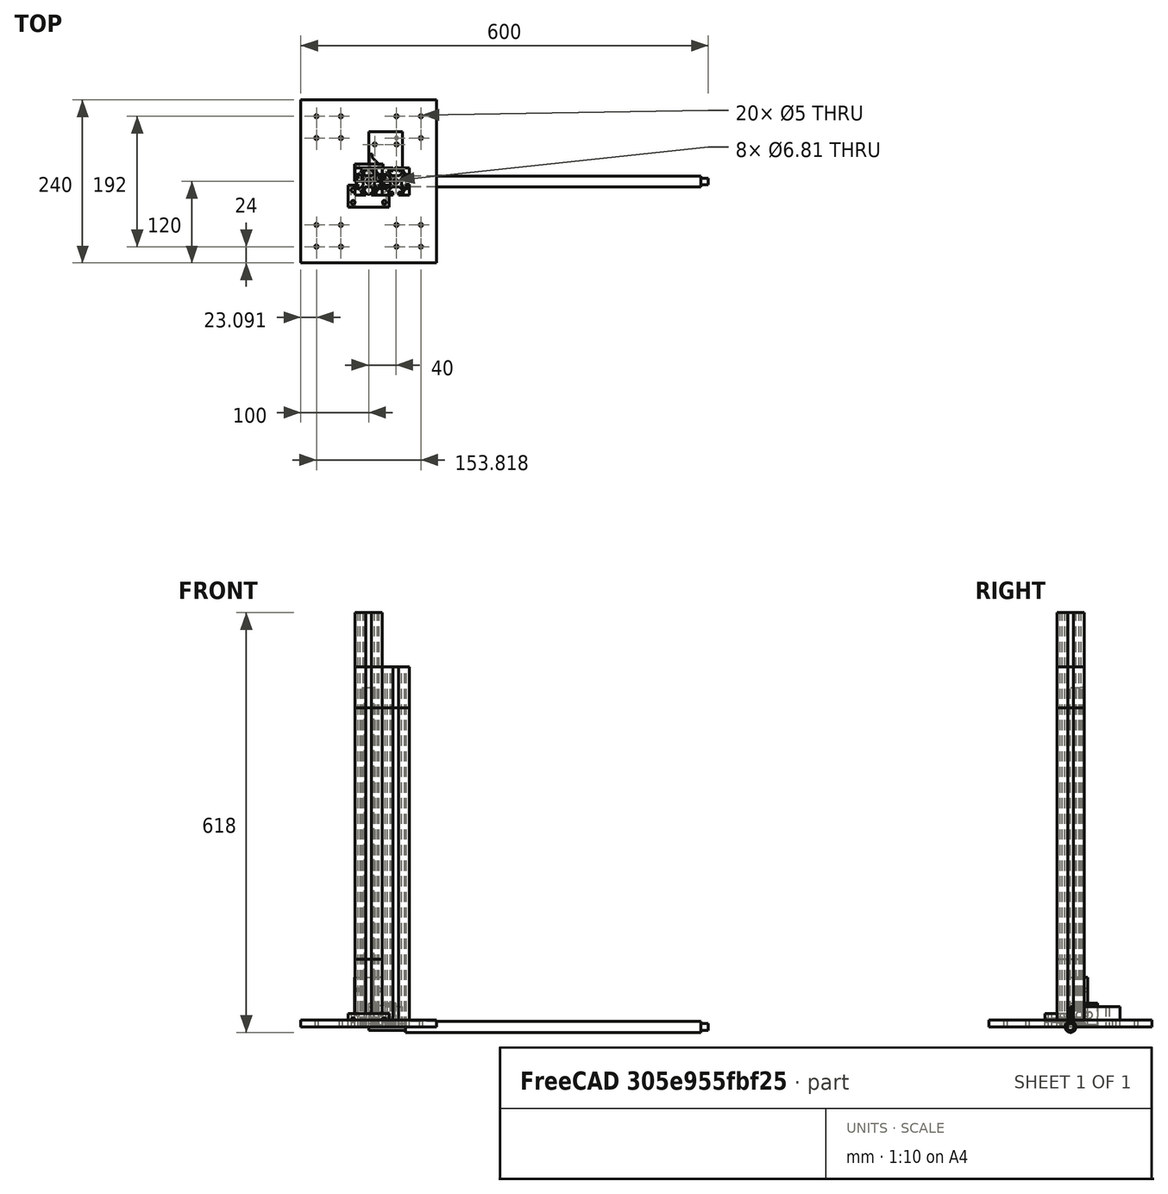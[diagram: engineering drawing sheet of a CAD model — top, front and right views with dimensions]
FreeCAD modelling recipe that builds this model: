
FCSTD DOCUMENT  (FreeCAD 1.1R39140 (Git))
Label: cnc
License: All rights reserved
LicenseURL: http://en.wikipedia.org/wiki/All_rights_reserved
objects: App::FeaturePython×78, App::Link×70, Sketcher::SketchObject×22, PartDesign::Body×12, PartDesign::Pad×11, Part::Extrusion×8, Part::Cut×8, Part::Box×2, PartDesign::Pocket×2, Spreadsheet::Sheet×1, PartDesign::Revolution×1, App::DocumentObjectGroup×1, Assembly::JointGroup×1, Assembly::AssemblyObject×1
note: 116 computed .brp shape members not serialized (recipe doc carries the construction recipe); baked Part::Feature solids carry a one-line shape summary decoded from their .brp
EXTERNAL_REF file=../xcadlib/nema23.FCStd obj=Body

FEATURE [Spreadsheet::Sheet] Spreadsheet
  cells = A1='length (x); B1(length)==24 in; A2='width (y); B2(width)==24 in; A3='height (z); B3(height)==20 in
FEATURE [Sketcher::SketchObject] Sketch001
  ArcFitTolerance = 1e-06
  AttachmentSupport = -> [XY_Plane001]
  FullyConstrained = true
  MakeInternals = false
  MapMode = 5
  sketch-geometry (37):
    g0: LineSegment StartX=-20 StartY=4.065 StartZ=0 EndX=-20 EndY=20 EndZ=0
    g1: LineSegment StartX=-20 StartY=20 StartZ=0 EndX=-4.065 EndY=20 EndZ=0
    g2: LineSegment StartX=-4.065 StartY=20 StartZ=0 EndX=-4.065 EndY=15.68 EndZ=0
    g3: LineSegment StartX=-4.065 StartY=15.68 StartZ=0 EndX=-12.6253 EndY=15.68 EndZ=0
    g4: LineSegment StartX=-12.6253 StartY=15.68 StartZ=0 EndX=-5.22957 EndY=8.28427 EndZ=0
    g5: LineSegment StartX=-5.22957 StartY=8.28427 StartZ=0 EndX=5.22957 EndY=8.28427 EndZ=0
    g6: LineSegment StartX=5.22957 StartY=8.28427 StartZ=0 EndX=12.6253 EndY=15.68 EndZ=0
    g7: LineSegment StartX=12.6253 StartY=15.68 StartZ=0 EndX=4.065 EndY=15.68 EndZ=0
    g8: LineSegment StartX=4.065 StartY=15.68 StartZ=0 EndX=4.065 EndY=20 EndZ=0
    g9: LineSegment StartX=4.065 StartY=20 StartZ=0 EndX=20 EndY=20 EndZ=0
    g10: LineSegment StartX=20 StartY=20 StartZ=0 EndX=20 EndY=4.065 EndZ=0
    g11: LineSegment StartX=20 StartY=4.065 StartZ=0 EndX=15.68 EndY=4.065 EndZ=0
    g12: LineSegment StartX=15.68 StartY=4.065 StartZ=0 EndX=15.68 EndY=12.6253 EndZ=0
    g13: LineSegment StartX=15.68 StartY=12.6253 StartZ=0 EndX=8.28427 EndY=5.22957 EndZ=0
    g14: LineSegment StartX=8.28427 StartY=5.22957 StartZ=0 EndX=8.28427 EndY=-5.22957 EndZ=0
    g15: LineSegment StartX=8.28427 StartY=-5.22957 StartZ=0 EndX=15.68 EndY=-12.6253 EndZ=0
    g16: LineSegment StartX=15.68 StartY=-12.6253 StartZ=0 EndX=15.68 EndY=-4.065 EndZ=0
    g17: LineSegment StartX=15.68 StartY=-4.065 StartZ=0 EndX=20 EndY=-4.065 EndZ=0
    g18: LineSegment StartX=20 StartY=-4.065 StartZ=0 EndX=20 EndY=-20 EndZ=0
    g19: LineSegment StartX=20 StartY=-20 StartZ=0 EndX=4.065 EndY=-20 EndZ=0
    g20: LineSegment StartX=4.065 StartY=-20 StartZ=0 EndX=4.065 EndY=-15.68 EndZ=0
    g21: LineSegment StartX=4.065 StartY=-15.68 StartZ=0 EndX=12.6253 EndY=-15.68 EndZ=0
    g22: LineSegment StartX=12.6253 StartY=-15.68 StartZ=0 EndX=5.22957 EndY=-8.28427 EndZ=0
    g23: LineSegment StartX=5.22957 StartY=-8.28427 StartZ=0 EndX=-5.22957 EndY=-8.28427 EndZ=0
    g24: LineSegment StartX=-5.22957 StartY=-8.28427 StartZ=0 EndX=-12.6253 EndY=-15.68 EndZ=0
    g25: LineSegment StartX=-12.6253 StartY=-15.68 StartZ=0 EndX=-4.065 EndY=-15.68 EndZ=0
    g26: LineSegment StartX=-4.065 StartY=-15.68 StartZ=0 EndX=-4.065 EndY=-20 EndZ=0
    g27: LineSegment StartX=-4.065 StartY=-20 StartZ=0 EndX=-20 EndY=-20 EndZ=0
    g28: LineSegment StartX=-20 StartY=-20 StartZ=0 EndX=-20 EndY=-4.065 EndZ=0
    g29: LineSegment StartX=-20 StartY=-4.065 StartZ=0 EndX=-15.68 EndY=-4.065 EndZ=0
    g30: LineSegment StartX=-15.68 StartY=-4.065 StartZ=0 EndX=-15.68 EndY=-12.6253 EndZ=0
    g31: LineSegment StartX=-15.68 StartY=-12.6253 StartZ=0 EndX=-8.28427 EndY=-5.22957 EndZ=0
    g32: LineSegment StartX=-8.28427 StartY=-5.22957 StartZ=0 EndX=-8.28427 EndY=5.22957 EndZ=0
    g33: LineSegment StartX=-8.28427 StartY=5.22957 StartZ=0 EndX=-15.68 EndY=12.6253 EndZ=0
    g34: LineSegment StartX=-15.68 StartY=12.6253 StartZ=0 EndX=-15.68 EndY=4.065 EndZ=0
    g35: LineSegment StartX=-15.68 StartY=4.065 StartZ=0 EndX=-20 EndY=4.065 EndZ=0
    g36: Circle CenterX=0 CenterY=0 CenterZ=0 NormalX=0 NormalY=0 NormalZ=1 AngleXU=0 Radius=3.405
  constraints (100):
    c: Coincident(g24,g23)
    c: Coincident(g32,g31)
    c: Coincident(g30,g31)
    c: Coincident(g25,g24)
    c: Coincident(g25,g26)
    c: Coincident(g20,g21)
    c: Coincident(g19,g20)
    c: Coincident(g26,g27)
    c: Coincident(g28,g27)
    c: Coincident(g21,g22)
    c: Coincident(g19,g18)
    c: Coincident(g16,g15)
    c: Coincident(g14,g15)
    c: Coincident(g23,g22)
    c: Coincident(g16,g17)
    c: Coincident(g18,g17)
    c: Coincident(g12,g11)
    c: Coincident(g11,g10)
    c: Coincident(g10,g9)
    c: Coincident(g13,g12)
    c: Coincident(g13,g14)
    c: Coincident(g6,g5)
    c: Coincident(g7,g6)
    c: Coincident(g8,g7)
    c: Coincident(g9,g8)
    c: Coincident(g2,g1)
    c: Coincident(g2,g3)
    c: Coincident(g4,g3)
    c: Coincident(g34,g33)
    c: Coincident(g5,g4)
    c: Coincident(g33,g32)
    c: Coincident(g35,g34)
    c: Coincident(g35,g0)
    c: Coincident(g1,g0)
    c: Coincident(g30,g29)
    c: Coincident(g29,g28)
    c: Distance(g10,g0) = 40
    c: Distance(g27,g1) = 40
    c: Tangent(g1,g9)
    c: Tangent(g27,g19)
    c: Tangent(g0,g28)
    c: Tangent(g10,g18)
    c: Horizontal(g1)
    c: Vertical(g0)
    c: Equal(g2,g8)
    c: Equal(g8,g35)
    c: Equal(g35,g29)
    c: Equal(g29,g26)
    c: Equal(g26,g20)
    c: Equal(g20,g17)
    c: Equal(g17,g11)
    c: Vertical(g34)
    c: Vertical(g30)
    c: Vertical(g16)
    c: Vertical(g18)
    c: Vertical(g12)
    c: Vertical(g8)
    c: Vertical(g2)
    c: Vertical(g14)
    c: Vertical(g32)
    c: Horizontal(g35)
    c: Horizontal(g29)
    c: Horizontal(g23)
    c: Horizontal(g19)
    c: Horizontal(g25)
    c: Horizontal(g21)
    c: Horizontal(g7)
    c: Horizontal(g3)
    c: Parallel(g4,g33)
    c: Parallel(g33,g15)
    c: Parallel(g15,g22)
    c: Parallel(g6,g13)
    c: Parallel(g13,g24)
    c: Parallel(g24,g31)
    c: Equal(g23,g24)
    c: Equal(g24,g31)
    c: Equal(g4,g33)
    c: Equal(g6,g13)
    c: Equal(g15,g22)
    c: Angle(g25,g24) = 0.785398
    c: Distance(g8,g2) = 8.13
    c: Distance(g29,g35) = 8.13
    c: Tangent(g35,g11)
    c: Tangent(g17,g29)
    c: Tangent(g2,g26)
    c: Tangent(g8,g20)
    c: Distance(g22,g15) = 4.32
    c: Distance(g13,g6) = 4.32
    c: Distance(g33,g4) = 4.32
    c: Distance(g24,g31) = 4.32
    c: Equal(g32,g14)
    c: Equal(g5,g23)
    c: Equal(g25,g21)
    c: Equal(g34,g30)
    c: Distance(g35,g35) = 4.32
    c: Symmetric(g5,g22,g-1)
    c: Symmetric(g4,g5,g-2)
    c: Equal(g5,g32)
    c: Coincident(g36,g-1)
    c: Diameter(g36) = 6.81
FEATURE [Sketcher::SketchObject] Sketch002
  ArcFitTolerance = 1e-06
  AttachmentSupport = -> [XY_Plane003]
  FullyConstrained = true
  MakeInternals = false
  MapMode = 5
  sketch-geometry (37):
    g0: LineSegment StartX=-20 StartY=4.065 StartZ=0 EndX=-20 EndY=20 EndZ=0
    g1: LineSegment StartX=-20 StartY=20 StartZ=0 EndX=-4.065 EndY=20 EndZ=0
    g2: LineSegment StartX=-4.065 StartY=20 StartZ=0 EndX=-4.065 EndY=15.68 EndZ=0
    g3: LineSegment StartX=-4.065 StartY=15.68 StartZ=0 EndX=-12.6253 EndY=15.68 EndZ=0
    g4: LineSegment StartX=-12.6253 StartY=15.68 StartZ=0 EndX=-5.22957 EndY=8.28427 EndZ=0
    g5: LineSegment StartX=-5.22957 StartY=8.28427 StartZ=0 EndX=5.22957 EndY=8.28427 EndZ=0
    g6: LineSegment StartX=5.22957 StartY=8.28427 StartZ=0 EndX=12.6253 EndY=15.68 EndZ=0
    g7: LineSegment StartX=12.6253 StartY=15.68 StartZ=0 EndX=4.065 EndY=15.68 EndZ=0
    g8: LineSegment StartX=4.065 StartY=15.68 StartZ=0 EndX=4.065 EndY=20 EndZ=0
    g9: LineSegment StartX=4.065 StartY=20 StartZ=0 EndX=20 EndY=20 EndZ=0
    g10: LineSegment StartX=20 StartY=20 StartZ=0 EndX=20 EndY=4.065 EndZ=0
    g11: LineSegment StartX=20 StartY=4.065 StartZ=0 EndX=15.68 EndY=4.065 EndZ=0
    g12: LineSegment StartX=15.68 StartY=4.065 StartZ=0 EndX=15.68 EndY=12.6253 EndZ=0
    g13: LineSegment StartX=15.68 StartY=12.6253 StartZ=0 EndX=8.28427 EndY=5.22957 EndZ=0
    g14: LineSegment StartX=8.28427 StartY=5.22957 StartZ=0 EndX=8.28427 EndY=-5.22957 EndZ=0
    g15: LineSegment StartX=8.28427 StartY=-5.22957 StartZ=0 EndX=15.68 EndY=-12.6253 EndZ=0
    g16: LineSegment StartX=15.68 StartY=-12.6253 StartZ=0 EndX=15.68 EndY=-4.065 EndZ=0
    g17: LineSegment StartX=15.68 StartY=-4.065 StartZ=0 EndX=20 EndY=-4.065 EndZ=0
    g18: LineSegment StartX=20 StartY=-4.065 StartZ=0 EndX=20 EndY=-20 EndZ=0
    g19: LineSegment StartX=20 StartY=-20 StartZ=0 EndX=4.065 EndY=-20 EndZ=0
    g20: LineSegment StartX=4.065 StartY=-20 StartZ=0 EndX=4.065 EndY=-15.68 EndZ=0
    g21: LineSegment StartX=4.065 StartY=-15.68 StartZ=0 EndX=12.6253 EndY=-15.68 EndZ=0
    g22: LineSegment StartX=12.6253 StartY=-15.68 StartZ=0 EndX=5.22957 EndY=-8.28427 EndZ=0
    g23: LineSegment StartX=5.22957 StartY=-8.28427 StartZ=0 EndX=-5.22957 EndY=-8.28427 EndZ=0
    g24: LineSegment StartX=-5.22957 StartY=-8.28427 StartZ=0 EndX=-12.6253 EndY=-15.68 EndZ=0
    g25: LineSegment StartX=-12.6253 StartY=-15.68 StartZ=0 EndX=-4.065 EndY=-15.68 EndZ=0
    g26: LineSegment StartX=-4.065 StartY=-15.68 StartZ=0 EndX=-4.065 EndY=-20 EndZ=0
    g27: LineSegment StartX=-4.065 StartY=-20 StartZ=0 EndX=-20 EndY=-20 EndZ=0
    g28: LineSegment StartX=-20 StartY=-20 StartZ=0 EndX=-20 EndY=-4.065 EndZ=0
    g29: LineSegment StartX=-20 StartY=-4.065 StartZ=0 EndX=-15.68 EndY=-4.065 EndZ=0
    g30: LineSegment StartX=-15.68 StartY=-4.065 StartZ=0 EndX=-15.68 EndY=-12.6253 EndZ=0
    g31: LineSegment StartX=-15.68 StartY=-12.6253 StartZ=0 EndX=-8.28427 EndY=-5.22957 EndZ=0
    g32: LineSegment StartX=-8.28427 StartY=-5.22957 StartZ=0 EndX=-8.28427 EndY=5.22957 EndZ=0
    g33: LineSegment StartX=-8.28427 StartY=5.22957 StartZ=0 EndX=-15.68 EndY=12.6253 EndZ=0
    g34: LineSegment StartX=-15.68 StartY=12.6253 StartZ=0 EndX=-15.68 EndY=4.065 EndZ=0
    g35: LineSegment StartX=-15.68 StartY=4.065 StartZ=0 EndX=-20 EndY=4.065 EndZ=0
    g36: Circle CenterX=0 CenterY=0 CenterZ=0 NormalX=0 NormalY=0 NormalZ=1 AngleXU=0 Radius=3.405
  constraints (100):
    c: Coincident(g24,g23)
    c: Coincident(g32,g31)
    c: Coincident(g30,g31)
    c: Coincident(g25,g24)
    c: Coincident(g25,g26)
    c: Coincident(g20,g21)
    c: Coincident(g19,g20)
    c: Coincident(g26,g27)
    c: Coincident(g28,g27)
    c: Coincident(g21,g22)
    c: Coincident(g19,g18)
    c: Coincident(g16,g15)
    c: Coincident(g14,g15)
    c: Coincident(g23,g22)
    c: Coincident(g16,g17)
    c: Coincident(g18,g17)
    c: Coincident(g12,g11)
    c: Coincident(g11,g10)
    c: Coincident(g10,g9)
    c: Coincident(g13,g12)
    c: Coincident(g13,g14)
    c: Coincident(g6,g5)
    c: Coincident(g7,g6)
    c: Coincident(g8,g7)
    c: Coincident(g9,g8)
    c: Coincident(g2,g1)
    c: Coincident(g2,g3)
    c: Coincident(g4,g3)
    c: Coincident(g34,g33)
    c: Coincident(g5,g4)
    c: Coincident(g33,g32)
    c: Coincident(g35,g34)
    c: Coincident(g35,g0)
    c: Coincident(g1,g0)
    c: Coincident(g30,g29)
    c: Coincident(g29,g28)
    c: Distance(g10,g0) = 40
    c: Distance(g27,g1) = 40
    c: Tangent(g1,g9)
    c: Tangent(g27,g19)
    c: Tangent(g0,g28)
    c: Tangent(g10,g18)
    c: Horizontal(g1)
    c: Vertical(g0)
    c: Equal(g2,g8)
    c: Equal(g8,g35)
    c: Equal(g35,g29)
    c: Equal(g29,g26)
    c: Equal(g26,g20)
    c: Equal(g20,g17)
    c: Equal(g17,g11)
    c: Vertical(g34)
    c: Vertical(g30)
    c: Vertical(g16)
    c: Vertical(g18)
    c: Vertical(g12)
    c: Vertical(g8)
    c: Vertical(g2)
    c: Vertical(g14)
    c: Vertical(g32)
    c: Horizontal(g35)
    c: Horizontal(g29)
    c: Horizontal(g23)
    c: Horizontal(g19)
    c: Horizontal(g25)
    c: Horizontal(g21)
    c: Horizontal(g7)
    c: Horizontal(g3)
    c: Parallel(g4,g33)
    c: Parallel(g33,g15)
    c: Parallel(g15,g22)
    c: Parallel(g6,g13)
    c: Parallel(g13,g24)
    c: Parallel(g24,g31)
    c: Equal(g23,g24)
    c: Equal(g24,g31)
    c: Equal(g4,g33)
    c: Equal(g6,g13)
    c: Equal(g15,g22)
    c: Angle(g25,g24) = 0.785398
    c: Distance(g8,g2) = 8.13
    c: Distance(g29,g35) = 8.13
    c: Tangent(g35,g11)
    c: Tangent(g17,g29)
    c: Tangent(g2,g26)
    c: Tangent(g8,g20)
    c: Distance(g22,g15) = 4.32
    c: Distance(g13,g6) = 4.32
    c: Distance(g33,g4) = 4.32
    c: Distance(g24,g31) = 4.32
    c: Equal(g32,g14)
    c: Equal(g5,g23)
    c: Equal(g25,g21)
    c: Equal(g34,g30)
    c: Distance(g35,g35) = 4.32
    c: Symmetric(g5,g22,g-1)
    c: Symmetric(g4,g5,g-2)
    c: Equal(g5,g32)
    c: Coincident(g36,g-1)
    c: Diameter(g36) = 6.81
FEATURE [PartDesign::Pad] Pad
  Direction = (0,0,1)
  Length = 610
  Length2 = 10
  Profile = -> Sketch001
  ReferenceAxis = -> Sketch001 [N_Axis]
  Refine = true
  Suppressed = false
  Type = 0
FEATURE [PartDesign::Body] Body001  label="4040 extrusion @ 610"
  AllowCompound = false
  Group = -> [Sketch001,Pad]
  Origin = -> Origin001
  Tip = -> Pad
FEATURE [PartDesign::Pad] Pad001
  Direction = (0,0,1)
  Length = 530
  Length2 = 10
  Profile = -> Sketch002
  ReferenceAxis = -> Sketch002 [N_Axis]
  Refine = true
  Suppressed = false
  Type = 0
FEATURE [PartDesign::Body] Body002  label="4040 extrusion @ 530"
  AllowCompound = false
  Group = -> [Sketch002,Pad001]
  Origin = -> Origin003
  Tip = -> Pad001
FEATURE [Sketcher::SketchObject] Sketch003
  ArcFitTolerance = 1e-06
  AttachmentSupport = -> [XY_Plane005]
  FullyConstrained = true
  MakeInternals = false
  MapMode = 5
  sketch-geometry (37):
    g0: LineSegment StartX=-20 StartY=4.065 StartZ=0 EndX=-20 EndY=20 EndZ=0
    g1: LineSegment StartX=-20 StartY=20 StartZ=0 EndX=-4.065 EndY=20 EndZ=0
    g2: LineSegment StartX=-4.065 StartY=20 StartZ=0 EndX=-4.065 EndY=15.68 EndZ=0
    g3: LineSegment StartX=-4.065 StartY=15.68 StartZ=0 EndX=-12.6253 EndY=15.68 EndZ=0
    g4: LineSegment StartX=-12.6253 StartY=15.68 StartZ=0 EndX=-5.22957 EndY=8.28427 EndZ=0
    g5: LineSegment StartX=-5.22957 StartY=8.28427 StartZ=0 EndX=5.22957 EndY=8.28427 EndZ=0
    g6: LineSegment StartX=5.22957 StartY=8.28427 StartZ=0 EndX=12.6253 EndY=15.68 EndZ=0
    g7: LineSegment StartX=12.6253 StartY=15.68 StartZ=0 EndX=4.065 EndY=15.68 EndZ=0
    g8: LineSegment StartX=4.065 StartY=15.68 StartZ=0 EndX=4.065 EndY=20 EndZ=0
    g9: LineSegment StartX=4.065 StartY=20 StartZ=0 EndX=20 EndY=20 EndZ=0
    g10: LineSegment StartX=20 StartY=20 StartZ=0 EndX=20 EndY=4.065 EndZ=0
    g11: LineSegment StartX=20 StartY=4.065 StartZ=0 EndX=15.68 EndY=4.065 EndZ=0
    g12: LineSegment StartX=15.68 StartY=4.065 StartZ=0 EndX=15.68 EndY=12.6253 EndZ=0
    g13: LineSegment StartX=15.68 StartY=12.6253 StartZ=0 EndX=8.28427 EndY=5.22957 EndZ=0
    g14: LineSegment StartX=8.28427 StartY=5.22957 StartZ=0 EndX=8.28427 EndY=-5.22957 EndZ=0
    g15: LineSegment StartX=8.28427 StartY=-5.22957 StartZ=0 EndX=15.68 EndY=-12.6253 EndZ=0
    g16: LineSegment StartX=15.68 StartY=-12.6253 StartZ=0 EndX=15.68 EndY=-4.065 EndZ=0
    g17: LineSegment StartX=15.68 StartY=-4.065 StartZ=0 EndX=20 EndY=-4.065 EndZ=0
    g18: LineSegment StartX=20 StartY=-4.065 StartZ=0 EndX=20 EndY=-20 EndZ=0
    g19: LineSegment StartX=20 StartY=-20 StartZ=0 EndX=4.065 EndY=-20 EndZ=0
    g20: LineSegment StartX=4.065 StartY=-20 StartZ=0 EndX=4.065 EndY=-15.68 EndZ=0
    g21: LineSegment StartX=4.065 StartY=-15.68 StartZ=0 EndX=12.6253 EndY=-15.68 EndZ=0
    g22: LineSegment StartX=12.6253 StartY=-15.68 StartZ=0 EndX=5.22957 EndY=-8.28427 EndZ=0
    g23: LineSegment StartX=5.22957 StartY=-8.28427 StartZ=0 EndX=-5.22957 EndY=-8.28427 EndZ=0
    g24: LineSegment StartX=-5.22957 StartY=-8.28427 StartZ=0 EndX=-12.6253 EndY=-15.68 EndZ=0
    g25: LineSegment StartX=-12.6253 StartY=-15.68 StartZ=0 EndX=-4.065 EndY=-15.68 EndZ=0
    g26: LineSegment StartX=-4.065 StartY=-15.68 StartZ=0 EndX=-4.065 EndY=-20 EndZ=0
    g27: LineSegment StartX=-4.065 StartY=-20 StartZ=0 EndX=-20 EndY=-20 EndZ=0
    g28: LineSegment StartX=-20 StartY=-20 StartZ=0 EndX=-20 EndY=-4.065 EndZ=0
    g29: LineSegment StartX=-20 StartY=-4.065 StartZ=0 EndX=-15.68 EndY=-4.065 EndZ=0
    g30: LineSegment StartX=-15.68 StartY=-4.065 StartZ=0 EndX=-15.68 EndY=-12.6253 EndZ=0
    g31: LineSegment StartX=-15.68 StartY=-12.6253 StartZ=0 EndX=-8.28427 EndY=-5.22957 EndZ=0
    g32: LineSegment StartX=-8.28427 StartY=-5.22957 StartZ=0 EndX=-8.28427 EndY=5.22957 EndZ=0
    g33: LineSegment StartX=-8.28427 StartY=5.22957 StartZ=0 EndX=-15.68 EndY=12.6253 EndZ=0
    g34: LineSegment StartX=-15.68 StartY=12.6253 StartZ=0 EndX=-15.68 EndY=4.065 EndZ=0
    g35: LineSegment StartX=-15.68 StartY=4.065 StartZ=0 EndX=-20 EndY=4.065 EndZ=0
    g36: Circle CenterX=0 CenterY=0 CenterZ=0 NormalX=0 NormalY=0 NormalZ=1 AngleXU=0 Radius=3.405
  constraints (100):
    c: Coincident(g24,g23)
    c: Coincident(g32,g31)
    c: Coincident(g30,g31)
    c: Coincident(g25,g24)
    c: Coincident(g25,g26)
    c: Coincident(g20,g21)
    c: Coincident(g19,g20)
    c: Coincident(g26,g27)
    c: Coincident(g28,g27)
    c: Coincident(g21,g22)
    c: Coincident(g19,g18)
    c: Coincident(g16,g15)
    c: Coincident(g14,g15)
    c: Coincident(g23,g22)
    c: Coincident(g16,g17)
    c: Coincident(g18,g17)
    c: Coincident(g12,g11)
    c: Coincident(g11,g10)
    c: Coincident(g10,g9)
    c: Coincident(g13,g12)
    c: Coincident(g13,g14)
    c: Coincident(g6,g5)
    c: Coincident(g7,g6)
    c: Coincident(g8,g7)
    c: Coincident(g9,g8)
    c: Coincident(g2,g1)
    c: Coincident(g2,g3)
    c: Coincident(g4,g3)
    c: Coincident(g34,g33)
    c: Coincident(g5,g4)
    c: Coincident(g33,g32)
    c: Coincident(g35,g34)
    c: Coincident(g35,g0)
    c: Coincident(g1,g0)
    c: Coincident(g30,g29)
    c: Coincident(g29,g28)
    c: Distance(g10,g0) = 40
    c: Distance(g27,g1) = 40
    c: Tangent(g1,g9)
    c: Tangent(g27,g19)
    c: Tangent(g0,g28)
    c: Tangent(g10,g18)
    c: Horizontal(g1)
    c: Vertical(g0)
    c: Equal(g2,g8)
    c: Equal(g8,g35)
    c: Equal(g35,g29)
    c: Equal(g29,g26)
    c: Equal(g26,g20)
    c: Equal(g20,g17)
    c: Equal(g17,g11)
    c: Vertical(g34)
    c: Vertical(g30)
    c: Vertical(g16)
    c: Vertical(g18)
    c: Vertical(g12)
    c: Vertical(g8)
    c: Vertical(g2)
    c: Vertical(g14)
    c: Vertical(g32)
    c: Horizontal(g35)
    c: Horizontal(g29)
    c: Horizontal(g23)
    c: Horizontal(g19)
    c: Horizontal(g25)
    c: Horizontal(g21)
    c: Horizontal(g7)
    c: Horizontal(g3)
    c: Parallel(g4,g33)
    c: Parallel(g33,g15)
    c: Parallel(g15,g22)
    c: Parallel(g6,g13)
    c: Parallel(g13,g24)
    c: Parallel(g24,g31)
    c: Equal(g23,g24)
    c: Equal(g24,g31)
    c: Equal(g4,g33)
    c: Equal(g6,g13)
    c: Equal(g15,g22)
    c: Angle(g25,g24) = 0.785398
    c: Distance(g8,g2) = 8.13
    c: Distance(g29,g35) = 8.13
    c: Tangent(g35,g11)
    c: Tangent(g17,g29)
    c: Tangent(g2,g26)
    c: Tangent(g8,g20)
    c: Distance(g22,g15) = 4.32
    c: Distance(g13,g6) = 4.32
    c: Distance(g33,g4) = 4.32
    c: Distance(g24,g31) = 4.32
    c: Equal(g32,g14)
    c: Equal(g5,g23)
    c: Equal(g25,g21)
    c: Equal(g34,g30)
    c: Distance(g35,g35) = 4.32
    c: Symmetric(g5,g22,g-1)
    c: Symmetric(g4,g5,g-2)
    c: Equal(g5,g32)
    c: Coincident(g36,g-1)
    c: Diameter(g36) = 6.81
FEATURE [PartDesign::Pad] Pad002
  Direction = (0,0,1)
  Length = 470
  Length2 = 10
  Profile = -> Sketch003
  ReferenceAxis = -> Sketch003 [N_Axis]
  Refine = true
  Suppressed = false
  Type = 0
FEATURE [PartDesign::Body] Body003  label="4040 extrusion @ 470"
  AllowCompound = false
  Group = -> [Sketch003,Pad002]
  Origin = -> Origin005
  Tip = -> Pad002
FEATURE [Sketcher::SketchObject] Sketch004
  ArcFitTolerance = 1e-06
  AttachmentSupport = -> [XY_Plane006]
  FullyConstrained = true
  MakeInternals = false
  MapMode = 5
  sketch-geometry (70):
    g0: LineSegment StartX=-20 StartY=4.065 StartZ=0 EndX=-20 EndY=20 EndZ=0
    g1: LineSegment StartX=-20 StartY=20 StartZ=0 EndX=-4.065 EndY=20 EndZ=0
    g2: LineSegment StartX=-4.065 StartY=20 StartZ=0 EndX=-4.065 EndY=15.68 EndZ=0
    g3: LineSegment StartX=-4.065 StartY=15.68 StartZ=0 EndX=-12.6253 EndY=15.68 EndZ=0
    g4: LineSegment StartX=-12.6253 StartY=15.68 StartZ=0 EndX=-5.22957 EndY=8.28427 EndZ=0
    g5: LineSegment StartX=-5.22957 StartY=8.28427 StartZ=0 EndX=5.22957 EndY=8.28427 EndZ=0
    g6: LineSegment StartX=5.22957 StartY=8.28427 StartZ=0 EndX=12.6253 EndY=15.68 EndZ=0
    g7: LineSegment StartX=12.6253 StartY=15.68 StartZ=0 EndX=4.065 EndY=15.68 EndZ=0
    g8: LineSegment StartX=4.065 StartY=15.68 StartZ=0 EndX=4.065 EndY=20 EndZ=0
    g9: LineSegment StartX=4.065 StartY=20 StartZ=0 EndX=20 EndY=20 EndZ=0
    g10: LineSegment StartX=20 StartY=4.065 StartZ=0 EndX=15.68 EndY=4.065 EndZ=0
    g11: LineSegment StartX=15.68 StartY=4.065 StartZ=0 EndX=15.68 EndY=12.6253 EndZ=0
    g12: LineSegment StartX=15.68 StartY=12.6253 StartZ=0 EndX=8.28427 EndY=5.22957 EndZ=0
    g13: LineSegment StartX=8.28427 StartY=5.22957 StartZ=0 EndX=8.28427 EndY=-5.22957 EndZ=0
    g14: LineSegment StartX=8.28427 StartY=-5.22957 StartZ=0 EndX=15.68 EndY=-12.6253 EndZ=0
    g15: LineSegment StartX=15.68 StartY=-12.6253 StartZ=0 EndX=15.68 EndY=-4.065 EndZ=0
    g16: LineSegment StartX=15.68 StartY=-4.065 StartZ=0 EndX=20 EndY=-4.065 EndZ=0
    g17: LineSegment StartX=20 StartY=-20 StartZ=0 EndX=4.065 EndY=-20 EndZ=0
    g18: LineSegment StartX=4.065 StartY=-20 StartZ=0 EndX=4.065 EndY=-15.68 EndZ=0
    g19: LineSegment StartX=4.065 StartY=-15.68 StartZ=0 EndX=12.6253 EndY=-15.68 EndZ=0
    g20: LineSegment StartX=12.6253 StartY=-15.68 StartZ=0 EndX=5.22957 EndY=-8.28427 EndZ=0
    g21: LineSegment StartX=5.22957 StartY=-8.28427 StartZ=0 EndX=-5.22957 EndY=-8.28427 EndZ=0
    g22: LineSegment StartX=-5.22957 StartY=-8.28427 StartZ=0 EndX=-12.6253 EndY=-15.68 EndZ=0
    g23: LineSegment StartX=-12.6253 StartY=-15.68 StartZ=0 EndX=-4.065 EndY=-15.68 EndZ=0
    g24: LineSegment StartX=-4.065 StartY=-15.68 StartZ=0 EndX=-4.065 EndY=-20 EndZ=0
    g25: LineSegment StartX=-4.065 StartY=-20 StartZ=0 EndX=-20 EndY=-20 EndZ=0
    g26: LineSegment StartX=-20 StartY=-20 StartZ=0 EndX=-20 EndY=-4.065 EndZ=0
    g27: LineSegment StartX=-20 StartY=-4.065 StartZ=0 EndX=-15.68 EndY=-4.065 EndZ=0
    g28: LineSegment StartX=-15.68 StartY=-4.065 StartZ=0 EndX=-15.68 EndY=-12.6253 EndZ=0
    g29: LineSegment StartX=-15.68 StartY=-12.6253 StartZ=0 EndX=-8.28427 EndY=-5.22957 EndZ=0
    g30: LineSegment StartX=-8.28427 StartY=-5.22957 StartZ=0 EndX=-8.28427 EndY=5.22957 EndZ=0
    g31: LineSegment StartX=-8.28427 StartY=5.22957 StartZ=0 EndX=-15.68 EndY=12.6253 EndZ=0
    g32: LineSegment StartX=-15.68 StartY=12.6253 StartZ=0 EndX=-15.68 EndY=4.065 EndZ=0
    g33: LineSegment StartX=-15.68 StartY=4.065 StartZ=0 EndX=-20 EndY=4.065 EndZ=0
    g34: Circle CenterX=0 CenterY=0 CenterZ=0 NormalX=0 NormalY=0 NormalZ=1 AngleXU=0 Radius=3.405
    g35: LineSegment StartX=20 StartY=20 StartZ=0 EndX=35.935 EndY=20 EndZ=0
    g36: LineSegment StartX=35.935 StartY=20 StartZ=0 EndX=35.935 EndY=15.68 EndZ=0
    g37: LineSegment StartX=35.935 StartY=15.68 StartZ=0 EndX=27.3747 EndY=15.68 EndZ=0
    g38: LineSegment StartX=27.3747 StartY=15.68 StartZ=0 EndX=34.7704 EndY=8.28427 EndZ=0
    g39: LineSegment StartX=34.7704 StartY=8.28427 StartZ=0 EndX=45.2296 EndY=8.28427 EndZ=0
    g40: LineSegment StartX=45.2296 StartY=8.28427 StartZ=0 EndX=52.6253 EndY=15.68 EndZ=0
    g41: LineSegment StartX=52.6253 StartY=15.68 StartZ=0 EndX=44.065 EndY=15.68 EndZ=0
    g42: LineSegment StartX=44.065 StartY=15.68 StartZ=0 EndX=44.065 EndY=20 EndZ=0
    g43: LineSegment StartX=44.065 StartY=20 StartZ=0 EndX=60 EndY=20 EndZ=0
    g44: LineSegment StartX=60 StartY=20 StartZ=0 EndX=60 EndY=4.065 EndZ=0
    g45: LineSegment StartX=60 StartY=4.065 StartZ=0 EndX=55.68 EndY=4.065 EndZ=0
    g46: LineSegment StartX=55.68 StartY=4.065 StartZ=0 EndX=55.68 EndY=12.6253 EndZ=0
    g47: LineSegment StartX=55.68 StartY=12.6253 StartZ=0 EndX=48.2843 EndY=5.22957 EndZ=0
    g48: LineSegment StartX=48.2843 StartY=5.22957 StartZ=0 EndX=48.2843 EndY=-5.22957 EndZ=0
    g49: LineSegment StartX=48.2843 StartY=-5.22957 StartZ=0 EndX=55.68 EndY=-12.6253 EndZ=0
    g50: LineSegment StartX=55.68 StartY=-12.6253 StartZ=0 EndX=55.68 EndY=-4.065 EndZ=0
    g51: LineSegment StartX=55.68 StartY=-4.065 StartZ=0 EndX=60 EndY=-4.065 EndZ=0
    g52: LineSegment StartX=60 StartY=-4.065 StartZ=0 EndX=60 EndY=-20 EndZ=0
    g53: LineSegment StartX=60 StartY=-20 StartZ=0 EndX=44.065 EndY=-20 EndZ=0
    g54: LineSegment StartX=44.065 StartY=-20 StartZ=0 EndX=44.065 EndY=-15.68 EndZ=0
    g55: LineSegment StartX=44.065 StartY=-15.68 StartZ=0 EndX=52.6253 EndY=-15.68 EndZ=0
    g56: LineSegment StartX=52.6253 StartY=-15.68 StartZ=0 EndX=45.2296 EndY=-8.28427 EndZ=0
    g57: LineSegment StartX=45.2296 StartY=-8.28427 StartZ=0 EndX=34.7704 EndY=-8.28427 EndZ=0
    g58: LineSegment StartX=34.7704 StartY=-8.28427 StartZ=0 EndX=27.3747 EndY=-15.68 EndZ=0
    g59: LineSegment StartX=27.3747 StartY=-15.68 StartZ=0 EndX=35.935 EndY=-15.68 EndZ=0
    g60: LineSegment StartX=35.935 StartY=-15.68 StartZ=0 EndX=35.935 EndY=-20 EndZ=0
    g61: LineSegment StartX=35.935 StartY=-20 StartZ=0 EndX=20 EndY=-20 EndZ=0
    g62: LineSegment StartX=24.32 StartY=12.6253 StartZ=0 EndX=24.32 EndY=4.065 EndZ=0
    g63: LineSegment StartX=24.32 StartY=4.065 StartZ=0 EndX=20 EndY=4.065 EndZ=0
    g64: LineSegment StartX=20 StartY=-4.065 StartZ=0 EndX=24.32 EndY=-4.065 EndZ=0
    g65: LineSegment StartX=24.32 StartY=-4.065 StartZ=0 EndX=24.32 EndY=-12.6253 EndZ=0
    g66: LineSegment StartX=24.32 StartY=-12.6253 StartZ=0 EndX=31.7157 EndY=-5.22957 EndZ=0
    g67: LineSegment StartX=31.7157 StartY=-5.22957 StartZ=0 EndX=31.7157 EndY=5.22957 EndZ=0
    g68: LineSegment StartX=31.7157 StartY=5.22957 StartZ=0 EndX=24.32 EndY=12.6253 EndZ=0
    g69: Circle CenterX=40 CenterY=0 CenterZ=0 NormalX=0 NormalY=0 NormalZ=1 AngleXU=0 Radius=3.405
  constraints (200):
    c: Coincident(g22,g21)
    c: Coincident(g30,g29)
    c: Coincident(g28,g29)
    c: Coincident(g23,g22)
    c: Coincident(g23,g24)
    c: Coincident(g18,g19)
    c: Coincident(g17,g18)
    c: Coincident(g24,g25)
    c: Coincident(g26,g25)
    c: Coincident(g19,g20)
    c: Coincident(g15,g14)
    c: Coincident(g13,g14)
    c: Coincident(g21,g20)
    c: Coincident(g15,g16)
    c: Coincident(g11,g10)
    c: Coincident(g12,g11)
    c: Coincident(g12,g13)
    c: Coincident(g6,g5)
    c: Coincident(g7,g6)
    c: Coincident(g8,g7)
    c: Coincident(g9,g8)
    c: Coincident(g2,g1)
    c: Coincident(g2,g3)
    c: Coincident(g4,g3)
    c: Coincident(g32,g31)
    c: Coincident(g5,g4)
    c: Coincident(g31,g30)
    c: Coincident(g33,g32)
    c: Coincident(g33,g0)
    c: Coincident(g1,g0)
    c: Coincident(g28,g27)
    c: Coincident(g27,g26)
    c: Distance(g9,g0) = 40
    c: Distance(g25,g1) = 40
    c: Tangent(g1,g9)
    c: Tangent(g25,g17)
    c: Tangent(g0,g26)
    c: Horizontal(g1)
    c: Vertical(g0)
    c: Equal(g2,g8)
    c: Equal(g8,g33)
    c: Equal(g33,g27)
    c: Equal(g27,g24)
    c: Equal(g24,g18)
    c: Equal(g18,g16)
    c: Equal(g16,g10)
    c: Vertical(g32)
    c: Vertical(g28)
    c: Vertical(g15)
    c: Vertical(g11)
    c: Vertical(g8)
    c: Vertical(g2)
    c: Vertical(g13)
    c: Vertical(g30)
    c: Horizontal(g33)
    c: Horizontal(g27)
    c: Horizontal(g21)
    c: Horizontal(g17)
    c: Horizontal(g23)
    c: Horizontal(g19)
    c: Horizontal(g7)
    c: Horizontal(g3)
    c: Parallel(g4,g31)
    c: Parallel(g31,g14)
    c: Parallel(g14,g20)
    c: Parallel(g6,g12)
    c: Parallel(g12,g22)
    c: Parallel(g22,g29)
    c: Equal(g21,g22)
    c: Equal(g22,g29)
    c: Equal(g4,g31)
    c: Equal(g6,g12)
    c: Equal(g14,g20)
    c: Angle(g23,g22) = 0.785398
    c: Distance(g8,g2) = 8.13
    c: Distance(g27,g33) = 8.13
    c: Tangent(g33,g10)
    c: Tangent(g16,g27)
    c: Tangent(g2,g24)
    c: Tangent(g8,g18)
    c: Distance(g20,g14) = 4.32
    c: Distance(g12,g6) = 4.32
    c: Distance(g31,g4) = 4.32
    c: Distance(g22,g29) = 4.32
    c: Equal(g30,g13)
    c: Equal(g5,g21)
    c: Equal(g23,g19)
    c: Equal(g32,g28)
    c: Distance(g33,g33) = 4.32
    c: Symmetric(g5,g20,g-1)
    c: Symmetric(g4,g5,g-2)
    c: Equal(g5,g30)
    c: Coincident(g34,g-1)
    c: Diameter(g34) = 6.81
    c: Coincident(g35,g9)
    c: Coincident(g36,g35)
    c: Coincident(g37,g36)
    c: Horizontal(g37)
    c: Coincident(g38,g37)
    c: Coincident(g39,g38)
    c: Horizontal(g39)
    c: Coincident(g41,g40)
    c: Vertical(g44)
    c: Coincident(g45,g44)
    c: Coincident(g48,g47)
    c: Vertical(g48)
    c: Coincident(g49,g48)
    c: Vertical(g50)
    c: Horizontal(g51)
    c: Coincident(g52,g51)
    c: Vertical(g52)
    c: Coincident(g53,g52)
    c: Coincident(g55,g54)
    c: Coincident(g57,g56)
    c: Horizontal(g57)
    c: Coincident(g58,g57)
    c: Coincident(g59,g58)
    c: Horizontal(g59)
    c: Coincident(g61,g60)
    c: Coincident(g61,g17)
    c: Coincident(g63,g10)
    c: Coincident(g64,g16)
    c: Coincident(g65,g64)
    c: Coincident(g66,g65)
    c: Coincident(g67,g66)
    c: Coincident(g68,g67)
    c: Coincident(g68,g62)
    c: PointOnObject(g69,g-1)
    c: Coincident(g43,g42)
    c: Coincident(g43,g44)
    c: Coincident(g41,g42)
    c: Coincident(g39,g40)
    c: Coincident(g46,g47)
    c: Coincident(g46,g45)
    c: Coincident(g50,g51)
    c: Coincident(g49,g50)
    c: Coincident(g54,g53)
    c: Coincident(g56,g55)
    c: Coincident(g59,g60)
    c: Coincident(g62,g63)
    c: Equal(g34,g69)
    c: Equal(g39,g67)
    c: Equal(g67,g57)
    c: Equal(g57,g48)
    c: Equal(g48,g13)
    c: Equal(g38,g68)
    c: Equal(g68,g66)
    c: Equal(g66,g58)
    c: Equal(g58,g56)
    c: Equal(g56,g49)
    c: Equal(g49,g47)
    c: Equal(g47,g40)
    c: Equal(g40,g12)
    c: Equal(g10,g63)
    c: Equal(g16,g64)
    c: Equal(g64,g45)
    c: Equal(g45,g51)
    c: Equal(g51,g42)
    c: Equal(g42,g36)
    c: Equal(g36,g60)
    c: Equal(g60,g54)
    c: Parallel(g47,g40)
    c: Parallel(g38,g68)
    c: Parallel(g66,g58)
    c: Parallel(g49,g56)
    c: Parallel(g56,g68)
    c: Parallel(g40,g66)
    c: Horizontal(g35)
    c: Horizontal(g43)
    c: Horizontal(g45)
    c: Horizontal(g53)
    c: Horizontal(g61)
    c: Horizontal(g64)
    c: Horizontal(g63)
    c: Horizontal(g41)
    c: Vertical(g42)
    c: Vertical(g36)
    c: Vertical(g62)
    c: Vertical(g65)
    c: Vertical(g60)
    c: Vertical(g54)
    c: Vertical(g46)
    c: Horizontal(g55)
    c: Vertical(g67)
    c: Equal(g7,g37)
    c: Equal(g37,g41)
    c: Equal(g41,g46)
    c: Equal(g46,g55)
    c: Equal(g55,g59)
    c: Equal(g59,g65)
    c: Equal(g65,g62)
    c: Equal(g55,g50)
    c: Parallel(g40,g6)
    c: Distance(g9,g44) = 40
    c: DistanceX(g34,g69) = 40
    c: Equal(g35,g43)
    c: Equal(g43,g9)
    c: Equal(g44,g52)
    c: Equal(g53,g61)
    c: Equal(g61,g17)
FEATURE [PartDesign::Pad] Pad003
  Direction = (0,0,1)
  Length = 530
  Length2 = 10
  Profile = -> Sketch004
  ReferenceAxis = -> Sketch004 [N_Axis]
  Refine = true
  Suppressed = false
  Type = 0
FEATURE [PartDesign::Body] Body004  label="8040 extrusion @ 530"
  AllowCompound = false
  Group = -> [Sketch004,Pad003]
  Origin = -> Origin006
  Tip = -> Pad003
FEATURE [Sketcher::SketchObject] Sketch005
  ArcFitTolerance = 1e-06
  AttachmentSupport = -> [XY_Plane007]
  FullyConstrained = true
  MakeInternals = false
  MapMode = 5
  sketch-geometry (70):
    g0: LineSegment StartX=-20 StartY=4.065 StartZ=0 EndX=-20 EndY=20 EndZ=0
    g1: LineSegment StartX=-20 StartY=20 StartZ=0 EndX=-4.065 EndY=20 EndZ=0
    g2: LineSegment StartX=-4.065 StartY=20 StartZ=0 EndX=-4.065 EndY=15.68 EndZ=0
    g3: LineSegment StartX=-4.065 StartY=15.68 StartZ=0 EndX=-12.6253 EndY=15.68 EndZ=0
    g4: LineSegment StartX=-12.6253 StartY=15.68 StartZ=0 EndX=-5.22957 EndY=8.28427 EndZ=0
    g5: LineSegment StartX=-5.22957 StartY=8.28427 StartZ=0 EndX=5.22957 EndY=8.28427 EndZ=0
    g6: LineSegment StartX=5.22957 StartY=8.28427 StartZ=0 EndX=12.6253 EndY=15.68 EndZ=0
    g7: LineSegment StartX=12.6253 StartY=15.68 StartZ=0 EndX=4.065 EndY=15.68 EndZ=0
    g8: LineSegment StartX=4.065 StartY=15.68 StartZ=0 EndX=4.065 EndY=20 EndZ=0
    g9: LineSegment StartX=4.065 StartY=20 StartZ=0 EndX=20 EndY=20 EndZ=0
    g10: LineSegment StartX=20 StartY=4.065 StartZ=0 EndX=15.68 EndY=4.065 EndZ=0
    g11: LineSegment StartX=15.68 StartY=4.065 StartZ=0 EndX=15.68 EndY=12.6253 EndZ=0
    g12: LineSegment StartX=15.68 StartY=12.6253 StartZ=0 EndX=8.28427 EndY=5.22957 EndZ=0
    g13: LineSegment StartX=8.28427 StartY=5.22957 StartZ=0 EndX=8.28427 EndY=-5.22957 EndZ=0
    g14: LineSegment StartX=8.28427 StartY=-5.22957 StartZ=0 EndX=15.68 EndY=-12.6253 EndZ=0
    g15: LineSegment StartX=15.68 StartY=-12.6253 StartZ=0 EndX=15.68 EndY=-4.065 EndZ=0
    g16: LineSegment StartX=15.68 StartY=-4.065 StartZ=0 EndX=20 EndY=-4.065 EndZ=0
    g17: LineSegment StartX=20 StartY=-20 StartZ=0 EndX=4.065 EndY=-20 EndZ=0
    g18: LineSegment StartX=4.065 StartY=-20 StartZ=0 EndX=4.065 EndY=-15.68 EndZ=0
    g19: LineSegment StartX=4.065 StartY=-15.68 StartZ=0 EndX=12.6253 EndY=-15.68 EndZ=0
    g20: LineSegment StartX=12.6253 StartY=-15.68 StartZ=0 EndX=5.22957 EndY=-8.28427 EndZ=0
    g21: LineSegment StartX=5.22957 StartY=-8.28427 StartZ=0 EndX=-5.22957 EndY=-8.28427 EndZ=0
    g22: LineSegment StartX=-5.22957 StartY=-8.28427 StartZ=0 EndX=-12.6253 EndY=-15.68 EndZ=0
    g23: LineSegment StartX=-12.6253 StartY=-15.68 StartZ=0 EndX=-4.065 EndY=-15.68 EndZ=0
    g24: LineSegment StartX=-4.065 StartY=-15.68 StartZ=0 EndX=-4.065 EndY=-20 EndZ=0
    g25: LineSegment StartX=-4.065 StartY=-20 StartZ=0 EndX=-20 EndY=-20 EndZ=0
    g26: LineSegment StartX=-20 StartY=-20 StartZ=0 EndX=-20 EndY=-4.065 EndZ=0
    g27: LineSegment StartX=-20 StartY=-4.065 StartZ=0 EndX=-15.68 EndY=-4.065 EndZ=0
    g28: LineSegment StartX=-15.68 StartY=-4.065 StartZ=0 EndX=-15.68 EndY=-12.6253 EndZ=0
    g29: LineSegment StartX=-15.68 StartY=-12.6253 StartZ=0 EndX=-8.28427 EndY=-5.22957 EndZ=0
    g30: LineSegment StartX=-8.28427 StartY=-5.22957 StartZ=0 EndX=-8.28427 EndY=5.22957 EndZ=0
    g31: LineSegment StartX=-8.28427 StartY=5.22957 StartZ=0 EndX=-15.68 EndY=12.6253 EndZ=0
    g32: LineSegment StartX=-15.68 StartY=12.6253 StartZ=0 EndX=-15.68 EndY=4.065 EndZ=0
    g33: LineSegment StartX=-15.68 StartY=4.065 StartZ=0 EndX=-20 EndY=4.065 EndZ=0
    g34: Circle CenterX=0 CenterY=0 CenterZ=0 NormalX=0 NormalY=0 NormalZ=1 AngleXU=0 Radius=3.405
    g35: LineSegment StartX=20 StartY=20 StartZ=0 EndX=35.935 EndY=20 EndZ=0
    g36: LineSegment StartX=35.935 StartY=20 StartZ=0 EndX=35.935 EndY=15.68 EndZ=0
    g37: LineSegment StartX=35.935 StartY=15.68 StartZ=0 EndX=27.3747 EndY=15.68 EndZ=0
    g38: LineSegment StartX=27.3747 StartY=15.68 StartZ=0 EndX=34.7704 EndY=8.28427 EndZ=0
    g39: LineSegment StartX=34.7704 StartY=8.28427 StartZ=0 EndX=45.2296 EndY=8.28427 EndZ=0
    g40: LineSegment StartX=45.2296 StartY=8.28427 StartZ=0 EndX=52.6253 EndY=15.68 EndZ=0
    g41: LineSegment StartX=52.6253 StartY=15.68 StartZ=0 EndX=44.065 EndY=15.68 EndZ=0
    g42: LineSegment StartX=44.065 StartY=15.68 StartZ=0 EndX=44.065 EndY=20 EndZ=0
    g43: LineSegment StartX=44.065 StartY=20 StartZ=0 EndX=60 EndY=20 EndZ=0
    g44: LineSegment StartX=60 StartY=20 StartZ=0 EndX=60 EndY=4.065 EndZ=0
    g45: LineSegment StartX=60 StartY=4.065 StartZ=0 EndX=55.68 EndY=4.065 EndZ=0
    g46: LineSegment StartX=55.68 StartY=4.065 StartZ=0 EndX=55.68 EndY=12.6253 EndZ=0
    g47: LineSegment StartX=55.68 StartY=12.6253 StartZ=0 EndX=48.2843 EndY=5.22957 EndZ=0
    g48: LineSegment StartX=48.2843 StartY=5.22957 StartZ=0 EndX=48.2843 EndY=-5.22957 EndZ=0
    g49: LineSegment StartX=48.2843 StartY=-5.22957 StartZ=0 EndX=55.68 EndY=-12.6253 EndZ=0
    g50: LineSegment StartX=55.68 StartY=-12.6253 StartZ=0 EndX=55.68 EndY=-4.065 EndZ=0
    g51: LineSegment StartX=55.68 StartY=-4.065 StartZ=0 EndX=60 EndY=-4.065 EndZ=0
    g52: LineSegment StartX=60 StartY=-4.065 StartZ=0 EndX=60 EndY=-20 EndZ=0
    g53: LineSegment StartX=60 StartY=-20 StartZ=0 EndX=44.065 EndY=-20 EndZ=0
    g54: LineSegment StartX=44.065 StartY=-20 StartZ=0 EndX=44.065 EndY=-15.68 EndZ=0
    g55: LineSegment StartX=44.065 StartY=-15.68 StartZ=0 EndX=52.6253 EndY=-15.68 EndZ=0
    g56: LineSegment StartX=52.6253 StartY=-15.68 StartZ=0 EndX=45.2296 EndY=-8.28427 EndZ=0
    g57: LineSegment StartX=45.2296 StartY=-8.28427 StartZ=0 EndX=34.7704 EndY=-8.28427 EndZ=0
    g58: LineSegment StartX=34.7704 StartY=-8.28427 StartZ=0 EndX=27.3747 EndY=-15.68 EndZ=0
    g59: LineSegment StartX=27.3747 StartY=-15.68 StartZ=0 EndX=35.935 EndY=-15.68 EndZ=0
    g60: LineSegment StartX=35.935 StartY=-15.68 StartZ=0 EndX=35.935 EndY=-20 EndZ=0
    g61: LineSegment StartX=35.935 StartY=-20 StartZ=0 EndX=20 EndY=-20 EndZ=0
    g62: LineSegment StartX=24.32 StartY=12.6253 StartZ=0 EndX=24.32 EndY=4.065 EndZ=0
    g63: LineSegment StartX=24.32 StartY=4.065 StartZ=0 EndX=20 EndY=4.065 EndZ=0
    g64: LineSegment StartX=20 StartY=-4.065 StartZ=0 EndX=24.32 EndY=-4.065 EndZ=0
    g65: LineSegment StartX=24.32 StartY=-4.065 StartZ=0 EndX=24.32 EndY=-12.6253 EndZ=0
    g66: LineSegment StartX=24.32 StartY=-12.6253 StartZ=0 EndX=31.7157 EndY=-5.22957 EndZ=0
    g67: LineSegment StartX=31.7157 StartY=-5.22957 StartZ=0 EndX=31.7157 EndY=5.22957 EndZ=0
    g68: LineSegment StartX=31.7157 StartY=5.22957 StartZ=0 EndX=24.32 EndY=12.6253 EndZ=0
    g69: Circle CenterX=40 CenterY=0 CenterZ=0 NormalX=0 NormalY=0 NormalZ=1 AngleXU=0 Radius=3.405
  constraints (200):
    c: Coincident(g22,g21)
    c: Coincident(g30,g29)
    c: Coincident(g28,g29)
    c: Coincident(g23,g22)
    c: Coincident(g23,g24)
    c: Coincident(g18,g19)
    c: Coincident(g17,g18)
    c: Coincident(g24,g25)
    c: Coincident(g26,g25)
    c: Coincident(g19,g20)
    c: Coincident(g15,g14)
    c: Coincident(g13,g14)
    c: Coincident(g21,g20)
    c: Coincident(g15,g16)
    c: Coincident(g11,g10)
    c: Coincident(g12,g11)
    c: Coincident(g12,g13)
    c: Coincident(g6,g5)
    c: Coincident(g7,g6)
    c: Coincident(g8,g7)
    c: Coincident(g9,g8)
    c: Coincident(g2,g1)
    c: Coincident(g2,g3)
    c: Coincident(g4,g3)
    c: Coincident(g32,g31)
    c: Coincident(g5,g4)
    c: Coincident(g31,g30)
    c: Coincident(g33,g32)
    c: Coincident(g33,g0)
    c: Coincident(g1,g0)
    c: Coincident(g28,g27)
    c: Coincident(g27,g26)
    c: Distance(g9,g0) = 40
    c: Distance(g25,g1) = 40
    c: Tangent(g1,g9)
    c: Tangent(g25,g17)
    c: Tangent(g0,g26)
    c: Horizontal(g1)
    c: Vertical(g0)
    c: Equal(g2,g8)
    c: Equal(g8,g33)
    c: Equal(g33,g27)
    c: Equal(g27,g24)
    c: Equal(g24,g18)
    c: Equal(g18,g16)
    c: Equal(g16,g10)
    c: Vertical(g32)
    c: Vertical(g28)
    c: Vertical(g15)
    c: Vertical(g11)
    c: Vertical(g8)
    c: Vertical(g2)
    c: Vertical(g13)
    c: Vertical(g30)
    c: Horizontal(g33)
    c: Horizontal(g27)
    c: Horizontal(g21)
    c: Horizontal(g17)
    c: Horizontal(g23)
    c: Horizontal(g19)
    c: Horizontal(g7)
    c: Horizontal(g3)
    c: Parallel(g4,g31)
    c: Parallel(g31,g14)
    c: Parallel(g14,g20)
    c: Parallel(g6,g12)
    c: Parallel(g12,g22)
    c: Parallel(g22,g29)
    c: Equal(g21,g22)
    c: Equal(g22,g29)
    c: Equal(g4,g31)
    c: Equal(g6,g12)
    c: Equal(g14,g20)
    c: Angle(g23,g22) = 0.785398
    c: Distance(g8,g2) = 8.13
    c: Distance(g27,g33) = 8.13
    c: Tangent(g33,g10)
    c: Tangent(g16,g27)
    c: Tangent(g2,g24)
    c: Tangent(g8,g18)
    c: Distance(g20,g14) = 4.32
    c: Distance(g12,g6) = 4.32
    c: Distance(g31,g4) = 4.32
    c: Distance(g22,g29) = 4.32
    c: Equal(g30,g13)
    c: Equal(g5,g21)
    c: Equal(g23,g19)
    c: Equal(g32,g28)
    c: Distance(g33,g33) = 4.32
    c: Symmetric(g5,g20,g-1)
    c: Symmetric(g4,g5,g-2)
    c: Equal(g5,g30)
    c: Coincident(g34,g-1)
    c: Diameter(g34) = 6.81
    c: Coincident(g35,g9)
    c: Coincident(g36,g35)
    c: Coincident(g37,g36)
    c: Horizontal(g37)
    c: Coincident(g38,g37)
    c: Coincident(g39,g38)
    c: Horizontal(g39)
    c: Coincident(g41,g40)
    c: Vertical(g44)
    c: Coincident(g45,g44)
    c: Coincident(g48,g47)
    c: Vertical(g48)
    c: Coincident(g49,g48)
    c: Vertical(g50)
    c: Horizontal(g51)
    c: Coincident(g52,g51)
    c: Vertical(g52)
    c: Coincident(g53,g52)
    c: Coincident(g55,g54)
    c: Coincident(g57,g56)
    c: Horizontal(g57)
    c: Coincident(g58,g57)
    c: Coincident(g59,g58)
    c: Horizontal(g59)
    c: Coincident(g61,g60)
    c: Coincident(g61,g17)
    c: Coincident(g63,g10)
    c: Coincident(g64,g16)
    c: Coincident(g65,g64)
    c: Coincident(g66,g65)
    c: Coincident(g67,g66)
    c: Coincident(g68,g67)
    c: Coincident(g68,g62)
    c: PointOnObject(g69,g-1)
    c: Coincident(g43,g42)
    c: Coincident(g43,g44)
    c: Coincident(g41,g42)
    c: Coincident(g39,g40)
    c: Coincident(g46,g47)
    c: Coincident(g46,g45)
    c: Coincident(g50,g51)
    c: Coincident(g49,g50)
    c: Coincident(g54,g53)
    c: Coincident(g56,g55)
    c: Coincident(g59,g60)
    c: Coincident(g62,g63)
    c: Equal(g34,g69)
    c: Equal(g39,g67)
    c: Equal(g67,g57)
    c: Equal(g57,g48)
    c: Equal(g48,g13)
    c: Equal(g38,g68)
    c: Equal(g68,g66)
    c: Equal(g66,g58)
    c: Equal(g58,g56)
    c: Equal(g56,g49)
    c: Equal(g49,g47)
    c: Equal(g47,g40)
    c: Equal(g40,g12)
    c: Equal(g10,g63)
    c: Equal(g16,g64)
    c: Equal(g64,g45)
    c: Equal(g45,g51)
    c: Equal(g51,g42)
    c: Equal(g42,g36)
    c: Equal(g36,g60)
    c: Equal(g60,g54)
    c: Parallel(g47,g40)
    c: Parallel(g38,g68)
    c: Parallel(g66,g58)
    c: Parallel(g49,g56)
    c: Parallel(g56,g68)
    c: Parallel(g40,g66)
    c: Horizontal(g35)
    c: Horizontal(g43)
    c: Horizontal(g45)
    c: Horizontal(g53)
    c: Horizontal(g61)
    c: Horizontal(g64)
    c: Horizontal(g63)
    c: Horizontal(g41)
    c: Vertical(g42)
    c: Vertical(g36)
    c: Vertical(g62)
    c: Vertical(g65)
    c: Vertical(g60)
    c: Vertical(g54)
    c: Vertical(g46)
    c: Horizontal(g55)
    c: Vertical(g67)
    c: Equal(g7,g37)
    c: Equal(g37,g41)
    c: Equal(g41,g46)
    c: Equal(g46,g55)
    c: Equal(g55,g59)
    c: Equal(g59,g65)
    c: Equal(g65,g62)
    c: Equal(g55,g50)
    c: Parallel(g40,g6)
    c: Distance(g9,g44) = 40
    c: DistanceX(g34,g69) = 40
    c: Equal(g35,g43)
    c: Equal(g43,g9)
    c: Equal(g44,g52)
    c: Equal(g53,g61)
    c: Equal(g61,g17)
FEATURE [PartDesign::Pad] Pad004
  Direction = (0,0,1)
  Length = 470
  Length2 = 10
  Profile = -> Sketch005
  ReferenceAxis = -> Sketch005 [N_Axis]
  Refine = true
  Suppressed = false
  Type = 0
FEATURE [PartDesign::Body] Body005  label="8040 extrusion @ 470"
  AllowCompound = false
  Group = -> [Sketch005,Pad004]
  Origin = -> Origin007
  Tip = -> Pad004
FEATURE [Sketcher::SketchObject] Sketch006
  ArcFitTolerance = 1e-06
  AttachmentSupport = -> [XY_Plane008]
  FullyConstrained = true
  MakeInternals = false
  MapMode = 5
  sketch-geometry (37):
    g0: LineSegment StartX=-20 StartY=4.065 StartZ=0 EndX=-20 EndY=20 EndZ=0
    g1: LineSegment StartX=-20 StartY=20 StartZ=0 EndX=-4.065 EndY=20 EndZ=0
    g2: LineSegment StartX=-4.065 StartY=20 StartZ=0 EndX=-4.065 EndY=15.68 EndZ=0
    g3: LineSegment StartX=-4.065 StartY=15.68 StartZ=0 EndX=-12.6253 EndY=15.68 EndZ=0
    g4: LineSegment StartX=-12.6253 StartY=15.68 StartZ=0 EndX=-5.22957 EndY=8.28427 EndZ=0
    g5: LineSegment StartX=-5.22957 StartY=8.28427 StartZ=0 EndX=5.22957 EndY=8.28427 EndZ=0
    g6: LineSegment StartX=5.22957 StartY=8.28427 StartZ=0 EndX=12.6253 EndY=15.68 EndZ=0
    g7: LineSegment StartX=12.6253 StartY=15.68 StartZ=0 EndX=4.065 EndY=15.68 EndZ=0
    g8: LineSegment StartX=4.065 StartY=15.68 StartZ=0 EndX=4.065 EndY=20 EndZ=0
    g9: LineSegment StartX=4.065 StartY=20 StartZ=0 EndX=20 EndY=20 EndZ=0
    g10: LineSegment StartX=20 StartY=20 StartZ=0 EndX=20 EndY=4.065 EndZ=0
    g11: LineSegment StartX=20 StartY=4.065 StartZ=0 EndX=15.68 EndY=4.065 EndZ=0
    g12: LineSegment StartX=15.68 StartY=4.065 StartZ=0 EndX=15.68 EndY=12.6253 EndZ=0
    g13: LineSegment StartX=15.68 StartY=12.6253 StartZ=0 EndX=8.28427 EndY=5.22957 EndZ=0
    g14: LineSegment StartX=8.28427 StartY=5.22957 StartZ=0 EndX=8.28427 EndY=-5.22957 EndZ=0
    g15: LineSegment StartX=8.28427 StartY=-5.22957 StartZ=0 EndX=15.68 EndY=-12.6253 EndZ=0
    g16: LineSegment StartX=15.68 StartY=-12.6253 StartZ=0 EndX=15.68 EndY=-4.065 EndZ=0
    g17: LineSegment StartX=15.68 StartY=-4.065 StartZ=0 EndX=20 EndY=-4.065 EndZ=0
    g18: LineSegment StartX=20 StartY=-4.065 StartZ=0 EndX=20 EndY=-20 EndZ=0
    g19: LineSegment StartX=20 StartY=-20 StartZ=0 EndX=4.065 EndY=-20 EndZ=0
    g20: LineSegment StartX=4.065 StartY=-20 StartZ=0 EndX=4.065 EndY=-15.68 EndZ=0
    g21: LineSegment StartX=4.065 StartY=-15.68 StartZ=0 EndX=12.6253 EndY=-15.68 EndZ=0
    g22: LineSegment StartX=12.6253 StartY=-15.68 StartZ=0 EndX=5.22957 EndY=-8.28427 EndZ=0
    g23: LineSegment StartX=5.22957 StartY=-8.28427 StartZ=0 EndX=-5.22957 EndY=-8.28427 EndZ=0
    g24: LineSegment StartX=-5.22957 StartY=-8.28427 StartZ=0 EndX=-12.6253 EndY=-15.68 EndZ=0
    g25: LineSegment StartX=-12.6253 StartY=-15.68 StartZ=0 EndX=-4.065 EndY=-15.68 EndZ=0
    g26: LineSegment StartX=-4.065 StartY=-15.68 StartZ=0 EndX=-4.065 EndY=-20 EndZ=0
    g27: LineSegment StartX=-4.065 StartY=-20 StartZ=0 EndX=-20 EndY=-20 EndZ=0
    g28: LineSegment StartX=-20 StartY=-20 StartZ=0 EndX=-20 EndY=-4.065 EndZ=0
    g29: LineSegment StartX=-20 StartY=-4.065 StartZ=0 EndX=-15.68 EndY=-4.065 EndZ=0
    g30: LineSegment StartX=-15.68 StartY=-4.065 StartZ=0 EndX=-15.68 EndY=-12.6253 EndZ=0
    g31: LineSegment StartX=-15.68 StartY=-12.6253 StartZ=0 EndX=-8.28427 EndY=-5.22957 EndZ=0
    g32: LineSegment StartX=-8.28427 StartY=-5.22957 StartZ=0 EndX=-8.28427 EndY=5.22957 EndZ=0
    g33: LineSegment StartX=-8.28427 StartY=5.22957 StartZ=0 EndX=-15.68 EndY=12.6253 EndZ=0
    g34: LineSegment StartX=-15.68 StartY=12.6253 StartZ=0 EndX=-15.68 EndY=4.065 EndZ=0
    g35: LineSegment StartX=-15.68 StartY=4.065 StartZ=0 EndX=-20 EndY=4.065 EndZ=0
    g36: Circle CenterX=0 CenterY=0 CenterZ=0 NormalX=0 NormalY=0 NormalZ=1 AngleXU=0 Radius=3.405
  constraints (100):
    c: Coincident(g24,g23)
    c: Coincident(g32,g31)
    c: Coincident(g30,g31)
    c: Coincident(g25,g24)
    c: Coincident(g25,g26)
    c: Coincident(g20,g21)
    c: Coincident(g19,g20)
    c: Coincident(g26,g27)
    c: Coincident(g28,g27)
    c: Coincident(g21,g22)
    c: Coincident(g19,g18)
    c: Coincident(g16,g15)
    c: Coincident(g14,g15)
    c: Coincident(g23,g22)
    c: Coincident(g16,g17)
    c: Coincident(g18,g17)
    c: Coincident(g12,g11)
    c: Coincident(g11,g10)
    c: Coincident(g10,g9)
    c: Coincident(g13,g12)
    c: Coincident(g13,g14)
    c: Coincident(g6,g5)
    c: Coincident(g7,g6)
    c: Coincident(g8,g7)
    c: Coincident(g9,g8)
    c: Coincident(g2,g1)
    c: Coincident(g2,g3)
    c: Coincident(g4,g3)
    c: Coincident(g34,g33)
    c: Coincident(g5,g4)
    c: Coincident(g33,g32)
    c: Coincident(g35,g34)
    c: Coincident(g35,g0)
    c: Coincident(g1,g0)
    c: Coincident(g30,g29)
    c: Coincident(g29,g28)
    c: Distance(g10,g0) = 40
    c: Distance(g27,g1) = 40
    c: Tangent(g1,g9)
    c: Tangent(g27,g19)
    c: Tangent(g0,g28)
    c: Tangent(g10,g18)
    c: Horizontal(g1)
    c: Vertical(g0)
    c: Equal(g2,g8)
    c: Equal(g8,g35)
    c: Equal(g35,g29)
    c: Equal(g29,g26)
    c: Equal(g26,g20)
    c: Equal(g20,g17)
    c: Equal(g17,g11)
    c: Vertical(g34)
    c: Vertical(g30)
    c: Vertical(g16)
    c: Vertical(g18)
    c: Vertical(g12)
    c: Vertical(g8)
    c: Vertical(g2)
    c: Vertical(g14)
    c: Vertical(g32)
    c: Horizontal(g35)
    c: Horizontal(g29)
    c: Horizontal(g23)
    c: Horizontal(g19)
    c: Horizontal(g25)
    c: Horizontal(g21)
    c: Horizontal(g7)
    c: Horizontal(g3)
    c: Parallel(g4,g33)
    c: Parallel(g33,g15)
    c: Parallel(g15,g22)
    c: Parallel(g6,g13)
    c: Parallel(g13,g24)
    c: Parallel(g24,g31)
    c: Equal(g23,g24)
    c: Equal(g24,g31)
    c: Equal(g4,g33)
    c: Equal(g6,g13)
    c: Equal(g15,g22)
    c: Angle(g25,g24) = 0.785398
    c: Distance(g8,g2) = 8.13
    c: Distance(g29,g35) = 8.13
    c: Tangent(g35,g11)
    c: Tangent(g17,g29)
    c: Tangent(g2,g26)
    c: Tangent(g8,g20)
    c: Distance(g22,g15) = 4.32
    c: Distance(g13,g6) = 4.32
    c: Distance(g33,g4) = 4.32
    c: Distance(g24,g31) = 4.32
    c: Equal(g32,g14)
    c: Equal(g5,g23)
    c: Equal(g25,g21)
    c: Equal(g34,g30)
    c: Distance(g35,g35) = 4.32
    c: Symmetric(g5,g22,g-1)
    c: Symmetric(g4,g5,g-2)
    c: Equal(g5,g32)
    c: Coincident(g36,g-1)
    c: Diameter(g36) = 6.81
FEATURE [PartDesign::Pad] Pad005
  Direction = (0,0,1)
  Length = 100
  Length2 = 10
  Profile = -> Sketch006
  ReferenceAxis = -> Sketch006 [N_Axis]
  Refine = true
  Suppressed = false
  Type = 0
FEATURE [PartDesign::Body] Body006  label="4040 extrusion @ 100"
  AllowCompound = false
  Group = -> [Sketch006,Pad005]
  Origin = -> Origin008
  Tip = -> Pad005
FEATURE [Part::Box] Box  label="gusset bracket"
  AttacherType = Attacher::AttachEngine3D
  Height = 35
  Length = 40
  Width = 40
FEATURE [Sketcher::SketchObject] Sketch
  ArcFitTolerance = 1e-06
  AttachmentSupport = -> [Box]
  FullyConstrained = true
  MakeInternals = false
  MapMode = 5
  Placement = pos=(0,0,35) rot=(0,0,1;0rad)
  sketch-geometry (5):
    g0: LineSegment StartX=5 StartY=50 StartZ=0 EndX=5 EndY=35 EndZ=0
    g1: LineSegment StartX=5 StartY=35 StartZ=0 EndX=35 EndY=5 EndZ=0
    g2: LineSegment StartX=35 StartY=5 StartZ=0 EndX=50 EndY=5 EndZ=0
    g3: LineSegment StartX=50 StartY=5 StartZ=0 EndX=50 EndY=50 EndZ=0
    g4: LineSegment StartX=50 StartY=50 StartZ=0 EndX=5 EndY=50 EndZ=0
  constraints (15):
    c: Vertical(g0)
    c: Coincident(g0,g1)
    c: Coincident(g1,g2)
    c: Horizontal(g2)
    c: Coincident(g2,g3)
    c: Vertical(g3)
    c: Coincident(g3,g4)
    c: Coincident(g4,g0)
    c: Horizontal(g4)
    c: Distance(g-2,g0) = 5
    c: Distance(g-1,g2) = 5
    c: DistanceY(g-1,g0) = 35
    c: DistanceX(g-1,g1) = 35
    c: DistanceX(g1,g2) = 15
    c: Distance(g0,g4) = 15
FEATURE [Part::Extrusion] Extrude
  Base = -> Sketch
  Dir = (0,0,1)
  DirMode = 2
  FaceMakerClass = Part::FaceMakerBullseye
  FaceMakerMode = 3
  LengthFwd = 10
  LengthRev = 50
  Solid = true
  Symmetric = false
FEATURE [Part::Cut] Cut
  Base = -> Box
  Tool = -> Extrude
FEATURE [Sketcher::SketchObject] Sketch007
  ArcFitTolerance = 1e-06
  AttachmentSupport = -> [Cut]
  FullyConstrained = true
  MakeInternals = false
  MapMode = 5
  Placement = pos=(0,40,0) rot=(0,0.707107,0.707107;3.14159rad)
  sketch-geometry (4):
    g0: LineSegment StartX=-3 StartY=32 StartZ=0 EndX=-60 EndY=32 EndZ=0
    g1: LineSegment StartX=-60 StartY=32 StartZ=0 EndX=-60 EndY=3 EndZ=0
    g2: LineSegment StartX=-60 StartY=3 StartZ=0 EndX=-3 EndY=3 EndZ=0
    g3: LineSegment StartX=-3 StartY=3 StartZ=0 EndX=-3 EndY=32 EndZ=0
  constraints (12):
    c: Coincident(g0,g1)
    c: Coincident(g1,g2)
    c: Coincident(g2,g3)
    c: Coincident(g3,g0)
    c: Horizontal(g0)
    c: Horizontal(g2)
    c: Vertical(g1)
    c: Vertical(g3)
    c: Distance(g-1,g2) = 3
    c: Distance(g-1,g0) = 32
    c: Distance(g-2,g3) = 3
    c: Distance(g-2,g1) = 60
FEATURE [Part::Extrusion] Extrude001
  Base = -> Sketch007
  Dir = (0,1,-2e-16)
  DirMode = 2
  FaceMakerClass = Part::FaceMakerBullseye
  FaceMakerMode = 3
  LengthFwd = 5
  LengthRev = 37
  Solid = true
  Symmetric = false
FEATURE [Part::Cut] Cut001
  Base = -> Cut
  Tool = -> Extrude001
FEATURE [Sketcher::SketchObject] Sketch008
  ArcFitTolerance = 1e-06
  AttachmentSupport = -> [Cut001]
  FullyConstrained = true
  MakeInternals = false
  MapMode = 5
  Placement = pos=(0,0,0) rot=(0.57735,-0.57735,-0.57735;2.0944rad)
  sketch-geometry (4):
    g0: ArcOfCircle CenterX=-12.5 CenterY=17.5 CenterZ=0 NormalX=0 NormalY=0 NormalZ=1 AngleXU=0 Radius=4.5 StartAngle=4.71239 EndAngle=7.85398
    g1: ArcOfCircle CenterX=-27.5 CenterY=17.5 CenterZ=0 NormalX=0 NormalY=0 NormalZ=1 AngleXU=0 Radius=4.5 StartAngle=1.5708 EndAngle=4.71239
    g2: LineSegment StartX=-12.5 StartY=13 StartZ=0 EndX=-27.5 EndY=13 EndZ=0
    g3: LineSegment StartX=-12.5 StartY=22 StartZ=0 EndX=-27.5 EndY=22 EndZ=0
  constraints (10):
    c: Tangent(g0,g2) = 1.5708
    c: Tangent(g0,g3) = -1.5708
    c: Tangent(g1,g2) = 1.5708
    c: Tangent(g1,g3) = -1.5708
    c: Equal(g0,g1)
    c: Horizontal(g2)
    c: DistanceX(g1,g0) = 15
    c: Distance(g2,g3) = 9
    c: Distance(g0,g-1) = 13
    c: Distance(g0,g-2) = 8
FEATURE [Part::Extrusion] Extrude002
  Base = -> Sketch008
  Dir = (-1,0,0)
  DirMode = 2
  FaceMakerClass = Part::FaceMakerBullseye
  FaceMakerMode = 3
  LengthFwd = 10
  LengthRev = 10
  Solid = true
  Symmetric = false
FEATURE [Part::Cut] Cut002
  Base = -> Cut001
  Tool = -> Extrude002
FEATURE [Sketcher::SketchObject] Sketch009
  ArcFitTolerance = 1e-06
  AttachmentSupport = -> [Cut002]
  FullyConstrained = true
  MakeInternals = false
  MapMode = 5
  Placement = pos=(0,0,0) rot=(1,0,0;1.5708rad)
  sketch-geometry (4):
    g0: ArcOfCircle CenterX=12.5 CenterY=17.5 CenterZ=0 NormalX=0 NormalY=0 NormalZ=1 AngleXU=0 Radius=4.5 StartAngle=1.5708 EndAngle=4.71239
    g1: ArcOfCircle CenterX=27.5 CenterY=17.5 CenterZ=0 NormalX=0 NormalY=0 NormalZ=1 AngleXU=0 Radius=4.5 StartAngle=4.71239 EndAngle=7.85398
    g2: LineSegment StartX=12.5 StartY=22 StartZ=0 EndX=27.5 EndY=22 EndZ=0
    g3: LineSegment StartX=12.5 StartY=13 StartZ=0 EndX=27.5 EndY=13 EndZ=0
  constraints (10):
    c: Tangent(g0,g2) = 1.5708
    c: Tangent(g0,g3) = -1.5708
    c: Tangent(g1,g2) = 1.5708
    c: Tangent(g1,g3) = -1.5708
    c: Equal(g0,g1)
    c: Horizontal(g2)
    c: Distance(g3,g2) = 9
    c: DistanceX(g0,g1) = 15
    c: Distance(g0,g-2) = 8
    c: Distance(g-1,g3) = 13
FEATURE [Part::Extrusion] Extrude003
  Base = -> Sketch009
  Dir = (0,-1,2e-16)
  DirMode = 2
  FaceMakerClass = Part::FaceMakerBullseye
  FaceMakerMode = 3
  LengthFwd = 10
  LengthRev = 10
  Solid = true
  Symmetric = false
FEATURE [Part::Cut] Cut003  label="corner gusset"
  Base = -> Cut002
  Tool = -> Extrude003
FEATURE [Sketcher::SketchObject] Sketch010
  ArcFitTolerance = 1e-06
  AttachmentSupport = -> [XY_Plane]
  FullyConstrained = true
  MakeInternals = false
  MapMode = 5
  sketch-geometry (10):
    g0: LineSegment StartX=-10 StartY=0 StartZ=0 EndX=10 EndY=0 EndZ=0
    g1: LineSegment StartX=10 StartY=0 StartZ=0 EndX=10 EndY=8.5 EndZ=0
    g2: LineSegment StartX=-10 StartY=0 StartZ=0 EndX=-10 EndY=8.5 EndZ=0
    g3: LineSegment StartX=-10 StartY=14.5 StartZ=0 EndX=-10 EndY=17.7218 EndZ=0
    g4: LineSegment StartX=-10 StartY=17.7218 StartZ=0 EndX=-7.72183 EndY=20 EndZ=0
    g5: LineSegment StartX=-7.72183 StartY=20 StartZ=0 EndX=7.72183 EndY=20 EndZ=0
    g6: LineSegment StartX=7.72183 StartY=20 StartZ=0 EndX=10 EndY=17.7218 EndZ=0
    g7: LineSegment StartX=10 StartY=17.7218 StartZ=0 EndX=10 EndY=14.5 EndZ=0
    g8: ArcOfCircle CenterX=-10 CenterY=11.5 CenterZ=0 NormalX=0 NormalY=0 NormalZ=1 AngleXU=0 Radius=3 StartAngle=4.71239 EndAngle=7.85398
    g9: ArcOfCircle CenterX=9.99998 CenterY=11.5 CenterZ=0 NormalX=0 NormalY=0 NormalZ=1 AngleXU=0 Radius=3 StartAngle=1.57079 EndAngle=4.7124
  constraints (30):
    c: Coincident(g1,g0)
    c: Coincident(g2,g0)
    c: Coincident(g4,g3)
    c: Coincident(g5,g4)
    c: Horizontal(g5)
    c: Coincident(g6,g5)
    c: Coincident(g7,g6)
    c: Vertical(g7)
    c: Coincident(g8,g3)
    c: Coincident(g8,g2)
    c: Coincident(g9,g1)
    c: Coincident(g9,g7)
    c: Equal(g8,g9)
    c: Equal(g1,g2)
    c: Equal(g3,g7)
    c: Equal(g6,g4)
    c: Distance(g0,g0) = 20
    c: Symmetric(g0,g0,g-2)
    c: Vertical(g2)
    c: Vertical(g1)
    c: Tangent(g3,g2)
    c: PointOnObject(g7,g1)
    c: Radius(g8) = 3
    c: Angle(g4,g3) = 0.785398
    c: Angle(g6,g7) = 2.35619
    c: Distance(g0,g5) = 20
    c: PointOnObject(g8,g3)
    c: Distance(g8,g5) = 8.5
    c: PointOnObject(g-1,g0)
    c: Equal(g4,g3)
FEATURE [PartDesign::Pad] Pad006
  Direction = (0,0,1)
  Length = 500
  Length2 = 10
  Profile = -> Sketch010
  ReferenceAxis = -> Sketch010 [N_Axis]
  Refine = true
  Suppressed = false
  Type = 0
FEATURE [PartDesign::Body] Body  label="HGR20x500"
  AllowCompound = false
  Group = -> [Sketch010,Pad006]
  Origin = -> Origin
  Tip = -> Pad006
FEATURE [Sketcher::SketchObject] Sketch011
  ArcFitTolerance = 1e-06
  AttachmentSupport = -> [XY_Plane009]
  FullyConstrained = true
  MakeInternals = false
  MapMode = 5
  sketch-geometry (14):
    g0: LineSegment StartX=10 StartY=0 StartZ=0 EndX=10 EndY=3.9 EndZ=0
    g1: LineSegment StartX=-10 StartY=0 StartZ=0 EndX=-10 EndY=3.9 EndZ=0
    g2: LineSegment StartX=-10 StartY=9.9 StartZ=0 EndX=-10 EndY=13.1218 EndZ=0
    g3: LineSegment StartX=-10 StartY=13.1218 StartZ=0 EndX=-7.72183 EndY=15.4 EndZ=0
    g4: LineSegment StartX=-7.72183 StartY=15.4 StartZ=0 EndX=7.72183 EndY=15.4 EndZ=0
    g5: LineSegment StartX=7.72183 StartY=15.4 StartZ=0 EndX=10 EndY=13.1218 EndZ=0
    g6: LineSegment StartX=10 StartY=13.1218 StartZ=0 EndX=10 EndY=9.9 EndZ=0
    g7: ArcOfCircle CenterX=-10 CenterY=6.9 CenterZ=0 NormalX=0 NormalY=0 NormalZ=1 AngleXU=0 Radius=3 StartAngle=4.71239 EndAngle=7.85398
    g8: ArcOfCircle CenterX=10 CenterY=6.9 CenterZ=0 NormalX=0 NormalY=0 NormalZ=1 AngleXU=0 Radius=3 StartAngle=1.5708 EndAngle=4.71238
    g9: LineSegment StartX=-21 StartY=0 StartZ=0 EndX=-21 EndY=25.4 EndZ=0
    g10: LineSegment StartX=-21 StartY=25.4 StartZ=0 EndX=21 EndY=25.4 EndZ=0
    g11: LineSegment StartX=21 StartY=25.4 StartZ=0 EndX=21 EndY=0 EndZ=0
    g12: LineSegment StartX=21 StartY=0 StartZ=0 EndX=10 EndY=0 EndZ=0
    g13: LineSegment StartX=-21 StartY=0 StartZ=0 EndX=-10 EndY=0 EndZ=0
  constraints (42):
    c: Coincident(g3,g2)
    c: Coincident(g4,g3)
    c: Horizontal(g4)
    c: Coincident(g5,g4)
    c: Coincident(g6,g5)
    c: Vertical(g6)
    c: Coincident(g7,g2)
    c: Coincident(g7,g1)
    c: Coincident(g8,g0)
    c: Coincident(g8,g6)
    c: Equal(g7,g8)
    c: Equal(g0,g1)
    c: Equal(g2,g6)
    c: Equal(g5,g3)
    c: Distance(g1,g0) = 20
    c: Symmetric(g1,g0,g-2)
    c: Vertical(g1)
    c: Vertical(g0)
    c: Tangent(g2,g1)
    c: PointOnObject(g6,g0)
    c: Radius(g7) = 3
    c: Angle(g3,g2) = 0.785398
    c: Angle(g5,g6) = 2.35619
    c: PointOnObject(g7,g2)
    c: Distance(g7,g4) = 8.5
    c: Equal(g3,g2)
    c: Vertical(g9)
    c: Coincident(g10,g9)
    c: Horizontal(g10)
    c: Coincident(g11,g10)
    c: PointOnObject(g11,g-1)
    c: Vertical(g11)
    c: Coincident(g12,g11)
    c: DistanceX(g10,g10) = 42
    c: Coincident(g12,g0)
    c: DistanceY(g9,g9) = 25.4
    c: Coincident(g13,g9)
    c: Coincident(g13,g1)
    c: Horizontal(g13)
    c: Equal(g13,g12)
    c: Horizontal(g12)
    c: Distance(g10,g4) = 10
FEATURE [PartDesign::Pad] Pad007
  Direction = (0,0,1)
  Length = 73
  Length2 = 10
  Profile = -> Sketch011
  ReferenceAxis = -> Sketch011 [N_Axis]
  Refine = true
  Suppressed = false
  Type = 0
FEATURE [Sketcher::SketchObject] Sketch012
  ArcFitTolerance = 1e-06
  AttachmentSupport = -> [Pad007]
  FullyConstrained = true
  MakeInternals = false
  MapMode = 5
  Placement = pos=(0,25.4,0) rot=(0,0.707107,0.707107;3.14159rad)
  sketch-geometry (8):
    g0: Circle CenterX=-16 CenterY=54.5 CenterZ=0 NormalX=0 NormalY=0 NormalZ=1 AngleXU=0 Radius=2.5
    g1: Circle CenterX=16 CenterY=54.5 CenterZ=0 NormalX=0 NormalY=0 NormalZ=1 AngleXU=0 Radius=2.5
    g2: Circle CenterX=-16 CenterY=18.5 CenterZ=0 NormalX=0 NormalY=0 NormalZ=1 AngleXU=0 Radius=2.5
    g3: Circle CenterX=16 CenterY=18.5 CenterZ=0 NormalX=0 NormalY=0 NormalZ=1 AngleXU=0 Radius=2.5
    g4: LineSegment [constr] StartX=-16 StartY=54.5 StartZ=0 EndX=16 EndY=54.5 EndZ=0
    g5: LineSegment [constr] StartX=-16 StartY=18.5 StartZ=0 EndX=16 EndY=18.5 EndZ=0
    g6: LineSegment [constr] StartX=16 StartY=54.5 StartZ=0 EndX=16 EndY=18.5 EndZ=0
    g7: LineSegment [constr] StartX=-16 StartY=54.5 StartZ=0 EndX=-16 EndY=18.5 EndZ=0
  constraints (19):
    c: Equal(g1,g0)
    c: Equal(g0,g3)
    c: Equal(g3,g2)
    c: Diameter(g0) = 5
    c: DistanceY(g3,g1) = 36
    c: Coincident(g4,g0)
    c: Coincident(g4,g1)
    c: Coincident(g5,g2)
    c: Coincident(g5,g3)
    c: Horizontal(g5)
    c: Coincident(g6,g1)
    c: Coincident(g6,g3)
    c: Vertical(g6)
    c: Coincident(g7,g0)
    c: Coincident(g7,g2)
    c: Vertical(g7)
    c: DistanceX(g4,g4) = 32
    c: Symmetric(g0,g1,g-2)
    c: Distance(g-1,g5) = 18.5
FEATURE [Sketcher::SketchObject] Sketch013
  ArcFitTolerance = 1e-06
  AttachmentSupport = -> [XY_Plane010]
  FullyConstrained = false
  MakeInternals = false
  MapMode = 5
  sketch-geometry (28):
    g0: LineSegment StartX=-100 StartY=120 StartZ=0 EndX=-100 EndY=-120 EndZ=0
    g1: LineSegment StartX=-100 StartY=-120 StartZ=0 EndX=100 EndY=-120 EndZ=0
    g2: LineSegment StartX=100 StartY=-120 StartZ=0 EndX=100 EndY=120 EndZ=0
    g3: LineSegment StartX=100 StartY=120 StartZ=0 EndX=-100 EndY=120 EndZ=0
    g4: Circle CenterX=-76.9092 CenterY=96 CenterZ=0 NormalX=0 NormalY=0 NormalZ=1 AngleXU=0 Radius=2.5
    g5: Circle CenterX=-40.9092 CenterY=96 CenterZ=0 NormalX=0 NormalY=0 NormalZ=1 AngleXU=0 Radius=2.5
    g6: Circle CenterX=-76.9092 CenterY=64 CenterZ=0 NormalX=0 NormalY=0 NormalZ=1 AngleXU=0 Radius=2.5
    g7: Circle CenterX=-40.9092 CenterY=64 CenterZ=0 NormalX=0 NormalY=0 NormalZ=1 AngleXU=0 Radius=2.5
    g8: Circle CenterX=-76.9092 CenterY=-64 CenterZ=0 NormalX=0 NormalY=0 NormalZ=1 AngleXU=0 Radius=2.5
    g9: Circle CenterX=-40.9092 CenterY=-64 CenterZ=0 NormalX=0 NormalY=0 NormalZ=1 AngleXU=0 Radius=2.5
    g10: Circle CenterX=-76.9092 CenterY=-96 CenterZ=0 NormalX=0 NormalY=0 NormalZ=1 AngleXU=0 Radius=2.5
    g11: Circle CenterX=-40.9092 CenterY=-96 CenterZ=0 NormalX=0 NormalY=0 NormalZ=1 AngleXU=0 Radius=2.5
    g12: Circle CenterX=40.9092 CenterY=96 CenterZ=0 NormalX=0 NormalY=0 NormalZ=1 AngleXU=0 Radius=2.5
    g13: Circle CenterX=76.9092 CenterY=96 CenterZ=0 NormalX=0 NormalY=0 NormalZ=1 AngleXU=0 Radius=2.5
    g14: Circle CenterX=40.9092 CenterY=64 CenterZ=0 NormalX=0 NormalY=0 NormalZ=1 AngleXU=0 Radius=2.5
    g15: Circle CenterX=76.9092 CenterY=64 CenterZ=0 NormalX=0 NormalY=0 NormalZ=1 AngleXU=0 Radius=2.5
    g16: Circle CenterX=40.9092 CenterY=-64 CenterZ=0 NormalX=0 NormalY=0 NormalZ=1 AngleXU=0 Radius=2.5
    g17: Circle CenterX=76.9092 CenterY=-64 CenterZ=0 NormalX=0 NormalY=0 NormalZ=1 AngleXU=0 Radius=2.5
    g18: Circle CenterX=40.9092 CenterY=-96 CenterZ=0 NormalX=0 NormalY=0 NormalZ=1 AngleXU=0 Radius=2.5
    g19: Circle CenterX=76.9092 CenterY=-96 CenterZ=0 NormalX=0 NormalY=0 NormalZ=1 AngleXU=0 Radius=2.5
    g20: LineSegment [constr] StartX=-76.9092 StartY=96 StartZ=0 EndX=76.9092 EndY=96 EndZ=0
    g21: LineSegment [constr] StartX=76.9092 StartY=96 StartZ=0 EndX=76.9092 EndY=-96 EndZ=0
    g22: LineSegment [constr] StartX=76.9092 StartY=-96 StartZ=0 EndX=-76.9092 EndY=-96 EndZ=0
    g23: LineSegment [constr] StartX=-76.9092 StartY=-96 StartZ=0 EndX=-76.9092 EndY=96 EndZ=0
    g24: LineSegment [constr] StartX=-76.9092 StartY=64 StartZ=0 EndX=76.9092 EndY=64 EndZ=0
    g25: LineSegment [constr] StartX=-76.9092 StartY=-64 StartZ=0 EndX=76.9092 EndY=-64 EndZ=0
    g26: LineSegment [constr] StartX=40.9092 StartY=96 StartZ=0 EndX=40.9092 EndY=-96 EndZ=0
    g27: LineSegment [constr] StartX=-40.9092 StartY=-96 StartZ=0 EndX=-40.9092 EndY=96 EndZ=0
  constraints (71):
    c: Coincident(g0,g1)
    c: Coincident(g1,g2)
    c: Coincident(g2,g3)
    c: Coincident(g3,g0)
    c: Vertical(g2)
    c: Horizontal(g1)
    c: Equal(g17,g16)
    c: Equal(g16,g18)
    c: Equal(g18,g19)
    c: Equal(g19,g14)
    c: Equal(g14,g15)
    c: Equal(g15,g13)
    c: Equal(g13,g12)
    c: Equal(g12,g5)
    c: Equal(g5,g4)
    c: Equal(g4,g6)
    c: Equal(g6,g7)
    c: Equal(g7,g8)
    c: Equal(g8,g9)
    c: Equal(g9,g11)
    c: Equal(g11,g10)
    c: Diameter(g4) = 5
    c: Coincident(g20,g4)
    c: Coincident(g20,g13)
    c: Coincident(g21,g13)
    c: Coincident(g21,g19)
    c: Coincident(g22,g19)
    c: Coincident(g22,g10)
    c: Coincident(g23,g10)
    c: Coincident(g23,g4)
    c: PointOnObject(g6,g23)
    c: PointOnObject(g8,g23)
    c: PointOnObject(g11,g22)
    c: PointOnObject(g18,g22)
    c: PointOnObject(g17,g21)
    c: PointOnObject(g15,g21)
    c: PointOnObject(g12,g20)
    c: PointOnObject(g5,g20)
    c: Vertical(g21)
    c: Horizontal(g22)
    c: Coincident(g24,g6)
    c: Horizontal(g24)
    c: Coincident(g25,g8)
    c: Coincident(g25,g17)
    c: Coincident(g26,g12)
    c: Coincident(g26,g18)
    c: Vertical(g26)
    c: Coincident(g27,g11)
    c: Coincident(g27,g5)
    c: Vertical(g27)
    c: Horizontal(g25)
    c: PointOnObject(g9,g25)
    c: PointOnObject(g9,g27)
    c: PointOnObject(g7,g24)
    c: PointOnObject(g7,g27)
    c: PointOnObject(g14,g24)
    c: PointOnObject(g14,g26)
    c: Coincident(g15,g24)
    c: PointOnObject(g16,g26)
    c: PointOnObject(g16,g25)
    c: Distance(g24,g20) = 32
    c: Distance(g25,g22) = 32
    c: Distance(g27,g23) = 36
    c: Distance(g21,g26) = 36
    c: Distance(g1,g3) = 240
    c: Distance(g2,g0) = 200
    c: Symmetric(g5,g12,g-2)
    c: Symmetric(g10,g4,g-1)
    c: Symmetric(g0,g0,g-1)
    c: Symmetric(g0,g2,g-2)
    c: DistanceY(g9,g5) = 160
FEATURE [PartDesign::Pad] Pad008
  Direction = (0,0,1)
  Length = 10
  Length2 = 10
  Profile = -> Sketch013
  ReferenceAxis = -> Sketch013 [N_Axis]
  Refine = true
  Suppressed = false
  Type = 0
FEATURE [PartDesign::Body] Body008  label="XY gantry plate"
  AllowCompound = false
  Group = -> [Sketch013,Pad008]
  Origin = -> Origin010
  Tip = -> Pad008
FEATURE [PartDesign::Pocket] Pocket
  BaseFeature = -> Pad007
  Direction = (0,-1,2e-16)
  Length = 5
  Length2 = 5
  Profile = -> Sketch012
  ReferenceAxis = -> Sketch012 [N_Axis]
  Refine = true
  Suppressed = false
  Type = 0
FEATURE [PartDesign::Body] Body007  label="HGR20 carriage"
  AllowCompound = false
  Group = -> [Sketch011,Pad007,Sketch012,Pocket]
  Origin = -> Origin009
  Tip = -> Pocket
FEATURE [Part::Box] Box001  label="gusset bracket001"
  AttacherType = Attacher::AttachEngine3D
  Height = 35
  Length = 40
  Width = 40
FEATURE [Sketcher::SketchObject] Sketch014
  ArcFitTolerance = 1e-06
  AttachmentSupport = -> [Box001]
  FullyConstrained = true
  MakeInternals = false
  MapMode = 5
  Placement = pos=(0,0,35) rot=(0,0,1;0rad)
  sketch-geometry (5):
    g0: LineSegment StartX=5 StartY=50 StartZ=0 EndX=5 EndY=35 EndZ=0
    g1: LineSegment StartX=5 StartY=35 StartZ=0 EndX=35 EndY=5 EndZ=0
    g2: LineSegment StartX=35 StartY=5 StartZ=0 EndX=50 EndY=5 EndZ=0
    g3: LineSegment StartX=50 StartY=5 StartZ=0 EndX=50 EndY=50 EndZ=0
    g4: LineSegment StartX=50 StartY=50 StartZ=0 EndX=5 EndY=50 EndZ=0
  constraints (15):
    c: Vertical(g0)
    c: Coincident(g0,g1)
    c: Coincident(g1,g2)
    c: Horizontal(g2)
    c: Coincident(g2,g3)
    c: Vertical(g3)
    c: Coincident(g3,g4)
    c: Coincident(g4,g0)
    c: Horizontal(g4)
    c: Distance(g-2,g0) = 5
    c: Distance(g-1,g2) = 5
    c: DistanceY(g-1,g0) = 35
    c: DistanceX(g-1,g1) = 35
    c: DistanceX(g1,g2) = 15
    c: Distance(g0,g4) = 15
FEATURE [Part::Extrusion] Extrude004
  Base = -> Sketch014
  Dir = (0,0,1)
  DirMode = 2
  FaceMakerClass = Part::FaceMakerBullseye
  FaceMakerMode = 3
  LengthFwd = 10
  LengthRev = 50
  Solid = true
  Symmetric = false
FEATURE [Part::Cut] Cut004
  Base = -> Box001
  Tool = -> Extrude004
FEATURE [Sketcher::SketchObject] Sketch021
  ArcFitTolerance = 1e-06
  AttachmentSupport = -> [Cut004]
  FullyConstrained = true
  MakeInternals = false
  MapMode = 5
  Placement = pos=(0,40,0) rot=(0,0.707107,0.707107;3.14159rad)
  sketch-geometry (4):
    g0: LineSegment StartX=-3 StartY=32 StartZ=0 EndX=-60 EndY=32 EndZ=0
    g1: LineSegment StartX=-60 StartY=32 StartZ=0 EndX=-60 EndY=3 EndZ=0
    g2: LineSegment StartX=-60 StartY=3 StartZ=0 EndX=-3 EndY=3 EndZ=0
    g3: LineSegment StartX=-3 StartY=3 StartZ=0 EndX=-3 EndY=32 EndZ=0
  constraints (12):
    c: Coincident(g0,g1)
    c: Coincident(g1,g2)
    c: Coincident(g2,g3)
    c: Coincident(g3,g0)
    c: Horizontal(g0)
    c: Horizontal(g2)
    c: Vertical(g1)
    c: Vertical(g3)
    c: Distance(g-1,g2) = 3
    c: Distance(g-1,g0) = 32
    c: Distance(g-2,g3) = 3
    c: Distance(g-2,g1) = 60
FEATURE [Part::Extrusion] Extrude005
  Base = -> Sketch021
  Dir = (0,1,-2e-16)
  DirMode = 2
  FaceMakerClass = Part::FaceMakerBullseye
  FaceMakerMode = 3
  LengthFwd = 5
  LengthRev = 37
  Solid = true
  Symmetric = false
FEATURE [Part::Cut] Cut005
  Base = -> Cut004
  Tool = -> Extrude005
FEATURE [Sketcher::SketchObject] Sketch022
  ArcFitTolerance = 1e-06
  AttachmentSupport = -> [Cut005]
  FullyConstrained = true
  MakeInternals = false
  MapMode = 5
  Placement = pos=(0,0,0) rot=(0.57735,-0.57735,-0.57735;2.0944rad)
  sketch-geometry (4):
    g0: ArcOfCircle CenterX=-12.5 CenterY=17.5 CenterZ=0 NormalX=0 NormalY=0 NormalZ=1 AngleXU=0 Radius=4.5 StartAngle=4.71239 EndAngle=7.85398
    g1: ArcOfCircle CenterX=-27.5 CenterY=17.5 CenterZ=0 NormalX=0 NormalY=0 NormalZ=1 AngleXU=0 Radius=4.5 StartAngle=1.5708 EndAngle=4.71239
    g2: LineSegment StartX=-12.5 StartY=13 StartZ=0 EndX=-27.5 EndY=13 EndZ=0
    g3: LineSegment StartX=-12.5 StartY=22 StartZ=0 EndX=-27.5 EndY=22 EndZ=0
  constraints (10):
    c: Tangent(g0,g2) = 1.5708
    c: Tangent(g0,g3) = -1.5708
    c: Tangent(g1,g2) = 1.5708
    c: Tangent(g1,g3) = -1.5708
    c: Equal(g0,g1)
    c: Horizontal(g2)
    c: DistanceX(g1,g0) = 15
    c: Distance(g2,g3) = 9
    c: Distance(g0,g-1) = 13
    c: Distance(g0,g-2) = 8
FEATURE [Part::Extrusion] Extrude006
  Base = -> Sketch022
  Dir = (-1,0,0)
  DirMode = 2
  FaceMakerClass = Part::FaceMakerBullseye
  FaceMakerMode = 3
  LengthFwd = 10
  LengthRev = 10
  Solid = true
  Symmetric = false
FEATURE [Part::Cut] Cut006
  Base = -> Cut005
  Tool = -> Extrude006
FEATURE [Sketcher::SketchObject] Sketch023
  ArcFitTolerance = 1e-06
  AttachmentSupport = -> [Cut006]
  FullyConstrained = true
  MakeInternals = false
  MapMode = 5
  Placement = pos=(0,0,0) rot=(1,0,0;1.5708rad)
  sketch-geometry (4):
    g0: ArcOfCircle CenterX=12.5 CenterY=17.5 CenterZ=0 NormalX=0 NormalY=0 NormalZ=1 AngleXU=0 Radius=4.5 StartAngle=1.5708 EndAngle=4.71239
    g1: ArcOfCircle CenterX=27.5 CenterY=17.5 CenterZ=0 NormalX=0 NormalY=0 NormalZ=1 AngleXU=0 Radius=4.5 StartAngle=4.71239 EndAngle=7.85398
    g2: LineSegment StartX=12.5 StartY=22 StartZ=0 EndX=27.5 EndY=22 EndZ=0
    g3: LineSegment StartX=12.5 StartY=13 StartZ=0 EndX=27.5 EndY=13 EndZ=0
  constraints (10):
    c: Tangent(g0,g2) = 1.5708
    c: Tangent(g0,g3) = -1.5708
    c: Tangent(g1,g2) = 1.5708
    c: Tangent(g1,g3) = -1.5708
    c: Equal(g0,g1)
    c: Horizontal(g2)
    c: Distance(g3,g2) = 9
    c: DistanceX(g0,g1) = 15
    c: Distance(g0,g-2) = 8
    c: Distance(g-1,g3) = 13
FEATURE [Part::Extrusion] Extrude007
  Base = -> Sketch023
  Dir = (0,-1,2e-16)
  DirMode = 2
  FaceMakerClass = Part::FaceMakerBullseye
  FaceMakerMode = 3
  LengthFwd = 10
  LengthRev = 10
  Solid = true
  Symmetric = false
FEATURE [Part::Cut] Cut007  label="corner gusset037"
  Base = -> Cut006
  Tool = -> Extrude007
FEATURE [App::Link] _040_extrusion___610  label="4040 extrusion @ 615"
  LinkPlacement = pos=(243.598,420.363,448.333) rot=(0,-1,0;1.5708rad)
  LinkedObject = -> Body001
  Placement = pos=(243.598,420.363,448.333) rot=(0,-1,0;1.5708rad)
FEATURE [App::FeaturePython] GroundedJoint  # Assembly grounded joint (typed FeaturePython)
  ObjectToGround = -> _040_extrusion___610
  Placement = pos=(243.598,420.363,448.333) rot=(0,-1,0;1.5708rad)
FEATURE [App::Link] _040_extrusion___530  label="4040 extrusion @ 616"
  LinkPlacement = pos=(223.598,970.363,448.333) rot=(1,0,0;1.5708rad)
  LinkedObject = -> Body002
  Placement = pos=(223.598,970.363,448.333) rot=(1,0,0;1.5708rad)
FEATURE [App::FeaturePython] Joint  label="Fixed"  # Assembly joint (typed FeaturePython)
  Activated = true
  AngleMax = 0
  AngleMin = 0
  Detach1 = false
  Detach2 = false
  Distance = 0
  Distance2 = 0
  EnableAngleMax = false
  EnableAngleMin = false
  EnableLengthMax = false
  EnableLengthMin = false
  JointType = 0 (Fixed)
  LengthMax = 0
  LengthMin = 0
  Offset2 = pos=(0,0,0) rot=(0,0,-1;1.5708rad)
  Placement1 = pos=(20,12.0325,530) rot=(-0.57735,-0.57735,0.57735;4.18879rad)
  Placement2 = pos=(12.0325,20,0) rot=(0.57735,0.57735,0.57735;2.0944rad)
  Reference1 = -> Assembly [_040_extrusion___530.Edge34,_040_extrusion___530.Edge34]
  Reference2 = -> Assembly [_040_extrusion___610.Edge30,_040_extrusion___610.Edge30]
FEATURE [App::Link] _040_extrusion___611  label="4040 extrusion @ 617"
  LinkPlacement = pos=(-346.402,970.363,448.333) rot=(1,0,0;1.5708rad)
  LinkedObject = -> Body002
  Placement = pos=(-346.402,970.363,448.333) rot=(1,0,0;1.5708rad)
FEATURE [App::FeaturePython] Joint001  label="Fixed001"  # Assembly joint (typed FeaturePython)
  Activated = true
  AngleMax = 0
  AngleMin = 0
  Detach1 = false
  Detach2 = false
  Distance = 0
  Distance2 = 0
  EnableAngleMax = false
  EnableAngleMin = false
  EnableLengthMax = false
  EnableLengthMin = false
  JointType = 0 (Fixed)
  LengthMax = 0
  LengthMin = 0
  Offset2 = pos=(0,0,0) rot=(0,0,-1;1.5708rad)
  Placement1 = pos=(12.0325,20,610) rot=(0.707107,0,0.707107;3.14159rad)
  Placement2 = pos=(-20,12.0325,530) rot=(0,0.707107,0.707107;3.14159rad)
  Reference1 = -> Assembly [_040_extrusion___610.Edge31,_040_extrusion___610.Edge31]
  Reference2 = -> Assembly [_040_extrusion___611.Edge4,_040_extrusion___611.Edge4]
FEATURE [App::Link] _040_extrusion___612  label="4040 extrusion @ 618"
  LinkPlacement = pos=(243.598,990.363,448.333) rot=(0,1,0;4.71239rad)
  LinkedObject = -> Body001
  Placement = pos=(243.598,990.363,448.333) rot=(0,1,0;4.71239rad)
FEATURE [App::FeaturePython] Joint002  label="Fixed002"  # Assembly joint (typed FeaturePython)
  Activated = true
  AngleMax = 0
  AngleMin = 0
  Detach1 = false
  Detach2 = false
  Distance = 0
  Distance2 = 0
  EnableAngleMax = false
  EnableAngleMin = false
  EnableLengthMax = false
  EnableLengthMin = false
  JointType = 0 (Fixed)
  LengthMax = 0
  LengthMin = 0
  Offset2 = pos=(0,0,0) rot=(0,0,-1;1.5708rad)
  Placement1 = pos=(20,12.0325,0) rot=(-0.57735,-0.57735,0.57735;4.18879rad)
  Placement2 = pos=(12.0325,-20,0) rot=(-0.57735,-0.57735,0.57735;2.0944rad)
  Reference1 = -> Assembly [_040_extrusion___530.Edge33,_040_extrusion___530.Edge33]
  Reference2 = -> Assembly [_040_extrusion___612.Edge60,_040_extrusion___612.Edge60]
FEATURE [App::Link] _040_extrusion___470  label="4040 extrusion @ 619"
  LinkPlacement = pos=(223.598,420.363,468.333) rot=(0,-0.99808,0;0rad)
  LinkedObject = -> Body003
  Placement = pos=(223.598,420.363,468.333) rot=(0,-0.99808,0;0rad)
FEATURE [App::FeaturePython] Joint003  label="Fixed003"  # Assembly joint (typed FeaturePython)
  Activated = true
  AngleMax = 0
  AngleMin = 0
  Detach1 = false
  Detach2 = false
  Distance = 0
  Distance2 = 0
  EnableAngleMax = false
  EnableAngleMin = false
  EnableLengthMax = false
  EnableLengthMin = false
  JointType = 0 (Fixed)
  LengthMax = 0
  LengthMin = 0
  Offset2 = pos=(0,0,0) rot=(0,0,1;1.5708rad)
  Placement1 = pos=(20,-12.0325,0) rot=(-0.57735,-0.57735,0.57735;4.18879rad)
  Placement2 = pos=(20,-12.0325,0) rot=(-1,0,0;4.71239rad)
  Reference1 = -> Assembly [_040_extrusion___610.Edge57,_040_extrusion___610.Edge57]
  Reference2 = -> Assembly [_040_extrusion___470.Edge57,_040_extrusion___470.Edge57]
FEATURE [App::Link] _040_extrusion___613  label="4040 extrusion @ 620"
  LinkPlacement = pos=(-346.402,420.363,468.333) rot=(0,-0.99808,0;0rad)
  LinkedObject = -> Body003
  Placement = pos=(-346.402,420.363,468.333) rot=(0,-0.99808,0;0rad)
FEATURE [App::FeaturePython] Joint004  label="Fixed004"  # Assembly joint (typed FeaturePython)
  Activated = true
  AngleMax = 0
  AngleMin = 0
  Detach1 = false
  Detach2 = false
  Distance = 0
  Distance2 = 0
  EnableAngleMax = false
  EnableAngleMin = false
  EnableLengthMax = false
  EnableLengthMin = false
  JointType = 0 (Fixed)
  LengthMax = 0
  LengthMin = 0
  Offset2 = pos=(0,0,0) rot=(0,0,1;1.5708rad)
  Placement1 = pos=(20,-12.0325,610) rot=(-0.57735,-0.57735,0.57735;4.18879rad)
  Placement2 = pos=(-20,-12.0325,0) rot=(1,0,0;4.71239rad)
  Reference1 = -> Assembly [_040_extrusion___610.Edge58,_040_extrusion___610.Edge58]
  Reference2 = -> Assembly [_040_extrusion___613.Edge87,_040_extrusion___613.Edge87]
FEATURE [App::Link] _040_extrusion___614  label="4040 extrusion @ 621"
  LinkPlacement = pos=(223.598,990.363,468.333) rot=(0,-0.99808,0;0rad)
  LinkedObject = -> Body003
  Placement = pos=(223.598,990.363,468.333) rot=(0,-0.99808,0;0rad)
FEATURE [App::FeaturePython] Joint005  label="Fixed005"  # Assembly joint (typed FeaturePython)
  Activated = true
  AngleMax = 0
  AngleMin = 0
  Detach1 = false
  Detach2 = false
  Distance = 0
  Distance2 = 0
  EnableAngleMax = false
  EnableAngleMin = false
  EnableLengthMax = false
  EnableLengthMin = false
  JointType = 0 (Fixed)
  LengthMax = 0
  LengthMin = 0
  Offset2 = pos=(0,0,0) rot=(0,0,1;1.5708rad)
  Placement1 = pos=(20,12.0325,0) rot=(-0.57735,-0.57735,0.57735;4.18879rad)
  Placement2 = pos=(20,12.0325,0) rot=(-1,0,0;4.71239rad)
  Reference1 = -> Assembly [_040_extrusion___612.Edge33,_040_extrusion___612.Edge33]
  Reference2 = -> Assembly [_040_extrusion___614.Edge33,_040_extrusion___614.Edge33]
FEATURE [App::Link] _040_extrusion___615  label="4040 extrusion @ 622"
  LinkPlacement = pos=(-346.402,990.363,468.333) rot=(0,-0.99808,0;0rad)
  LinkedObject = -> Body003
  Placement = pos=(-346.402,990.363,468.333) rot=(0,-0.99808,0;0rad)
FEATURE [App::FeaturePython] Joint006  label="Fixed006"  # Assembly joint (typed FeaturePython)
  Activated = true
  AngleMax = 0
  AngleMin = 0
  Detach1 = false
  Detach2 = false
  Distance = 0
  Distance2 = 0
  EnableAngleMax = false
  EnableAngleMin = false
  EnableLengthMax = false
  EnableLengthMin = false
  JointType = 0 (Fixed)
  LengthMax = 0
  LengthMin = 0
  Offset2 = pos=(0,0,0) rot=(0,0,1;1.5708rad)
  Placement1 = pos=(20,12.0325,610) rot=(-0.57735,-0.57735,0.57735;4.18879rad)
  Placement2 = pos=(-20,12.0325,0) rot=(1,0,0;4.71239rad)
  Reference1 = -> Assembly [_040_extrusion___612.Edge34,_040_extrusion___612.Edge34]
  Reference2 = -> Assembly [_040_extrusion___615.Edge3,_040_extrusion___615.Edge3]
FEATURE [App::Link] _040_extrusion___616  label="4040 extrusion @ 623"
  LinkPlacement = pos=(243.598,420.363,958.333) rot=(0,1,0;4.71239rad)
  LinkedObject = -> Body001
  Placement = pos=(243.598,420.363,958.333) rot=(0,1,0;4.71239rad)
FEATURE [App::FeaturePython] Joint007  label="Fixed007"  # Assembly joint (typed FeaturePython)
  Activated = true
  AngleMax = 0
  AngleMin = 0
  Detach1 = false
  Detach2 = false
  Distance = 0
  Distance2 = 0
  EnableAngleMax = false
  EnableAngleMin = false
  EnableLengthMax = false
  EnableLengthMin = false
  JointType = 0 (Fixed)
  LengthMax = 0
  LengthMin = 0
  Offset2 = pos=(0,0,0) rot=(0,0,-1;1.5708rad)
  Placement1 = pos=(20,-12.0325,470) rot=(-0.57735,-0.57735,0.57735;4.18879rad)
  Placement2 = pos=(-20,-12.0325,-2.84e-14) rot=(0,0.707107,0.707107;3.14159rad)
  Reference1 = -> Assembly [_040_extrusion___470.Edge58,_040_extrusion___470.Edge58]
  Reference2 = -> Assembly [_040_extrusion___616.Edge87,_040_extrusion___616.Edge87]
FEATURE [App::Link] _040_extrusion___617  label="4040 extrusion @ 624"
  LinkPlacement = pos=(243.598,990.363,958.333) rot=(0,1,0;4.71239rad)
  LinkedObject = -> Body001
  Placement = pos=(243.598,990.363,958.333) rot=(0,1,0;4.71239rad)
FEATURE [App::FeaturePython] Joint008  label="Fixed008"  # Assembly joint (typed FeaturePython)
  Activated = true
  AngleMax = 0
  AngleMin = 0
  Detach1 = false
  Detach2 = false
  Distance = 0
  Distance2 = 0
  EnableAngleMax = false
  EnableAngleMin = false
  EnableLengthMax = false
  EnableLengthMin = false
  JointType = 0 (Fixed)
  LengthMax = 0
  LengthMin = 0
  Offset2 = pos=(0,0,0) rot=(0,0,-1;1.5708rad)
  Placement1 = pos=(20,12.0325,470) rot=(-0.57735,-0.57735,0.57735;4.18879rad)
  Placement2 = pos=(-20,12.0325,-2.84e-14) rot=(0,0.707107,0.707107;3.14159rad)
  Reference1 = -> Assembly [_040_extrusion___614.Edge34,_040_extrusion___614.Edge34]
  Reference2 = -> Assembly [_040_extrusion___617.Edge3,_040_extrusion___617.Edge3]
FEATURE [App::Link] _040_extrusion___618  label="4040 extrusion @ 625"
  LinkPlacement = pos=(223.598,970.363,958.333) rot=(1,0,0;1.5708rad)
  LinkedObject = -> Body002
  Placement = pos=(223.598,970.363,958.333) rot=(1,0,0;1.5708rad)
FEATURE [App::FeaturePython] Joint009  label="Fixed009"  # Assembly joint (typed FeaturePython)
  Activated = true
  AngleMax = 0
  AngleMin = 0
  Detach1 = false
  Detach2 = false
  Distance = 0
  Distance2 = 0
  EnableAngleMax = false
  EnableAngleMin = false
  EnableLengthMax = false
  EnableLengthMin = false
  JointType = 0 (Fixed)
  LengthMax = 0
  LengthMin = 0
  Offset2 = pos=(0,0,0) rot=(0,0,1;1.5708rad)
  Placement1 = pos=(12.0325,-20,-2.84e-14) rot=(-0.707107,0,0.707107;3.14159rad)
  Placement2 = pos=(20,12.0325,0) rot=(-1,0,0;4.71239rad)
  Reference1 = -> Assembly [_040_extrusion___617.Edge60,_040_extrusion___617.Edge60]
  Reference2 = -> Assembly [_040_extrusion___618.Edge33,_040_extrusion___618.Edge33]
FEATURE [App::Link] _040_extrusion___619  label="4040 extrusion @ 626"
  LinkPlacement = pos=(-346.402,970.363,958.333) rot=(1,0,0;1.5708rad)
  LinkedObject = -> Body002
  Placement = pos=(-346.402,970.363,958.333) rot=(1,0,0;1.5708rad)
FEATURE [App::FeaturePython] Joint010  label="Fixed010"  # Assembly joint (typed FeaturePython)
  Activated = true
  AngleMax = 0
  AngleMin = 0
  Detach1 = false
  Detach2 = false
  Distance = 0
  Distance2 = 0
  EnableAngleMax = false
  EnableAngleMin = false
  EnableLengthMax = false
  EnableLengthMin = false
  JointType = 0 (Fixed)
  LengthMax = 0
  LengthMin = 0
  Offset2 = pos=(0,0,0) rot=(0,0,-1;1.5708rad)
  Placement1 = pos=(12.0325,20,610) rot=(0.707107,0,0.707107;3.14159rad)
  Placement2 = pos=(-20,12.0325,530) rot=(0,0.707107,0.707107;3.14159rad)
  Reference1 = -> Assembly [_040_extrusion___616.Edge31,_040_extrusion___616.Edge31]
  Reference2 = -> Assembly [_040_extrusion___619.Edge4,_040_extrusion___619.Edge4]
FEATURE [App::Link] corner_gusset  label="corner gusset038"
  LinkPlacement = pos=(-326.402,970.363,430.365) rot=(0,0,1;4.71239rad)
  LinkedObject = -> Cut003
  Placement = pos=(-326.402,970.363,430.365) rot=(0,0,1;4.71239rad)
FEATURE [App::FeaturePython] Joint011  label="Fixed011"  # Assembly joint (typed FeaturePython)
  Activated = true
  AngleMax = 0
  AngleMin = 0
  Detach1 = false
  Detach2 = false
  Distance = 0
  Distance2 = 0
  EnableAngleMax = false
  EnableAngleMin = false
  EnableLengthMax = false
  EnableLengthMin = false
  JointType = 0 (Fixed)
  LengthMax = 0
  LengthMin = 0
  Offset2 = pos=(0,0,-5) rot=(0,0,1;3.14159rad)
  Placement1 = pos=(20,12.0325,0) rot=(-0.57735,-0.57735,0.57735;4.18879rad)
  Placement2 = pos=(0,-5.68e-14,30) rot=(0,0,1;3.14159rad)
  Reference1 = -> Assembly [_040_extrusion___611.Edge33,_040_extrusion___611.Edge33]
  Reference2 = -> Assembly [corner_gusset.Edge1,corner_gusset.Vertex1]
FEATURE [App::Link] corner_gusset001  label="corner gusset039"
  LinkPlacement = pos=(-326.402,440.363,430.865) rot=(0,-0.99808,0;0rad)
  LinkedObject = -> Cut003
  Placement = pos=(-326.402,440.363,430.865) rot=(0,-0.99808,0;0rad)
FEATURE [App::FeaturePython] Joint012  label="Fixed012"  # Assembly joint (typed FeaturePython)
  Activated = true
  AngleMax = 0
  AngleMin = 0
  Detach1 = false
  Detach2 = false
  Distance = 0
  Distance2 = 0
  EnableAngleMax = false
  EnableAngleMin = false
  EnableLengthMax = false
  EnableLengthMin = false
  JointType = 0 (Fixed)
  LengthMax = 0
  LengthMin = 0
  Offset2 = pos=(0,0,12) rot=(0,0,1;1.5708rad)
  Placement1 = pos=(20,12.0325,530) rot=(-0.57735,-0.57735,0.57735;4.18879rad)
  Placement2 = pos=(0,0,29.5) rot=(0,0,1;1.5708rad)
  Reference1 = -> Assembly [_040_extrusion___611.Edge34,_040_extrusion___611.Edge34]
  Reference2 = -> Assembly [corner_gusset001.Edge1,corner_gusset001.Edge1]
FEATURE [App::Link] corner_gusset002  label="corner gusset040"
  LinkPlacement = pos=(203.598,440.363,430.866) rot=(0,0,1;1.5708rad)
  LinkedObject = -> Cut003
  Placement = pos=(203.598,440.363,430.866) rot=(0,0,1;1.5708rad)
FEATURE [App::FeaturePython] Joint013  label="Fixed013"  # Assembly joint (typed FeaturePython)
  Activated = true
  AngleMax = 0
  AngleMin = 0
  Detach1 = false
  Detach2 = false
  Distance = 0
  Distance2 = 0
  EnableAngleMax = false
  EnableAngleMin = false
  EnableLengthMax = false
  EnableLengthMin = false
  JointType = 0 (Fixed)
  LengthMax = 0
  LengthMin = 0
  Offset2 = pos=(0,0,12) rot=(0,0,1;3.14159rad)
  Placement1 = pos=(-20,12.0325,530) rot=(0.57735,0.57735,0.57735;4.18879rad)
  Placement2 = pos=(0,-2.84e-14,29.5) rot=(0,0,1;3.14159rad)
  Reference1 = -> Assembly [_040_extrusion___530.Edge4,_040_extrusion___530.Edge4]
  Reference2 = -> Assembly [corner_gusset002.Edge1,corner_gusset002.Edge1]
FEATURE [App::Link] corner_gusset003  label="corner gusset041"
  LinkPlacement = pos=(203.598,970.363,430.866) rot=(0,0,1;3.14159rad)
  LinkedObject = -> Cut003
  Placement = pos=(203.598,970.363,430.866) rot=(0,0,1;3.14159rad)
FEATURE [App::FeaturePython] Joint014  label="Fixed014"  # Assembly joint (typed FeaturePython)
  Activated = true
  AngleMax = 0
  AngleMin = 0
  Detach1 = false
  Detach2 = false
  Distance = 0
  Distance2 = 0
  EnableAngleMax = false
  EnableAngleMin = false
  EnableLengthMax = false
  EnableLengthMin = false
  JointType = 0 (Fixed)
  LengthMax = 0
  LengthMin = 0
  Offset2 = pos=(0,0,12) rot=(0,0,1;1.5708rad)
  Placement1 = pos=(-20,12.0325,0) rot=(0.57735,0.57735,0.57735;4.18879rad)
  Placement2 = pos=(0,0,29.5) rot=(0,0,1;1.5708rad)
  Reference1 = -> Assembly [_040_extrusion___530.Edge3,_040_extrusion___530.Edge3]
  Reference2 = -> Assembly [corner_gusset003.Edge1,corner_gusset003.Edge1]
FEATURE [App::Link] _040_extrusion___100  label="4040 extrusion @ 627"
  LinkPlacement = pos=(-61.4023,970.363,448.333) rot=(1,0,0;1.5708rad)
  LinkedObject = -> Body006
  Placement = pos=(-61.4023,970.363,448.333) rot=(1,0,0;1.5708rad)
FEATURE [App::Link] _040_extrusion___620  label="8040 extrusion @ 533"
  LinkPlacement = pos=(-141.402,970.363,448.333) rot=(1,0,0;1.5708rad)
  LinkedObject = -> Body004
  Placement = pos=(-141.402,970.363,448.333) rot=(1,0,0;1.5708rad)
FEATURE [App::FeaturePython] Joint015  label="Fixed015"  # Assembly joint (typed FeaturePython)
  Activated = true
  AngleMax = 0
  AngleMin = 0
  Detach1 = false
  Detach2 = false
  Distance = 0
  Distance2 = 0
  EnableAngleMax = false
  EnableAngleMin = false
  EnableLengthMax = false
  EnableLengthMin = false
  JointType = 0 (Fixed)
  LengthMax = 0
  LengthMin = 0
  Offset2 = pos=(0,0,60) rot=(0,0,-1;1.5708rad)
  Placement1 = pos=(20,-20,305) rot=(0,0,1;0rad)
  Placement2 = pos=(80,20,0) rot=(0.57735,0.57735,0.57735;2.0944rad)
  Reference1 = -> Assembly [_040_extrusion___612.Edge56,_040_extrusion___612.Edge56]
  Reference2 = -> Assembly [_040_extrusion___620.Edge77,_040_extrusion___620.Edge77]
FEATURE [App::Link] _040_extrusion___621  label="8040 extrusion @ 534"
  LinkPlacement = pos=(-21.4023,970.363,448.333) rot=(1,0,0;1.5708rad)
  LinkedObject = -> Body004
  Placement = pos=(-21.4023,970.363,448.333) rot=(1,0,0;1.5708rad)
FEATURE [App::FeaturePython] Joint016  label="Fixed016"  # Assembly joint (typed FeaturePython)
  Activated = true
  AngleMax = 0
  AngleMin = 0
  Detach1 = false
  Detach2 = false
  Distance = 0
  Distance2 = 0
  EnableAngleMax = false
  EnableAngleMin = false
  EnableLengthMax = false
  EnableLengthMin = false
  JointType = 0 (Fixed)
  LengthMax = 0
  LengthMin = 0
  Offset2 = pos=(0,0,-60) rot=(0,0,-1;1.5708rad)
  Placement1 = pos=(20,-20,305) rot=(0,0,1;0rad)
  Placement2 = pos=(-40,20,1.137e-13) rot=(0.57735,0.57735,0.57735;2.0944rad)
  Reference1 = -> Assembly [_040_extrusion___612.Edge56,_040_extrusion___612.Edge56]
  Reference2 = -> Assembly [_040_extrusion___621.Edge77,_040_extrusion___621.Edge77]
FEATURE [App::FeaturePython] Joint017  label="Fixed017"  # Assembly joint (typed FeaturePython)
  Activated = true
  AngleMax = 0
  AngleMin = 0
  Detach1 = false
  Detach2 = false
  Distance = 0
  Distance2 = 0
  EnableAngleMax = false
  EnableAngleMin = false
  EnableLengthMax = false
  EnableLengthMin = false
  JointType = 0 (Fixed)
  LengthMax = 0
  LengthMin = 0
  Placement1 = pos=(-20,20,0) rot=(0,0,1;0rad)
  Placement2 = pos=(20,20,1.137e-13) rot=(0,0,1;0rad)
  Reference1 = -> Assembly [_040_extrusion___621.Edge50,_040_extrusion___621.Vertex35]
  Reference2 = -> Assembly [_040_extrusion___100.Edge29,_040_extrusion___100.Vertex21]
FEATURE [App::Link] _040_extrusion___622  label="4040 extrusion @ 628"
  LinkPlacement = pos=(-61.4022,540.363,448.333) rot=(1,0,0;1.5708rad)
  LinkedObject = -> Body006
  Placement = pos=(-61.4022,540.363,448.333) rot=(1,0,0;1.5708rad)
FEATURE [App::FeaturePython] Joint018  label="Fixed018"  # Assembly joint (typed FeaturePython)
  Activated = true
  AngleMax = 0
  AngleMin = 0
  Detach1 = false
  Detach2 = false
  Distance = 0
  Distance2 = 0
  EnableAngleMax = false
  EnableAngleMin = false
  EnableLengthMax = false
  EnableLengthMin = false
  JointType = 0 (Fixed)
  LengthMax = 0
  LengthMin = 0
  Placement1 = pos=(-20,20,530) rot=(0,0,1;0rad)
  Placement2 = pos=(20,20,100) rot=(0,0,1;0rad)
  Reference1 = -> Assembly [_040_extrusion___621.Edge50,_040_extrusion___621.Vertex36]
  Reference2 = -> Assembly [_040_extrusion___622.Edge29,_040_extrusion___622.Vertex22]
FEATURE [App::Link] HGR20x500  label="HGR20x502"
  LinkPlacement = pos=(18.5977,955.363,468.333) rot=(1,0,0;1.5708rad)
  LinkedObject = -> Body
  Placement = pos=(18.5977,955.363,468.333) rot=(1,0,0;1.5708rad)
FEATURE [App::FeaturePython] Joint019  label="Distance"  # Assembly joint (typed FeaturePython)
  Activated = true
  AngleMax = 0
  AngleMin = 0
  Detach1 = false
  Detach2 = false
  Distance = 0
  Distance2 = 0
  EnableAngleMax = false
  EnableAngleMin = false
  EnableLengthMax = false
  EnableLengthMin = false
  JointType = 5 (Distance)
  LengthMax = 0
  LengthMin = 0
  Placement1 = pos=(20,20,265) rot=(-0.57735,-0.57735,-0.57735;2.0944rad)
  Placement2 = pos=(0,0,250) rot=(-1,0,0;1.5708rad)
  Reference1 = -> Assembly [_040_extrusion___621.Face65,_040_extrusion___621.Vertex53]
  Reference2 = -> Assembly [HGR20x500.Face3,HGR20x500.Face3]
FEATURE [App::FeaturePython] Joint020  label="Distance001"  # Assembly joint (typed FeaturePython)
  Activated = true
  AngleMax = 0
  AngleMin = 0
  Detach1 = false
  Detach2 = false
  Distance = 15
  Distance2 = 0
  EnableAngleMax = false
  EnableAngleMin = false
  EnableLengthMax = false
  EnableLengthMin = false
  JointType = 5 (Distance)
  LengthMax = 0
  LengthMin = 0
  Placement1 = pos=(12.0325,-20,305) rot=(0,-0.707107,0.707107;3.14159rad)
  Placement2 = pos=(-2.40847e-06,9.75344,0) rot=(0,0,1;0rad)
  Reference1 = -> Assembly [_040_extrusion___612.Face20,_040_extrusion___612.Vertex39]
  Reference2 = -> Assembly [HGR20x500.Face11,HGR20x500.Face11]
FEATURE [App::FeaturePython] Joint021  label="Distance002"  # Assembly joint (typed FeaturePython)
  Activated = true
  AngleMax = 0
  AngleMin = 0
  Detach1 = false
  Detach2 = false
  Distance = -10
  Distance2 = 0
  EnableAngleMax = false
  EnableAngleMin = false
  EnableLengthMax = false
  EnableLengthMin = false
  JointType = 5 (Distance)
  LengthMax = 0
  LengthMin = 0
  Placement1 = pos=(60,12.0325,265) rot=(-0.57735,0.57735,-0.57735;2.0944rad)
  Placement2 = pos=(10,4.25,250) rot=(-0.57735,-0.57735,0.57735;2.0944rad)
  Reference1 = -> Assembly [_040_extrusion___621.Face35,_040_extrusion___621.Vertex61]
  Reference2 = -> Assembly [HGR20x500.Face4,HGR20x500.Vertex7]
FEATURE [App::Link] HGR20_carriage  label="HGR20 carriage006"
  LinkPlacement = pos=(18.5977,716.825,472.933) rot=(1,0,0;1.5708rad)
  LinkedObject = -> Body007
  Placement = pos=(18.5977,716.825,472.933) rot=(1,0,0;1.5708rad)
FEATURE [App::FeaturePython] Joint022  label="Slider"  # Assembly joint (typed FeaturePython)
  Activated = true
  AngleMax = 0
  AngleMin = 0
  Detach1 = false
  Detach2 = false
  Distance = 0
  Distance2 = 0
  EnableAngleMax = false
  EnableAngleMin = false
  EnableLengthMax = false
  EnableLengthMin = false
  JointType = 3 (Slider)
  LengthMax = 0
  LengthMin = 0
  Placement1 = pos=(9.99998,11.5,0) rot=(0,0,1;0rad)
  Placement2 = pos=(10,6.9,0) rot=(0,0,1;0rad)
  Reference1 = -> Assembly [HGR20x500.Face5,HGR20x500.Edge3]
  Reference2 = -> Assembly [HGR20_carriage.Face14,HGR20_carriage.Edge3]
FEATURE [App::Link] HGR20x501  label="HGR20x503"
  LinkPlacement = pos=(-141.402,455.363,468.333) rot=(0,0.707107,0.707107;3.14159rad)
  LinkedObject = -> Body
  Placement = pos=(-141.402,455.363,468.333) rot=(0,0.707107,0.707107;3.14159rad)
FEATURE [App::FeaturePython] Joint023  label="Distance003"  # Assembly joint (typed FeaturePython)
  Activated = true
  AngleMax = 0
  AngleMin = 0
  Detach1 = false
  Detach2 = false
  Distance = 0
  Distance2 = 0
  EnableAngleMax = false
  EnableAngleMin = false
  EnableLengthMax = false
  EnableLengthMin = false
  JointType = 5 (Distance)
  LengthMax = 0
  LengthMin = 0
  Placement1 = pos=(20,20,265) rot=(-0.57735,-0.57735,-0.57735;2.0944rad)
  Placement2 = pos=(0,0,250) rot=(-1,0,0;1.5708rad)
  Reference1 = -> Assembly [_040_extrusion___620.Face65,_040_extrusion___620.Vertex53]
  Reference2 = -> Assembly [HGR20x501.Face3,HGR20x501.Vertex5]
FEATURE [App::FeaturePython] Joint024  label="Distance004"  # Assembly joint (typed FeaturePython)
  Activated = true
  AngleMax = 0
  AngleMin = 0
  Detach1 = false
  Detach2 = false
  Distance = 15
  Distance2 = 0
  EnableAngleMax = false
  EnableAngleMin = false
  EnableLengthMax = false
  EnableLengthMin = false
  JointType = 5 (Distance)
  LengthMax = 0
  LengthMin = 0
  Placement1 = pos=(12.0325,-20,305) rot=(0,-0.707107,0.707107;3.14159rad)
  Placement2 = pos=(-2.40847e-06,9.75344,500) rot=(0,0,1;0rad)
  Reference1 = -> Assembly [_040_extrusion___612.Face20,_040_extrusion___612.Face20]
  Reference2 = -> Assembly [HGR20x501.Face12,HGR20x501.Face12]
FEATURE [App::FeaturePython] Joint025  label="Distance005"  # Assembly joint (typed FeaturePython)
  Activated = true
  AngleMax = 0
  AngleMin = 0
  Detach1 = false
  Detach2 = false
  Distance = -10
  Distance2 = 0
  EnableAngleMax = false
  EnableAngleMin = false
  EnableLengthMax = false
  EnableLengthMin = false
  JointType = 5 (Distance)
  LengthMax = 0
  LengthMin = 0
  Placement1 = pos=(-20,12.0325,265) rot=(-0.57735,-0.57735,0.57735;2.0944rad)
  Placement2 = pos=(10,4.25,250) rot=(-0.57735,-0.57735,0.57735;2.0944rad)
  Reference1 = -> Assembly [_040_extrusion___620.Face17,_040_extrusion___620.Vertex35]
  Reference2 = -> Assembly [HGR20x501.Face4,HGR20x501.Vertex8]
FEATURE [App::Link] HGR20_carriage001  label="HGR20 carriage007"
  LinkPlacement = pos=(18.5977,834.643,472.933) rot=(1,0,0;1.5708rad)
  LinkedObject = -> Body007
  Placement = pos=(18.5977,834.643,472.933) rot=(1,0,0;1.5708rad)
FEATURE [App::FeaturePython] Joint026  label="Slider001"  # Assembly joint (typed FeaturePython)
  Activated = true
  AngleMax = 0
  AngleMin = 0
  Detach1 = false
  Detach2 = false
  Distance = 0
  Distance2 = 0
  EnableAngleMax = false
  EnableAngleMin = false
  EnableLengthMax = false
  EnableLengthMin = false
  JointType = 3 (Slider)
  LengthMax = 0
  LengthMin = 0
  Placement1 = pos=(-10,11.5,0) rot=(0,0,1;0rad)
  Placement2 = pos=(-10,6.9,0) rot=(0,0,1;0rad)
  Reference1 = -> Assembly [HGR20x500.Face1,HGR20x500.Edge3]
  Reference2 = -> Assembly [HGR20_carriage001.Face20,HGR20_carriage001.Edge3]
FEATURE [App::Link] HGR20_carriage002  label="HGR20 carriage008"
  LinkPlacement = pos=(-141.402,834.643,472.933) rot=(1,0,0;1.5708rad)
  LinkedObject = -> Body007
  Placement = pos=(-141.402,834.643,472.933) rot=(1,0,0;1.5708rad)
FEATURE [App::FeaturePython] Joint027  label="Slider002"  # Assembly joint (typed FeaturePython)
  Activated = true
  AngleMax = 0
  AngleMin = 0
  Detach1 = false
  Detach2 = false
  Distance = 0
  Distance2 = 0
  EnableAngleMax = false
  EnableAngleMin = false
  EnableLengthMax = false
  EnableLengthMin = false
  JointType = 3 (Slider)
  LengthMax = 0
  LengthMin = 0
  Offset2 = pos=(0,0,0) rot=(0,0,1;3.14159rad)
  Placement1 = pos=(-10,11.5,500) rot=(0,0,1;0rad)
  Placement2 = pos=(10,6.9,0) rot=(0,0,1;3.14159rad)
  Reference1 = -> Assembly [HGR20x501.Face1,HGR20x501.Edge4]
  Reference2 = -> Assembly [HGR20_carriage002.Face14,HGR20_carriage002.Edge3]
FEATURE [App::Link] HGR20_carriage003  label="HGR20 carriage009"
  LinkPlacement = pos=(-141.402,716.825,472.933) rot=(1,0,0;1.5708rad)
  LinkedObject = -> Body007
  Placement = pos=(-141.402,716.825,472.933) rot=(1,0,0;1.5708rad)
FEATURE [App::FeaturePython] Joint028  label="Slider003"  # Assembly joint (typed FeaturePython)
  Activated = true
  AngleMax = 0
  AngleMin = 0
  Detach1 = false
  Detach2 = false
  Distance = 0
  Distance2 = 0
  EnableAngleMax = false
  EnableAngleMin = false
  EnableLengthMax = false
  EnableLengthMin = false
  JointType = 3 (Slider)
  LengthMax = 0
  LengthMin = 0
  Offset2 = pos=(0,0,0) rot=(0,0,1;3.14159rad)
  Placement1 = pos=(-10,11.5,250) rot=(0,0,1;0rad)
  Placement2 = pos=(10,6.9,0) rot=(0,0,1;3.14159rad)
  Reference1 = -> Assembly [HGR20x501.Face1,HGR20x501.Face1]
  Reference2 = -> Assembly [HGR20_carriage003.Face14,HGR20_carriage003.Edge3]
FEATURE [App::Link] XY_gantry_plate  label="XY gantry plate003"
  LinkPlacement = pos=(-61.4023,739.234,538.333) rot=(0.707107,0.707107,0;3.14159rad)
  LinkedObject = -> Body008
  Placement = pos=(-61.4023,739.234,538.333) rot=(0.707107,0.707107,0;3.14159rad)
FEATURE [App::FeaturePython] Joint029  label="Cylindrical"  # Assembly joint (typed FeaturePython)
  Activated = true
  AngleMax = 0
  AngleMin = 0
  Detach1 = false
  Detach2 = false
  Distance = 0
  Distance2 = 0
  EnableAngleMax = false
  EnableAngleMin = false
  EnableLengthMax = false
  EnableLengthMin = false
  JointType = 2 (Cylindrical)
  LengthMax = 0
  LengthMin = 0
  Placement1 = pos=(76.9092,96,1.137e-13) rot=(0,0,1;0rad)
  Placement2 = pos=(16,25.4,18.5) rot=(0,0.707107,0.707107;3.14159rad)
  Reference1 = -> Assembly [XY_gantry_plate.Edge38,XY_gantry_plate.Edge38]
  Reference2 = -> Assembly [HGR20_carriage001.Edge14,HGR20_carriage001.Edge14]
FEATURE [App::FeaturePython] Joint030  label="Cylindrical001"  # Assembly joint (typed FeaturePython)
  Activated = true
  AngleMax = 0
  AngleMin = 0
  Detach1 = false
  Detach2 = false
  Distance = 0
  Distance2 = 0
  EnableAngleMax = false
  EnableAngleMin = false
  EnableLengthMax = false
  EnableLengthMin = false
  JointType = 2 (Cylindrical)
  LengthMax = 0
  LengthMin = 0
  Placement1 = pos=(16,25.4,54.5) rot=(0,0.707107,0.707107;3.14159rad)
  Placement2 = pos=(-76.9092,96,1.137e-13) rot=(0,0,1;0rad)
  Reference1 = -> Assembly [HGR20_carriage.Edge12,HGR20_carriage.Edge12]
  Reference2 = -> Assembly [XY_gantry_plate.Edge59,XY_gantry_plate.Edge59]
FEATURE [App::FeaturePython] Joint031  label="Cylindrical002"  # Assembly joint (typed FeaturePython)
  Activated = true
  AngleMax = 0
  AngleMin = 0
  Detach1 = false
  Detach2 = false
  Distance = 0
  Distance2 = 0
  EnableAngleMax = false
  EnableAngleMin = false
  EnableLengthMax = false
  EnableLengthMin = false
  JointType = 2 (Cylindrical)
  LengthMax = 0
  LengthMin = 0
  Placement1 = pos=(-16,25.4,54.5) rot=(0,0.707107,0.707107;3.14159rad)
  Placement2 = pos=(-76.9092,-96,0) rot=(0,0,1;0rad)
  Reference1 = -> Assembly [HGR20_carriage003.Edge11,HGR20_carriage003.Edge11]
  Reference2 = -> Assembly [XY_gantry_plate.Edge47,XY_gantry_plate.Edge47]
FEATURE [App::FeaturePython] Joint032  label="Cylindrical003"  # Assembly joint (typed FeaturePython)
  Activated = true
  AngleMax = 0
  AngleMin = 0
  Detach1 = false
  Detach2 = false
  Distance = 0
  Distance2 = 0
  EnableAngleMax = false
  EnableAngleMin = false
  EnableLengthMax = false
  EnableLengthMin = false
  JointType = 2 (Cylindrical)
  LengthMax = 0
  LengthMin = 0
  Placement1 = pos=(76.9092,-96,0) rot=(0,0,1;0rad)
  Placement2 = pos=(-16,25.4,18.5) rot=(0,0.707107,0.707107;3.14159rad)
  Reference1 = -> Assembly [XY_gantry_plate.Edge26,XY_gantry_plate.Edge26]
  Reference2 = -> Assembly [HGR20_carriage002.Edge13,HGR20_carriage002.Edge13]
FEATURE [App::FeaturePython] Joint033  label="Distance006"  # Assembly joint (typed FeaturePython)
  Activated = true
  AngleMax = 0
  AngleMin = 0
  Detach1 = false
  Detach2 = false
  Distance = 30
  Distance2 = 0
  EnableAngleMax = false
  EnableAngleMin = false
  EnableLengthMax = false
  EnableLengthMin = false
  JointType = 5 (Distance)
  LengthMax = 0
  LengthMin = 0
  Placement1 = pos=(0,-7.1e-15,10) rot=(0,0,1;0rad)
  Placement2 = pos=(2.84e-14,25.4,36.5) rot=(-1,0,0;1.5708rad)
  Reference1 = -> Assembly [XY_gantry_plate.Face22,XY_gantry_plate.Face22]
  Reference2 = -> Assembly [HGR20_carriage002.Face3,HGR20_carriage002.Face3]
FEATURE [App::Link] corner_gusset004  label="corner gusset042"
  LinkPlacement = pos=(203.598,437.863,468.333) rot=(0.57735,-0.57735,0.57735;2.0944rad)
  LinkedObject = -> Cut003
  Placement = pos=(203.598,437.863,468.333) rot=(0.57735,-0.57735,0.57735;2.0944rad)
FEATURE [App::Link] corner_gusset005  label="corner gusset043"
  LinkPlacement = pos=(206.098,440.363,468.333) rot=(0.57735,0.57735,0.57735;2.0944rad)
  LinkedObject = -> Cut003
  Placement = pos=(206.098,440.363,468.333) rot=(0.57735,0.57735,0.57735;2.0944rad)
FEATURE [App::Link] corner_gusset006  label="corner gusset044"
  LinkPlacement = pos=(-326.402,402.863,468.333) rot=(0.57735,0.57735,0.57735;4.18879rad)
  LinkedObject = -> Cut003
  Placement = pos=(-326.402,402.863,468.333) rot=(0.57735,0.57735,0.57735;4.18879rad)
FEATURE [App::Link] corner_gusset007  label="corner gusset045"
  LinkPlacement = pos=(-363.902,440.363,468.333) rot=(0.57735,0.57735,0.57735;2.0944rad)
  LinkedObject = -> Cut003
  Placement = pos=(-363.902,440.363,468.333) rot=(0.57735,0.57735,0.57735;2.0944rad)
FEATURE [App::Link] corner_gusset008  label="corner gusset046"
  LinkPlacement = pos=(-363.902,970.363,468.333) rot=(0.707107,0,0.707107;3.14159rad)
  LinkedObject = -> Cut003
  Placement = pos=(-363.902,970.363,468.333) rot=(0.707107,0,0.707107;3.14159rad)
FEATURE [App::Link] corner_gusset009  label="corner gusset047"
  LinkPlacement = pos=(-326.402,972.863,468.333) rot=(0.57735,0.57735,0.57735;4.18879rad)
  LinkedObject = -> Cut003
  Placement = pos=(-326.402,972.863,468.333) rot=(0.57735,0.57735,0.57735;4.18879rad)
FEATURE [App::Link] corner_gusset010  label="corner gusset048"
  LinkPlacement = pos=(203.598,1007.86,468.333) rot=(0.57735,-0.57735,0.57735;2.0944rad)
  LinkedObject = -> Cut003
  Placement = pos=(203.598,1007.86,468.333) rot=(0.57735,-0.57735,0.57735;2.0944rad)
FEATURE [App::Link] corner_gusset011  label="corner gusset049"
  LinkPlacement = pos=(206.098,970.363,468.333) rot=(0.707107,0,0.707107;3.14159rad)
  LinkedObject = -> Cut003
  Placement = pos=(206.098,970.363,468.333) rot=(0.707107,0,0.707107;3.14159rad)
FEATURE [App::FeaturePython] Joint034  label="Fixed019"  # Assembly joint (typed FeaturePython)
  Activated = true
  AngleMax = 0
  AngleMin = 0
  Detach1 = false
  Detach2 = false
  Distance = 0
  Distance2 = 0
  EnableAngleMax = false
  EnableAngleMin = false
  EnableLengthMax = false
  EnableLengthMin = false
  JointType = 0 (Fixed)
  LengthMax = 0
  LengthMin = 0
  Offset2 = pos=(0,0,2.5) rot=(0,0,1;0rad)
  Placement1 = pos=(-20,-20,5.68e-14) rot=(0.57735,0.57735,0.57735;4.18879rad)
  Placement2 = pos=(0,0,37.5) rot=(0,0,1;0rad)
  Reference1 = -> Assembly [_040_extrusion___470.Edge87,_040_extrusion___470.Vertex57]
  Reference2 = -> Assembly [corner_gusset004.Edge1,corner_gusset004.Vertex1]
FEATURE [App::FeaturePython] Joint035  label="Fixed020"  # Assembly joint (typed FeaturePython)
  Activated = true
  AngleMax = 0
  AngleMin = 0
  Detach1 = false
  Detach2 = false
  Distance = 0
  Distance2 = 0
  EnableAngleMax = false
  EnableAngleMin = false
  EnableLengthMax = false
  EnableLengthMin = false
  JointType = 0 (Fixed)
  LengthMax = 0
  LengthMin = 0
  Offset2 = pos=(0,0,-2.5) rot=(0,0,1;1.5708rad)
  Placement1 = pos=(-20,20,5.68e-14) rot=(0.707107,0,0.707107;3.14159rad)
  Placement2 = pos=(0,0,-2.5) rot=(0,0,1;1.5708rad)
  Reference1 = -> Assembly [_040_extrusion___470.Edge6,_040_extrusion___470.Vertex3]
  Reference2 = -> Assembly [corner_gusset005.Edge1,corner_gusset005.Vertex2]
FEATURE [App::FeaturePython] Joint036  label="Fixed021"  # Assembly joint (typed FeaturePython)
  Activated = true
  AngleMax = 0
  AngleMin = 0
  Detach1 = false
  Detach2 = false
  Distance = 0
  Distance2 = 0
  EnableAngleMax = false
  EnableAngleMin = false
  EnableLengthMax = false
  EnableLengthMin = false
  JointType = 0 (Fixed)
  LengthMax = 0
  LengthMin = 0
  Offset2 = pos=(0,0,-2.5) rot=(0,0,1;3.14159rad)
  Placement1 = pos=(20,-20,0) rot=(-0.57735,-0.57735,0.57735;4.18879rad)
  Placement2 = pos=(0,0,-2.5) rot=(0,0,1;3.14159rad)
  Reference1 = -> Assembly [_040_extrusion___613.Edge57,_040_extrusion___613.Vertex39]
  Reference2 = -> Assembly [corner_gusset006.Edge1,corner_gusset006.Vertex2]
FEATURE [App::FeaturePython] Joint037  label="Fixed022"  # Assembly joint (typed FeaturePython)
  Activated = true
  AngleMax = 0
  AngleMin = 0
  Detach1 = false
  Detach2 = false
  Distance = 0
  Distance2 = 0
  EnableAngleMax = false
  EnableAngleMin = false
  EnableLengthMax = false
  EnableLengthMin = false
  JointType = 0 (Fixed)
  LengthMax = 0
  LengthMin = 0
  Offset2 = pos=(0,0,-2.5) rot=(0,0,1;1.5708rad)
  Placement1 = pos=(20,20,610) rot=(0,0,1;0rad)
  Placement2 = pos=(0,0,-2.5) rot=(0,0,1;1.5708rad)
  Reference1 = -> Assembly [_040_extrusion___610.Edge29,_040_extrusion___610.Vertex22]
  Reference2 = -> Assembly [corner_gusset007.Edge1,corner_gusset007.Vertex2]
FEATURE [App::FeaturePython] Joint038  label="Fixed023"  # Assembly joint (typed FeaturePython)
  Activated = true
  AngleMax = 0
  AngleMin = 0
  Detach1 = false
  Detach2 = false
  Distance = 0
  Distance2 = 0
  EnableAngleMax = false
  EnableAngleMin = false
  EnableLengthMax = false
  EnableLengthMin = false
  JointType = 0 (Fixed)
  LengthMax = 0
  LengthMin = 0
  Offset2 = pos=(0,0,-2.5) rot=(0,0,1;0rad)
  Placement1 = pos=(20,-20,610) rot=(0,0,1;0rad)
  Placement2 = pos=(0,0,-2.5) rot=(0,0,1;0rad)
  Reference1 = -> Assembly [_040_extrusion___612.Edge56,_040_extrusion___612.Vertex40]
  Reference2 = -> Assembly [corner_gusset008.Edge1,corner_gusset008.Vertex2]
FEATURE [App::FeaturePython] Joint039  label="Fixed024"  # Assembly joint (typed FeaturePython)
  Activated = true
  AngleMax = 0
  AngleMin = 0
  Detach1 = false
  Detach2 = false
  Distance = 0
  Distance2 = 0
  EnableAngleMax = false
  EnableAngleMin = false
  EnableLengthMax = false
  EnableLengthMin = false
  JointType = 0 (Fixed)
  LengthMax = 0
  LengthMin = 0
  Offset2 = pos=(0,0,37.5) rot=(0,0,1;3.14159rad)
  Placement1 = pos=(20,20,0) rot=(-0.57735,-0.57735,0.57735;4.18879rad)
  Placement2 = pos=(0,0,37.5) rot=(0,0,1;3.14159rad)
  Reference1 = -> Assembly [_040_extrusion___615.Edge33,_040_extrusion___615.Vertex21]
  Reference2 = -> Assembly [corner_gusset009.Edge1,corner_gusset009.Vertex2]
FEATURE [App::FeaturePython] Joint040  label="Fixed025"  # Assembly joint (typed FeaturePython)
  Activated = true
  AngleMax = 0
  AngleMin = 0
  Detach1 = false
  Detach2 = false
  Distance = 0
  Distance2 = 0
  EnableAngleMax = false
  EnableAngleMin = false
  EnableLengthMax = false
  EnableLengthMin = false
  JointType = 0 (Fixed)
  LengthMax = 0
  LengthMin = 0
  Offset2 = pos=(0,0,-2.5) rot=(0,0,1;0rad)
  Placement1 = pos=(-20,20,5.68e-14) rot=(0.57735,0.57735,0.57735;4.18879rad)
  Placement2 = pos=(0,0,-2.5) rot=(0,0,1;0rad)
  Reference1 = -> Assembly [_040_extrusion___614.Edge3,_040_extrusion___614.Vertex3]
  Reference2 = -> Assembly [corner_gusset010.Edge1,corner_gusset010.Vertex2]
FEATURE [App::FeaturePython] Joint041  label="Fixed026"  # Assembly joint (typed FeaturePython)
  Activated = true
  AngleMax = 0
  AngleMin = 0
  Detach1 = false
  Detach2 = false
  Distance = 0
  Distance2 = 0
  EnableAngleMax = false
  EnableAngleMin = false
  EnableLengthMax = false
  EnableLengthMin = false
  JointType = 0 (Fixed)
  LengthMax = 0
  LengthMin = 0
  Offset2 = pos=(0,0,37.5) rot=(0,0,1;1.5708rad)
  Placement1 = pos=(20,20,0) rot=(0.707107,0,0.707107;3.14159rad)
  Placement2 = pos=(0,0,37.5) rot=(0,0,1;1.5708rad)
  Reference1 = -> Assembly [_040_extrusion___530.Edge30,_040_extrusion___530.Vertex21]
  Reference2 = -> Assembly [corner_gusset011.Edge1,corner_gusset011.Vertex2]
FEATURE [App::Link] nema23
  LinkPlacement = pos=(-50.0002,1029,494) rot=(1,0,0;1.5708rad)
  LinkedObject = -> <external ../xcadlib/nema23.FCStd>#Body
  Placement = pos=(-50.0002,1029,494) rot=(1,0,0;1.5708rad)
FEATURE [App::Link] corner_gusset037  label="corner gusset050"
  LinkPlacement = pos=(-326.402,440.363,940.833) rot=(0,-0.99808,0;0rad)
  LinkedObject = -> Cut007
  Placement = pos=(-326.402,440.363,940.833) rot=(0,-0.99808,0;0rad)
FEATURE [App::Link] corner_gusset038  label="corner gusset051"
  LinkPlacement = pos=(-326.402,970.363,940.833) rot=(0,0,1;4.71239rad)
  LinkedObject = -> Cut007
  Placement = pos=(-326.402,970.363,940.833) rot=(0,0,1;4.71239rad)
FEATURE [App::Link] corner_gusset039  label="corner gusset052"
  LinkPlacement = pos=(203.598,970.363,940.833) rot=(0,0,1;3.14159rad)
  LinkedObject = -> Cut007
  Placement = pos=(203.598,970.363,940.833) rot=(0,0,1;3.14159rad)
FEATURE [App::Link] corner_gusset040  label="corner gusset053"
  LinkPlacement = pos=(203.598,440.363,940.833) rot=(0,0,1;1.5708rad)
  LinkedObject = -> Cut007
  Placement = pos=(203.598,440.363,940.833) rot=(0,0,1;1.5708rad)
FEATURE [App::Link] corner_gusset041  label="corner gusset054"
  LinkPlacement = pos=(-326.402,972.863,938.333) rot=(-1,0,0;1.5708rad)
  LinkedObject = -> Cut007
  Placement = pos=(-326.402,972.863,938.333) rot=(-1,0,0;1.5708rad)
FEATURE [App::Link] corner_gusset042  label="corner gusset055"
  LinkPlacement = pos=(-363.902,970.363,938.333) rot=(-0.57735,0.57735,-0.57735;2.0944rad)
  LinkedObject = -> Cut007
  Placement = pos=(-363.902,970.363,938.333) rot=(-0.57735,0.57735,-0.57735;2.0944rad)
FEATURE [App::Link] corner_gusset043  label="corner gusset056"
  LinkPlacement = pos=(203.598,1010.83,938.333) rot=(0,0.707107,-0.707107;3.14159rad)
  LinkedObject = -> Cut007
  Placement = pos=(203.598,1010.83,938.333) rot=(0,0.707107,-0.707107;3.14159rad)
FEATURE [App::Link] corner_gusset044  label="corner gusset057"
  LinkPlacement = pos=(206.098,970.363,938.333) rot=(-0.57735,0.57735,-0.57735;2.0944rad)
  LinkedObject = -> Cut007
  Placement = pos=(206.098,970.363,938.333) rot=(-0.57735,0.57735,-0.57735;2.0944rad)
FEATURE [App::Link] corner_gusset045  label="corner gusset058"
  LinkPlacement = pos=(203.598,437.863,938.333) rot=(0,-0.707107,0.707107;3.14159rad)
  LinkedObject = -> Cut007
  Placement = pos=(203.598,437.863,938.333) rot=(0,-0.707107,0.707107;3.14159rad)
FEATURE [App::Link] corner_gusset046  label="corner gusset059"
  LinkPlacement = pos=(206.098,440.363,938.333) rot=(0,1,0;1.5708rad)
  LinkedObject = -> Cut007
  Placement = pos=(206.098,440.363,938.333) rot=(0,1,0;1.5708rad)
FEATURE [App::Link] corner_gusset047  label="corner gusset060"
  LinkPlacement = pos=(-363.902,440.363,938.333) rot=(0,1,0;1.5708rad)
  LinkedObject = -> Cut007
  Placement = pos=(-363.902,440.363,938.333) rot=(0,1,0;1.5708rad)
FEATURE [App::Link] corner_gusset048  label="corner gusset061"
  LinkPlacement = pos=(-326.402,402.863,938.333) rot=(-1,0,0;1.5708rad)
  LinkedObject = -> Cut007
  Placement = pos=(-326.402,402.863,938.333) rot=(-1,0,0;1.5708rad)
FEATURE [App::FeaturePython] Joint042  label="Fixed027"  # Assembly joint (typed FeaturePython)
  Activated = true
  AngleMax = 0
  AngleMin = 0
  Detach1 = false
  Detach2 = false
  Distance = 0
  Distance2 = 0
  EnableAngleMax = false
  EnableAngleMin = false
  EnableLengthMax = false
  EnableLengthMin = false
  JointType = 0 (Fixed)
  LengthMax = 0
  LengthMin = 0
  Offset2 = pos=(0,0,2.5) rot=(0,0,1;1.5708rad)
  Placement1 = pos=(0,0,35) rot=(0,0,1;0rad)
  Placement2 = pos=(20,17.5,530) rot=(-1,0,0;4.71239rad)
  Reference1 = -> Assembly [corner_gusset037.Edge1,corner_gusset037.Vertex1]
  Reference2 = -> Assembly [_040_extrusion___619.Edge34,_040_extrusion___619.Vertex22]
FEATURE [App::FeaturePython] Joint043  label="Fixed028"  # Assembly joint (typed FeaturePython)
  Activated = true
  AngleMax = 0
  AngleMin = 0
  Detach1 = false
  Detach2 = false
  Distance = 0
  Distance2 = 0
  EnableAngleMax = false
  EnableAngleMin = false
  EnableLengthMax = false
  EnableLengthMin = false
  JointType = 0 (Fixed)
  LengthMax = 0
  LengthMin = 0
  Offset2 = pos=(0,0,2.5) rot=(0,0,1;3.14159rad)
  Placement1 = pos=(0,0,35) rot=(0,0,1;0rad)
  Placement2 = pos=(20,17.5,0) rot=(-0.57735,0.57735,-0.57735;4.18879rad)
  Reference1 = -> Assembly [corner_gusset038.Edge1,corner_gusset038.Vertex1]
  Reference2 = -> Assembly [_040_extrusion___619.Edge33,_040_extrusion___619.Vertex21]
FEATURE [App::FeaturePython] Joint044  label="Fixed029"  # Assembly joint (typed FeaturePython)
  Activated = true
  AngleMax = 0
  AngleMin = 0
  Detach1 = false
  Detach2 = false
  Distance = 0
  Distance2 = 0
  EnableAngleMax = false
  EnableAngleMin = false
  EnableLengthMax = false
  EnableLengthMin = false
  JointType = 0 (Fixed)
  LengthMax = 0
  LengthMin = 0
  Offset2 = pos=(0,0,-2.5) rot=(0,0,-1;1.5708rad)
  Placement1 = pos=(0,0,35) rot=(0,0,1;0rad)
  Placement2 = pos=(-20,17.5,0) rot=(0,0.707107,0.707107;3.14159rad)
  Reference1 = -> Assembly [corner_gusset039.Edge1,corner_gusset039.Vertex1]
  Reference2 = -> Assembly [_040_extrusion___618.Edge3,_040_extrusion___618.Vertex3]
FEATURE [App::FeaturePython] Joint045  label="Fixed030"  # Assembly joint (typed FeaturePython)
  Activated = true
  AngleMax = 0
  AngleMin = 0
  Detach1 = false
  Detach2 = false
  Distance = 0
  Distance2 = 0
  EnableAngleMax = false
  EnableAngleMin = false
  EnableLengthMax = false
  EnableLengthMin = false
  JointType = 0 (Fixed)
  LengthMax = 0
  LengthMin = 0
  Offset2 = pos=(0,0,-2.5) rot=(0,0,1;3.14159rad)
  Placement1 = pos=(-5.68e-14,-2.84e-14,35) rot=(0,0,1;0rad)
  Placement2 = pos=(-20,17.5,530) rot=(0.57735,-0.57735,-0.57735;4.18879rad)
  Reference1 = -> Assembly [corner_gusset040.Edge1,corner_gusset040.Vertex1]
  Reference2 = -> Assembly [_040_extrusion___618.Edge4,_040_extrusion___618.Vertex4]
FEATURE [App::FeaturePython] Joint046  label="Fixed031"  # Assembly joint (typed FeaturePython)
  Activated = true
  AngleMax = 0
  AngleMin = 0
  Detach1 = false
  Detach2 = false
  Distance = 0
  Distance2 = 0
  EnableAngleMax = false
  EnableAngleMin = false
  EnableLengthMax = false
  EnableLengthMin = false
  JointType = 0 (Fixed)
  LengthMax = 0
  LengthMin = 0
  Offset2 = pos=(0,0,2.5) rot=(0,0,1;1.5708rad)
  Placement1 = pos=(0,0,35) rot=(0,0,1;0rad)
  Placement2 = pos=(20,17.5,470) rot=(-1,0,0;4.71239rad)
  Reference1 = -> Assembly [corner_gusset041.Edge1,corner_gusset041.Vertex1]
  Reference2 = -> Assembly [_040_extrusion___615.Edge34,_040_extrusion___615.Vertex22]
FEATURE [App::FeaturePython] Joint047  label="Fixed032"  # Assembly joint (typed FeaturePython)
  Activated = true
  AngleMax = 0
  AngleMin = 0
  Detach1 = false
  Detach2 = false
  Distance = 0
  Distance2 = 0
  EnableAngleMax = false
  EnableAngleMin = false
  EnableLengthMax = false
  EnableLengthMin = false
  JointType = 0 (Fixed)
  LengthMax = 0
  LengthMin = 0
  Offset2 = pos=(0,0,2.5) rot=(0,0,1;1.5708rad)
  Placement1 = pos=(0,0,35) rot=(0,0,1;0rad)
  Placement2 = pos=(17.5,-20,470) rot=(-0.57735,0.57735,0.57735;4.18879rad)
  Reference1 = -> Assembly [corner_gusset042.Edge1,corner_gusset042.Vertex1]
  Reference2 = -> Assembly [_040_extrusion___615.Edge61,_040_extrusion___615.Vertex40]
FEATURE [App::FeaturePython] Joint048  label="Fixed033"  # Assembly joint (typed FeaturePython)
  Activated = true
  AngleMax = 0
  AngleMin = 0
  Detach1 = false
  Detach2 = false
  Distance = 0
  Distance2 = 0
  EnableAngleMax = false
  EnableAngleMin = false
  EnableLengthMax = false
  EnableLengthMin = false
  JointType = 0 (Fixed)
  LengthMax = 0
  LengthMin = 0
  Offset2 = pos=(0,0,-2.5) rot=(0,0,-1;1.5708rad)
  Placement1 = pos=(0,0,35) rot=(0,0,1;0rad)
  Placement2 = pos=(-20,-14.5325,470) rot=(0,0.707107,0.707107;3.14159rad)
  Reference1 = -> Assembly [corner_gusset043.Edge1,corner_gusset043.Vertex1]
  Reference2 = -> Assembly [_040_extrusion___614.Edge88,_040_extrusion___614.Edge88]
FEATURE [App::FeaturePython] Joint049  label="Fixed034"  # Assembly joint (typed FeaturePython)
  Activated = true
  AngleMax = 0
  AngleMin = 0
  Detach1 = false
  Detach2 = false
  Distance = 0
  Distance2 = 0
  EnableAngleMax = false
  EnableAngleMin = false
  EnableLengthMax = false
  EnableLengthMin = false
  JointType = 0 (Fixed)
  LengthMax = 0
  LengthMin = 0
  Offset2 = pos=(0,0,2.5) rot=(0,0,1;1.5708rad)
  Placement1 = pos=(0,0,35) rot=(0,0,1;0rad)
  Placement2 = pos=(17.5,-20,470) rot=(-0.57735,0.57735,0.57735;4.18879rad)
  Reference1 = -> Assembly [corner_gusset044.Edge1,corner_gusset044.Vertex1]
  Reference2 = -> Assembly [_040_extrusion___614.Edge61,_040_extrusion___614.Vertex40]
FEATURE [App::FeaturePython] Joint050  label="Fixed035"  # Assembly joint (typed FeaturePython)
  Activated = true
  AngleMax = 0
  AngleMin = 0
  Detach1 = false
  Detach2 = false
  Distance = 0
  Distance2 = 0
  EnableAngleMax = false
  EnableAngleMin = false
  EnableLengthMax = false
  EnableLengthMin = false
  JointType = 0 (Fixed)
  LengthMax = 0
  LengthMin = 0
  Offset2 = pos=(0,0,2.5) rot=(0,0,-1;1.5708rad)
  Placement1 = pos=(0,0,35) rot=(0,0,1;0rad)
  Placement2 = pos=(-20,-17.5,470) rot=(0,0.707107,0.707107;3.14159rad)
  Reference1 = -> Assembly [corner_gusset045.Edge1,corner_gusset045.Vertex1]
  Reference2 = -> Assembly [_040_extrusion___470.Edge88,_040_extrusion___470.Vertex58]
FEATURE [App::FeaturePython] Joint051  label="Fixed036"  # Assembly joint (typed FeaturePython)
  Activated = true
  AngleMax = 0
  AngleMin = 0
  Detach1 = false
  Detach2 = false
  Distance = 0
  Distance2 = 0
  EnableAngleMax = false
  EnableAngleMin = false
  EnableLengthMax = false
  EnableLengthMin = false
  JointType = 0 (Fixed)
  LengthMax = 0
  LengthMin = 0
  Offset2 = pos=(0,0,2.5) rot=(0,0,1;1.5708rad)
  Placement1 = pos=(-1.137e-13,0,35) rot=(0,0,1;0rad)
  Placement2 = pos=(17.5,-20,530) rot=(-0.57735,0.57735,0.57735;4.18879rad)
  Reference1 = -> Assembly [corner_gusset046.Edge1,corner_gusset046.Vertex1]
  Reference2 = -> Assembly [_040_extrusion___618.Edge61,_040_extrusion___618.Vertex40]
FEATURE [App::FeaturePython] Joint052  label="Fixed037"  # Assembly joint (typed FeaturePython)
  Activated = true
  AngleMax = 0
  AngleMin = 0
  Detach1 = false
  Detach2 = false
  Distance = 0
  Distance2 = 0
  EnableAngleMax = false
  EnableAngleMin = false
  EnableLengthMax = false
  EnableLengthMin = false
  JointType = 0 (Fixed)
  LengthMax = 0
  LengthMin = 0
  Offset2 = pos=(0,0,-37.5) rot=(0,0,1;1.5708rad)
  Placement1 = pos=(0,0,35) rot=(0,0,1;0rad)
  Placement2 = pos=(17.5,-20,530) rot=(-0.57735,0.57735,0.57735;4.18879rad)
  Reference1 = -> Assembly [corner_gusset047.Edge1,corner_gusset047.Vertex1]
  Reference2 = -> Assembly [_040_extrusion___619.Edge85,_040_extrusion___619.Vertex58]
FEATURE [App::FeaturePython] Joint053  label="Fixed038"  # Assembly joint (typed FeaturePython)
  Activated = true
  AngleMax = 0
  AngleMin = 0
  Detach1 = false
  Detach2 = false
  Distance = 0
  Distance2 = 0
  EnableAngleMax = false
  EnableAngleMin = false
  EnableLengthMax = false
  EnableLengthMin = false
  JointType = 0 (Fixed)
  LengthMax = 0
  LengthMin = 0
  Offset2 = pos=(0,0,-37.5) rot=(0,0,1;1.5708rad)
  Placement1 = pos=(0,0,35) rot=(0,0,1;0rad)
  Placement2 = pos=(20,17.5,470) rot=(-1,0,0;4.71239rad)
  Reference1 = -> Assembly [corner_gusset048.Edge1,corner_gusset048.Vertex1]
  Reference2 = -> Assembly [_040_extrusion___613.Edge58,_040_extrusion___613.Vertex40]
FEATURE [App::Link] corner_gusset049  label="corner gusset062"
  LinkPlacement = pos=(-161.402,970.363,430.833) rot=(0,0,1;3.14159rad)
  LinkedObject = -> Cut003
  Placement = pos=(-161.402,970.363,430.833) rot=(0,0,1;3.14159rad)
FEATURE [App::Link] corner_gusset050  label="corner gusset063"
  LinkPlacement = pos=(-161.402,440.363,430.833) rot=(0,0,1;1.5708rad)
  LinkedObject = -> Cut003
  Placement = pos=(-161.402,440.363,430.833) rot=(0,0,1;1.5708rad)
FEATURE [App::Link] corner_gusset051  label="corner gusset064"
  LinkPlacement = pos=(38.5977,970.363,430.833) rot=(0,0,-1;1.5708rad)
  LinkedObject = -> Cut003
  Placement = pos=(38.5977,970.363,430.833) rot=(0,0,-1;1.5708rad)
FEATURE [App::Link] corner_gusset052  label="corner gusset065"
  LinkPlacement = pos=(38.5978,440.363,430.833) rot=(0,-0.526034,0.852301;0rad)
  LinkedObject = -> Cut003
  Placement = pos=(38.5978,440.363,430.833) rot=(0,-0.526034,0.852301;0rad)
FEATURE [App::FeaturePython] Joint054  label="Fixed039"  # Assembly joint (typed FeaturePython)
  Activated = true
  AngleMax = 0
  AngleMin = 0
  Detach1 = false
  Detach2 = false
  Distance = 0
  Distance2 = 0
  EnableAngleMax = false
  EnableAngleMin = false
  EnableLengthMax = false
  EnableLengthMin = false
  JointType = 0 (Fixed)
  LengthMax = 0
  LengthMin = 0
  Offset2 = pos=(0,0,-2.5) rot=(0,0,-1;1.5708rad)
  Placement1 = pos=(-2.84e-14,0,35) rot=(0,0,1;0rad)
  Placement2 = pos=(-20,17.5,-1.137e-13) rot=(0,0.707107,0.707107;3.14159rad)
  Reference1 = -> Assembly [corner_gusset049.Edge1,corner_gusset049.Vertex1]
  Reference2 = -> Assembly [_040_extrusion___620.Edge51,_040_extrusion___620.Vertex35]
FEATURE [App::FeaturePython] Joint055  label="Fixed040"  # Assembly joint (typed FeaturePython)
  Activated = true
  AngleMax = 0
  AngleMin = 0
  Detach1 = false
  Detach2 = false
  Distance = 0
  Distance2 = 0
  EnableAngleMax = false
  EnableAngleMin = false
  EnableLengthMax = false
  EnableLengthMin = false
  JointType = 0 (Fixed)
  LengthMax = 0
  LengthMin = 0
  Offset2 = pos=(0,0,-2.5) rot=(0,0,1;3.14159rad)
  Placement1 = pos=(-5.68e-14,0,35) rot=(0,0,1;0rad)
  Placement2 = pos=(-20,17.5,530) rot=(0.57735,-0.57735,-0.57735;4.18879rad)
  Reference1 = -> Assembly [corner_gusset050.Edge1,corner_gusset050.Vertex1]
  Reference2 = -> Assembly [_040_extrusion___620.Edge52,_040_extrusion___620.Vertex36]
FEATURE [App::FeaturePython] Joint056  label="Fixed041"  # Assembly joint (typed FeaturePython)
  Activated = true
  AngleMax = 0
  AngleMin = 0
  Detach1 = false
  Detach2 = false
  Distance = 0
  Distance2 = 0
  EnableAngleMax = false
  EnableAngleMin = false
  EnableLengthMax = false
  EnableLengthMin = false
  JointType = 0 (Fixed)
  LengthMax = 0
  LengthMin = 0
  Offset2 = pos=(0,0,2.5) rot=(0,0,1;3.14159rad)
  Placement1 = pos=(0,-7.1e-15,35) rot=(0,0,1;0rad)
  Placement2 = pos=(60,17.5,0) rot=(-0.57735,0.57735,-0.57735;4.18879rad)
  Reference1 = -> Assembly [corner_gusset051.Edge1,corner_gusset051.Vertex1]
  Reference2 = -> Assembly [_040_extrusion___621.Edge86,_040_extrusion___621.Vertex61]
FEATURE [App::FeaturePython] Joint057  label="Fixed042"  # Assembly joint (typed FeaturePython)
  Activated = true
  AngleMax = 0
  AngleMin = 0
  Detach1 = false
  Detach2 = false
  Distance = 0
  Distance2 = 0
  EnableAngleMax = false
  EnableAngleMin = false
  EnableLengthMax = false
  EnableLengthMin = false
  JointType = 0 (Fixed)
  LengthMax = 0
  LengthMin = 0
  Offset2 = pos=(0,0,2.5) rot=(0,0,1;1.5708rad)
  Placement1 = pos=(0,0,35) rot=(0,0,1;0rad)
  Placement2 = pos=(60,17.5,530) rot=(-1,0,0;4.71239rad)
  Reference1 = -> Assembly [corner_gusset052.Edge1,corner_gusset052.Vertex1]
  Reference2 = -> Assembly [_040_extrusion___621.Edge136,_040_extrusion___621.Vertex101]
FEATURE [App::Link] _040_extrusion___623  label="8040 extrusion @ 535"
  LinkPlacement = pos=(-346.402,685.363,468.333) rot=(0,0,1;4.71239rad)
  LinkedObject = -> Body005
  Placement = pos=(-346.402,685.363,468.333) rot=(0,0,1;4.71239rad)
FEATURE [App::Link] _040_extrusion___624  label="8040 extrusion @ 536"
  LinkPlacement = pos=(-346.402,765.363,468.333) rot=(0,0,1;4.71239rad)
  LinkedObject = -> Body005
  Placement = pos=(-346.402,765.363,468.333) rot=(0,0,1;4.71239rad)
FEATURE [App::Link] _040_extrusion___625  label="8040 extrusion @ 537"
  LinkPlacement = pos=(223.598,685.363,468.333) rot=(0,0,-1;1.5708rad)
  LinkedObject = -> Body005
  Placement = pos=(223.598,685.363,468.333) rot=(0,0,-1;1.5708rad)
FEATURE [App::Link] _040_extrusion___626  label="8040 extrusion @ 538"
  LinkPlacement = pos=(223.598,765.363,468.333) rot=(0,0,-1;1.5708rad)
  LinkedObject = -> Body005
  Placement = pos=(223.598,765.363,468.333) rot=(0,0,-1;1.5708rad)
FEATURE [App::FeaturePython] Joint058  label="Fixed043"  # Assembly joint (typed FeaturePython)
  Activated = true
  AngleMax = 0
  AngleMin = 0
  Detach1 = false
  Detach2 = false
  Distance = 0
  Distance2 = 0
  EnableAngleMax = false
  EnableAngleMin = false
  EnableLengthMax = false
  EnableLengthMin = false
  JointType = 0 (Fixed)
  LengthMax = 0
  LengthMin = 0
  Offset2 = pos=(0,0,40) rot=(0,0,-1;1.5708rad)
  Placement1 = pos=(20,-20,0) rot=(-0.707107,0,0.707107;3.14159rad)
  Placement2 = pos=(-20,20,305) rot=(0,0,-1;1.5708rad)
  Reference1 = -> Assembly [_040_extrusion___623.Edge103,_040_extrusion___623.Edge103]
  Reference2 = -> Assembly [_040_extrusion___611.Edge2,_040_extrusion___611.Edge2]
FEATURE [App::FeaturePython] Joint059  label="Fixed044"  # Assembly joint (typed FeaturePython)
  Activated = true
  AngleMax = 0
  AngleMin = 0
  Detach1 = false
  Detach2 = false
  Distance = 0
  Distance2 = 0
  EnableAngleMax = false
  EnableAngleMin = false
  EnableLengthMax = false
  EnableLengthMin = false
  JointType = 0 (Fixed)
  LengthMax = 0
  LengthMin = 0
  Offset2 = pos=(0,0,-40) rot=(0,0,-1;1.5708rad)
  Placement1 = pos=(20,-20,0) rot=(-0.707107,0,0.707107;3.14159rad)
  Placement2 = pos=(-20,20,225) rot=(0,0,-1;1.5708rad)
  Reference1 = -> Assembly [_040_extrusion___624.Edge103,_040_extrusion___624.Edge103]
  Reference2 = -> Assembly [_040_extrusion___611.Edge2,_040_extrusion___611.Edge2]
FEATURE [App::FeaturePython] Joint060  label="Fixed045"  # Assembly joint (typed FeaturePython)
  Activated = true
  AngleMax = 0
  AngleMin = 0
  Detach1 = false
  Detach2 = false
  Distance = 0
  Distance2 = 0
  EnableAngleMax = false
  EnableAngleMin = false
  EnableLengthMax = false
  EnableLengthMin = false
  JointType = 0 (Fixed)
  LengthMax = 0
  LengthMin = 0
  Offset2 = pos=(0,0,40) rot=(0,0,-1;1.5708rad)
  Placement1 = pos=(20,-20,0) rot=(-0.707107,0,0.707107;3.14159rad)
  Placement2 = pos=(-20,20,305) rot=(0,0,-1;1.5708rad)
  Reference1 = -> Assembly [_040_extrusion___625.Edge103,_040_extrusion___625.Edge103]
  Reference2 = -> Assembly [_040_extrusion___530.Edge2,_040_extrusion___530.Edge2]
FEATURE [App::FeaturePython] Joint061  label="Fixed046"  # Assembly joint (typed FeaturePython)
  Activated = true
  AngleMax = 0
  AngleMin = 0
  Detach1 = false
  Detach2 = false
  Distance = 0
  Distance2 = 0
  EnableAngleMax = false
  EnableAngleMin = false
  EnableLengthMax = false
  EnableLengthMin = false
  JointType = 0 (Fixed)
  LengthMax = 0
  LengthMin = 0
  Offset2 = pos=(0,0,-40) rot=(0,0,-1;1.5708rad)
  Placement1 = pos=(20,-20,0) rot=(-0.707107,0,0.707107;3.14159rad)
  Placement2 = pos=(-20,20,225) rot=(0,0,-1;1.5708rad)
  Reference1 = -> Assembly [_040_extrusion___626.Edge103,_040_extrusion___626.Edge103]
  Reference2 = -> Assembly [_040_extrusion___530.Edge2,_040_extrusion___530.Edge2]
FEATURE [App::Link] corner_gusset053  label="corner gusset066"
  LinkPlacement = pos=(206.13,625.363,468.333) rot=(0.707107,0,0.707107;3.14159rad)
  LinkedObject = -> Cut003
  Placement = pos=(206.13,625.363,468.333) rot=(0.707107,0,0.707107;3.14159rad)
FEATURE [App::Link] corner_gusset054  label="corner gusset067"
  LinkPlacement = pos=(206.13,625.363,938.333) rot=(-0.57735,0.57735,-0.57735;2.0944rad)
  LinkedObject = -> Cut003
  Placement = pos=(206.13,625.363,938.333) rot=(-0.57735,0.57735,-0.57735;2.0944rad)
FEATURE [App::Link] corner_gusset055  label="corner gusset068"
  LinkPlacement = pos=(205.63,785.363,938.333) rot=(0,1,0;1.5708rad)
  LinkedObject = -> Cut003
  Placement = pos=(205.63,785.363,938.333) rot=(0,1,0;1.5708rad)
FEATURE [App::Link] corner_gusset056  label="corner gusset069"
  LinkPlacement = pos=(206.13,785.363,468.333) rot=(0.57735,0.57735,0.57735;2.0944rad)
  LinkedObject = -> Cut003
  Placement = pos=(206.13,785.363,468.333) rot=(0.57735,0.57735,0.57735;2.0944rad)
FEATURE [App::Link] corner_gusset057  label="corner gusset070"
  LinkPlacement = pos=(-363.935,625.363,468.333) rot=(0.707107,0,0.707107;3.14159rad)
  LinkedObject = -> Cut003
  Placement = pos=(-363.935,625.363,468.333) rot=(0.707107,0,0.707107;3.14159rad)
FEATURE [App::Link] corner_gusset058  label="corner gusset071"
  LinkPlacement = pos=(-363.935,625.363,938.333) rot=(0.57735,-0.57735,0.57735;4.18879rad)
  LinkedObject = -> Cut003
  Placement = pos=(-363.935,625.363,938.333) rot=(0.57735,-0.57735,0.57735;4.18879rad)
FEATURE [App::Link] corner_gusset059  label="corner gusset072"
  LinkPlacement = pos=(-363.935,785.363,938.333) rot=(0,1,0;1.5708rad)
  LinkedObject = -> Cut003
  Placement = pos=(-363.935,785.363,938.333) rot=(0,1,0;1.5708rad)
FEATURE [App::Link] corner_gusset060  label="corner gusset073"
  LinkPlacement = pos=(-363.902,785.363,468.333) rot=(0.57735,0.57735,0.57735;2.0944rad)
  LinkedObject = -> Cut003
  Placement = pos=(-363.902,785.363,468.333) rot=(0.57735,0.57735,0.57735;2.0944rad)
FEATURE [App::FeaturePython] Joint062  label="Fixed047"  # Assembly joint (typed FeaturePython)
  Activated = true
  AngleMax = 0
  AngleMin = 0
  Detach1 = false
  Detach2 = false
  Distance = 0
  Distance2 = 0
  EnableAngleMax = false
  EnableAngleMin = false
  EnableLengthMax = false
  EnableLengthMin = false
  JointType = 0 (Fixed)
  LengthMax = 0
  LengthMin = 0
  Offset2 = pos=(0,0,29.5) rot=(0,0,1;3.14159rad)
  Placement2 = pos=(60,-17.4675,0) rot=(-0.57735,0.57735,-0.57735;4.18879rad)
  Reference1 = -> Assembly [corner_gusset053.Edge1,corner_gusset053.Vertex2]
  Reference2 = -> Assembly [_040_extrusion___625.Edge86,_040_extrusion___625.Edge86]
FEATURE [App::FeaturePython] Joint063  label="Fixed048"  # Assembly joint (typed FeaturePython)
  Activated = true
  AngleMax = 0
  AngleMin = 0
  Detach1 = false
  Detach2 = false
  Distance = 0
  Distance2 = 0
  EnableAngleMax = false
  EnableAngleMin = false
  EnableLengthMax = false
  EnableLengthMin = false
  JointType = 0 (Fixed)
  LengthMax = 0
  LengthMin = 0
  Offset2 = pos=(0,0,12) rot=(0,0,1;1.5708rad)
  Placement1 = pos=(0,0,17.5) rot=(0,0,1;0rad)
  Placement2 = pos=(60,0.0325,470) rot=(-1,0,0;4.71239rad)
  Reference1 = -> Assembly [corner_gusset054.Edge1,corner_gusset054.Edge1]
  Reference2 = -> Assembly [_040_extrusion___625.Edge136,_040_extrusion___625.Edge136]
FEATURE [App::FeaturePython] Joint064  label="Fixed049"  # Assembly joint (typed FeaturePython)
  Activated = true
  AngleMax = 0
  AngleMin = 0
  Detach1 = false
  Detach2 = false
  Distance = 0
  Distance2 = 0
  EnableAngleMax = false
  EnableAngleMin = false
  EnableLengthMax = false
  EnableLengthMin = false
  JointType = 0 (Fixed)
  LengthMax = 0
  LengthMin = 0
  Offset2 = pos=(0,0,5) rot=(0,0,1;3.14159rad)
  Placement1 = pos=(0,0,35) rot=(0,0,1;0rad)
  Placement2 = pos=(-20,17.0325,470) rot=(0.57735,-0.57735,-0.57735;4.18879rad)
  Reference1 = -> Assembly [corner_gusset055.Edge1,corner_gusset055.Vertex1]
  Reference2 = -> Assembly [_040_extrusion___626.Edge52,_040_extrusion___626.Edge52]
FEATURE [App::FeaturePython] Joint065  label="Fixed050"  # Assembly joint (typed FeaturePython)
  Activated = true
  AngleMax = 0
  AngleMin = 0
  Detach1 = false
  Detach2 = false
  Distance = 0
  Distance2 = 0
  EnableAngleMax = false
  EnableAngleMin = false
  EnableLengthMax = false
  EnableLengthMin = false
  JointType = 0 (Fixed)
  LengthMax = 0
  LengthMin = 0
  Offset2 = pos=(0,0,-12) rot=(0,0,-1;1.5708rad)
  Placement1 = pos=(0,0,17.5) rot=(0,0,1;0rad)
  Placement2 = pos=(-20,0.0325,0) rot=(0,0.707107,0.707107;3.14159rad)
  Reference1 = -> Assembly [corner_gusset056.Edge1,corner_gusset056.Edge1]
  Reference2 = -> Assembly [_040_extrusion___626.Edge51,_040_extrusion___626.Edge51]
FEATURE [App::FeaturePython] Joint066  label="Fixed051"  # Assembly joint (typed FeaturePython)
  Activated = true
  AngleMax = 0
  AngleMin = 0
  Detach1 = false
  Detach2 = false
  Distance = 0
  Distance2 = 0
  EnableAngleMax = false
  EnableAngleMin = false
  EnableLengthMax = false
  EnableLengthMin = false
  JointType = 0 (Fixed)
  LengthMax = 0
  LengthMin = 0
  Offset2 = pos=(0,0,-12) rot=(0,0,1;3.14159rad)
  Placement1 = pos=(0,0,17.5) rot=(0,0,1;0rad)
  Placement2 = pos=(60,-0.0325,0) rot=(-0.57735,0.57735,-0.57735;4.18879rad)
  Reference1 = -> Assembly [corner_gusset057.Edge1,corner_gusset057.Edge1]
  Reference2 = -> Assembly [_040_extrusion___623.Edge94,_040_extrusion___623.Edge94]
FEATURE [App::FeaturePython] Joint067  label="Fixed052"  # Assembly joint (typed FeaturePython)
  Activated = true
  AngleMax = 0
  AngleMin = 0
  Detach1 = false
  Detach2 = false
  Distance = 0
  Distance2 = 0
  EnableAngleMax = false
  EnableAngleMin = false
  EnableLengthMax = false
  EnableLengthMin = false
  JointType = 0 (Fixed)
  LengthMax = 0
  LengthMin = 0
  Offset2 = pos=(0,0,-29.5) rot=(0,0,1;1.5708rad)
  Placement1 = pos=(0,0,35) rot=(0,0,1;0rad)
  Placement2 = pos=(60,17.4675,470) rot=(-1,0,0;4.71239rad)
  Reference1 = -> Assembly [corner_gusset058.Edge1,corner_gusset058.Vertex1]
  Reference2 = -> Assembly [_040_extrusion___623.Edge152,_040_extrusion___623.Edge152]
FEATURE [App::FeaturePython] Joint068  label="Fixed053"  # Assembly joint (typed FeaturePython)
  Activated = true
  AngleMax = 0
  AngleMin = 0
  Detach1 = false
  Detach2 = false
  Distance = 0
  Distance2 = 0
  EnableAngleMax = false
  EnableAngleMin = false
  EnableLengthMax = false
  EnableLengthMin = false
  JointType = 0 (Fixed)
  LengthMax = 0
  LengthMin = 0
  Offset2 = pos=(0,0,12) rot=(0,0,1;3.14159rad)
  Placement1 = pos=(-1.137e-13,0,17.5) rot=(0,0,1;0rad)
  Placement2 = pos=(-20,-0.0325,470) rot=(0.57735,-0.57735,-0.57735;4.18879rad)
  Reference1 = -> Assembly [corner_gusset059.Edge1,corner_gusset059.Edge1]
  Reference2 = -> Assembly [_040_extrusion___624.Edge28,_040_extrusion___624.Edge28]
FEATURE [App::FeaturePython] Joint069  label="Fixed054"  # Assembly joint (typed FeaturePython)
  Activated = true
  AngleMax = 0
  AngleMin = 0
  Detach1 = false
  Detach2 = false
  Distance = 0
  Distance2 = 0
  EnableAngleMax = false
  EnableAngleMin = false
  EnableLengthMax = false
  EnableLengthMin = false
  JointType = 0 (Fixed)
  LengthMax = 0
  LengthMin = 0
  Offset2 = pos=(0,0,37.5) rot=(0,0,-1;1.5708rad)
  Placement1 = pos=(0,0,35) rot=(0,0,1;0rad)
  Placement2 = pos=(-20,17.5,0) rot=(0,0.707107,0.707107;3.14159rad)
  Reference1 = -> Assembly [corner_gusset060.Edge1,corner_gusset060.Vertex1]
  Reference2 = -> Assembly [_040_extrusion___624.Edge27,_040_extrusion___624.Vertex17]
FEATURE [Sketcher::SketchObject] Sketch028
  ArcFitTolerance = 1e-06
  AttachmentSupport = -> [XY_Plane023]
  FullyConstrained = true
  MakeInternals = false
  MapMode = 5
  sketch-geometry (17):
    g0: LineSegment StartX=30 StartY=-37.75 StartZ=0 EndX=-30 EndY=-37.75 EndZ=0
    g1: LineSegment StartX=-30 StartY=-37.75 StartZ=0 EndX=-30 EndY=-5.25 EndZ=0
    g2: LineSegment StartX=-30 StartY=-5.25 StartZ=0 EndX=-18 EndY=-5.25 EndZ=0
    g3: LineSegment StartX=-18 StartY=-5.25 StartZ=0 EndX=-18 EndY=5.25 EndZ=0
    g4: LineSegment StartX=-18 StartY=5.25 StartZ=0 EndX=18 EndY=5.25 EndZ=0
    g5: LineSegment StartX=18 StartY=5.25 StartZ=0 EndX=18 EndY=-5.25 EndZ=0
    g6: LineSegment StartX=18 StartY=-5.25 StartZ=0 EndX=30 EndY=-5.25 EndZ=0
    g7: LineSegment StartX=30 StartY=-5.25 StartZ=0 EndX=30 EndY=-37.75 EndZ=0
    g8: Circle CenterX=-23 CenterY=-30.75 CenterZ=0 NormalX=0 NormalY=0 NormalZ=1 AngleXU=0 Radius=2.75
    g9: Circle CenterX=-23 CenterY=-12.75 CenterZ=0 NormalX=0 NormalY=0 NormalZ=1 AngleXU=0 Radius=2.75
    g10: Circle CenterX=23 CenterY=-12.75 CenterZ=0 NormalX=0 NormalY=0 NormalZ=1 AngleXU=0 Radius=2.75
    g11: Circle CenterX=23 CenterY=-30.75 CenterZ=0 NormalX=0 NormalY=0 NormalZ=1 AngleXU=0 Radius=2.75
    g12: LineSegment [constr] StartX=-23 StartY=-12.75 StartZ=0 EndX=23 EndY=-12.75 EndZ=0
    g13: LineSegment [constr] StartX=-23 StartY=-30.75 StartZ=0 EndX=23 EndY=-30.75 EndZ=0
    g14: LineSegment [constr] StartX=-23 StartY=-12.75 StartZ=0 EndX=-23 EndY=-30.75 EndZ=0
    g15: LineSegment [constr] StartX=23 StartY=-12.75 StartZ=0 EndX=23 EndY=-30.75 EndZ=0
    g16: Circle CenterX=0 CenterY=-12.75 CenterZ=0 NormalX=0 NormalY=0 NormalZ=1 AngleXU=0 Radius=6
  constraints (41):
    c: Horizontal(g0)
    c: Coincident(g1,g0)
    c: Coincident(g2,g1)
    c: Coincident(g3,g2)
    c: Vertical(g3)
    c: Coincident(g4,g3)
    c: Coincident(g5,g4)
    c: Coincident(g7,g0)
    c: Coincident(g6,g7)
    c: Coincident(g5,g6)
    c: Horizontal(g6)
    c: Vertical(g1)
    c: Vertical(g7)
    c: Tangent(g2,g6)
    c: Equal(g2,g6)
    c: DistanceX(g0,g0) = 60
    c: Symmetric(g3,g4,g-2)
    c: Symmetric(g5,g4,g-1)
    c: DistanceY(g7,g7) = 32.5
    c: Distance(g0,g4) = 43
    c: DistanceX(g2,g2) = 12
    c: Equal(g11,g10)
    c: Equal(g10,g9)
    c: Equal(g9,g8)
    c: Diameter(g8) = 5.5
    c: Distance(g8,g0) = 7
    c: DistanceY(g8,g9) = 18
    c: Coincident(g12,g9)
    c: Coincident(g12,g10)
    c: Coincident(g13,g8)
    c: Coincident(g13,g11)
    c: Symmetric(g9,g10,g-2)
    c: Symmetric(g8,g11,g-2)
    c: Coincident(g14,g9)
    c: Coincident(g14,g8)
    c: Vertical(g14)
    c: Coincident(g15,g10)
    c: Coincident(g15,g11)
    c: Distance(g15,g14) = 46
    c: Symmetric(g12,g12,g16)
    c: Diameter(g16) = 12
FEATURE [PartDesign::Pad] Pad018
  Direction = (0,0,1)
  Length = 20
  Length2 = 10
  Profile = -> Sketch028
  ReferenceAxis = -> Sketch028 [N_Axis]
  Refine = true
  Suppressed = false
  Type = 0
FEATURE [Sketcher::SketchObject] Sketch029
  ArcFitTolerance = 1e-06
  AttachmentSupport = -> [Pad018]
  FullyConstrained = true
  MakeInternals = false
  MapMode = 5
  Placement = pos=(0,-5.25,0) rot=(0,0.707107,0.707107;3.14159rad)
  sketch-geometry (2):
    g0: Circle CenterX=-23 CenterY=10 CenterZ=0 NormalX=0 NormalY=0 NormalZ=1 AngleXU=0 Radius=3.3
    g1: Circle CenterX=23 CenterY=10 CenterZ=0 NormalX=0 NormalY=0 NormalZ=1 AngleXU=0 Radius=3.3
  constraints (5):
    c: Equal(g1,g0)
    c: Diameter(g0) = 6.6
    c: Symmetric(g0,g1,g-2)
    c: Distance(g0,g-1) = 10
    c: DistanceX(g0,g1) = 46
FEATURE [PartDesign::Pocket] Pocket002
  BaseFeature = -> Pad018
  Direction = (0,-1,2e-16)
  Length = 5
  Length2 = 5
  Profile = -> Sketch029
  ReferenceAxis = -> Sketch029 [N_Axis]
  Refine = true
  Suppressed = false
  Type = 1
FEATURE [PartDesign::Body] Body018  label="BF12"
  AllowCompound = false
  Group = -> [Sketch028,Pad018,Sketch029,Pocket002]
  Origin = -> Origin023
  Tip = -> Pocket002
FEATURE [App::Link] BF12  label="BF013"
  LinkPlacement = pos=(-61.4023,410.363,506.083) rot=(0,0.707107,0.707107;3.14159rad)
  LinkedObject = -> Body018
  Placement = pos=(-61.4023,410.363,506.083) rot=(0,0.707107,0.707107;3.14159rad)
FEATURE [Sketcher::SketchObject] Sketch030
  ArcFitTolerance = 1e-06
  AttachmentSupport = -> [XY_Plane024]
  FullyConstrained = true
  MakeInternals = false
  MapMode = 5
  sketch-geometry (18):
    g0: LineSegment StartX=0 StartY=0 StartZ=0 EndX=50 EndY=0 EndZ=0
    g1: LineSegment StartX=50 StartY=0 StartZ=0 EndX=50 EndY=73 EndZ=0
    g2: LineSegment StartX=50 StartY=73 StartZ=0 EndX=0 EndY=73 EndZ=0
    g3: LineSegment StartX=0 StartY=73 StartZ=0 EndX=0 EndY=0 EndZ=0
    g4: Circle CenterX=9 CenterY=54.5 CenterZ=0 NormalX=0 NormalY=0 NormalZ=1 AngleXU=0 Radius=2.5
    g5: Circle CenterX=9 CenterY=18.5 CenterZ=0 NormalX=0 NormalY=0 NormalZ=1 AngleXU=0 Radius=2.5
    g6: Circle CenterX=41 CenterY=54.5 CenterZ=0 NormalX=0 NormalY=0 NormalZ=1 AngleXU=0 Radius=2.5
    g7: Circle CenterX=41 CenterY=18.5 CenterZ=0 NormalX=0 NormalY=0 NormalZ=1 AngleXU=0 Radius=2.5
    g8: LineSegment [constr] StartX=9 StartY=54.5 StartZ=0 EndX=41 EndY=54.5 EndZ=0
    g9: LineSegment [constr] StartX=9 StartY=18.5 StartZ=0 EndX=41 EndY=18.5 EndZ=0
    g10: LineSegment [constr] StartX=9 StartY=54.5 StartZ=0 EndX=9 EndY=18.5 EndZ=0
    g11: LineSegment [constr] StartX=41 StartY=54.5 StartZ=0 EndX=41 EndY=18.5 EndZ=0
    g12: GeomPoint X=25 Y=54.5 Z=0
    g13: GeomPoint X=41 Y=36.5 Z=0
    g14: GeomPoint X=9 Y=36.5 Z=0
    g15: GeomPoint X=25 Y=18.5 Z=0
    g16: LineSegment [constr] StartX=9 StartY=36.5 StartZ=0 EndX=41 EndY=36.5 EndZ=0
    g17: LineSegment [constr] StartX=25 StartY=54.5 StartZ=0 EndX=25 EndY=18.5 EndZ=0
  constraints (37):
    c: Coincident(g0,g1)
    c: Coincident(g1,g2)
    c: Coincident(g2,g3)
    c: Coincident(g3,g0)
    c: Horizontal(g0)
    c: Horizontal(g2)
    c: Vertical(g1)
    c: Vertical(g3)
    c: Coincident(g0,g-1)
    c: DistanceY(g1,g1) = 73
    c: DistanceX(g2,g2) = 50
    c: Equal(g4,g6)
    c: Equal(g6,g7)
    c: Equal(g7,g5)
    c: Coincident(g8,g4)
    c: Coincident(g8,g6)
    c: Horizontal(g8)
    c: Coincident(g9,g5)
    c: Coincident(g9,g7)
    c: Coincident(g10,g4)
    c: Coincident(g10,g5)
    c: Vertical(g10)
    c: Coincident(g11,g6)
    c: Coincident(g11,g7)
    c: Diameter(g6) = 5
    c: DistanceY(g11,g11) = 36
    c: Distance(g8,g8) = 32
    c: Symmetric(g8,g8,g12)
    c: Symmetric(g11,g11,g13)
    c: Symmetric(g10,g10,g14)
    c: Symmetric(g9,g9,g15)
    c: Coincident(g16,g14)
    c: Coincident(g16,g13)
    c: Coincident(g17,g12)
    c: Coincident(g17,g15)
    c: Symmetric(g1,g0,g16)
    c: Symmetric(g2,g1,g17)
FEATURE [PartDesign::Pad] Pad019
  Direction = (0,0,1)
  Length = 30
  Length2 = 10
  Profile = -> Sketch030
  ReferenceAxis = -> Sketch030 [N_Axis]
  Refine = true
  Suppressed = false
  Type = 0
FEATURE [PartDesign::Body] Body019  label="hgr carriage spacer"
  AllowCompound = false
  Group = -> [Sketch030,Pad019]
  Origin = -> Origin024
  Tip = -> Pad019
FEATURE [App::Link] hgr_carriage_spacer  label="hgr carriage spacer001"
  LinkPlacement = pos=(-6.40225,761.643,498.333) rot=(0,-0.526034,0.852301;0rad)
  LinkedObject = -> Body019
  Placement = pos=(-6.40225,761.643,498.333) rot=(0,-0.526034,0.852301;0rad)
FEATURE [App::FeaturePython] Joint070  label="Fixed055"  # Assembly joint (typed FeaturePython)
  Activated = true
  AngleMax = 0
  AngleMin = 0
  Detach1 = false
  Detach2 = false
  Distance = 0
  Distance2 = 0
  EnableAngleMax = false
  EnableAngleMin = false
  EnableLengthMax = false
  EnableLengthMin = false
  JointType = 0 (Fixed)
  LengthMax = 0
  LengthMin = 0
  Offset2 = pos=(0,0,0) rot=(0,0,1;3.14159rad)
  Placement1 = pos=(41,54.5,-5.68e-14) rot=(0,0,1;0rad)
  Placement2 = pos=(16,25.4,18.5) rot=(1,0,0;4.71239rad)
  Reference1 = -> Assembly [hgr_carriage_spacer.Edge23,hgr_carriage_spacer.Edge23]
  Reference2 = -> Assembly [HGR20_carriage001.Edge14,HGR20_carriage001.Edge14]
FEATURE [App::Link] hgr_carriage_spacer001  label="hgr carriage spacer002"
  LinkPlacement = pos=(-166.402,643.825,498.333) rot=(0,-0.99808,0;0rad)
  LinkedObject = -> Body019
  Placement = pos=(-166.402,643.825,498.333) rot=(0,-0.99808,0;0rad)
FEATURE [App::Link] hgr_carriage_spacer002  label="hgr carriage spacer003"
  LinkPlacement = pos=(-6.40226,643.825,498.333) rot=(0,-0.526034,0.852301;0rad)
  LinkedObject = -> Body019
  Placement = pos=(-6.40226,643.825,498.333) rot=(0,-0.526034,0.852301;0rad)
FEATURE [App::Link] hgr_carriage_spacer003  label="hgr carriage spacer004"
  LinkPlacement = pos=(-166.402,761.643,498.333) rot=(0,-0.99808,0;0rad)
  LinkedObject = -> Body019
  Placement = pos=(-166.402,761.643,498.333) rot=(0,-0.99808,0;0rad)
FEATURE [App::FeaturePython] Joint071  label="Fixed056"  # Assembly joint (typed FeaturePython)
  Activated = true
  AngleMax = 0
  AngleMin = 0
  Detach1 = false
  Detach2 = false
  Distance = 0
  Distance2 = 0
  EnableAngleMax = false
  EnableAngleMin = false
  EnableLengthMax = false
  EnableLengthMin = false
  JointType = 0 (Fixed)
  LengthMax = 0
  LengthMin = 0
  Offset2 = pos=(0,0,0) rot=(0,0,1;3.14159rad)
  Placement1 = pos=(9,54.5,0) rot=(0,0,1;0rad)
  Placement2 = pos=(-16,25.4,18.5) rot=(1,0,0;4.71239rad)
  Reference1 = -> Assembly [hgr_carriage_spacer003.Edge20,hgr_carriage_spacer003.Edge20]
  Reference2 = -> Assembly [HGR20_carriage002.Edge13,HGR20_carriage002.Edge13]
FEATURE [App::FeaturePython] Joint072  label="Fixed057"  # Assembly joint (typed FeaturePython)
  Activated = true
  AngleMax = 0
  AngleMin = 0
  Detach1 = false
  Detach2 = false
  Distance = 0
  Distance2 = 0
  EnableAngleMax = false
  EnableAngleMin = false
  EnableLengthMax = false
  EnableLengthMin = false
  JointType = 0 (Fixed)
  LengthMax = 0
  LengthMin = 0
  Offset2 = pos=(0,0,0) rot=(0,0,1;3.14159rad)
  Placement1 = pos=(9,54.5,0) rot=(0,0,1;0rad)
  Placement2 = pos=(-16,25.4,18.5) rot=(1,0,0;4.71239rad)
  Reference1 = -> Assembly [hgr_carriage_spacer001.Edge20,hgr_carriage_spacer001.Edge20]
  Reference2 = -> Assembly [HGR20_carriage003.Edge13,HGR20_carriage003.Edge13]
FEATURE [App::FeaturePython] Joint073  label="Fixed058"  # Assembly joint (typed FeaturePython)
  Activated = true
  AngleMax = 0
  AngleMin = 0
  Detach1 = false
  Detach2 = false
  Distance = 0
  Distance2 = 0
  EnableAngleMax = false
  EnableAngleMin = false
  EnableLengthMax = false
  EnableLengthMin = false
  JointType = 0 (Fixed)
  LengthMax = 0
  LengthMin = 0
  Offset2 = pos=(0,0,0) rot=(0,0,1;3.14159rad)
  Placement1 = pos=(41,54.5,0) rot=(0,0,1;0rad)
  Placement2 = pos=(16,25.4,18.5) rot=(1,0,0;4.71239rad)
  Reference1 = -> Assembly [hgr_carriage_spacer002.Edge23,hgr_carriage_spacer002.Edge23]
  Reference2 = -> Assembly [HGR20_carriage.Edge14,HGR20_carriage.Edge14]
FEATURE [Sketcher::SketchObject] Sketch031
  ArcFitTolerance = 1e-06
  AttachmentSupport = -> [XY_Plane025]
  FullyConstrained = true
  MakeInternals = false
  MapMode = 5
  sketch-geometry (8):
    g0: LineSegment StartX=0 StartY=0 StartZ=0 EndX=500 EndY=0 EndZ=0
    g1: LineSegment StartX=0 StartY=0 StartZ=0 EndX=0 EndY=5 EndZ=0
    g2: LineSegment StartX=0 StartY=5 StartZ=0 EndX=54 EndY=5 EndZ=0
    g3: LineSegment StartX=54 StartY=5 StartZ=0 EndX=54 EndY=8 EndZ=0
    g4: LineSegment StartX=500 StartY=0 StartZ=0 EndX=500 EndY=5 EndZ=0
    g5: LineSegment StartX=500 StartY=5 StartZ=0 EndX=489 EndY=5 EndZ=0
    g6: LineSegment StartX=489 StartY=5 StartZ=0 EndX=489 EndY=8 EndZ=0
    g7: LineSegment StartX=489 StartY=8 StartZ=0 EndX=54 EndY=8 EndZ=0
  constraints (23):
    c: Coincident(g0,g-1)
    c: Horizontal(g0)
    c: DistanceX(g0,g0) = 500
    c: Coincident(g1,g0)
    c: PointOnObject(g1,g-2)
    c: Distance(g1,g1) = 5
    c: Coincident(g2,g1)
    c: Horizontal(g2)
    c: DistanceX(g2,g2) = 54
    c: Coincident(g3,g2)
    c: Vertical(g3)
    c: Distance(g3,g3) = 3
    c: Coincident(g4,g0)
    c: Vertical(g4)
    c: DistanceY(g4,g4) = 5
    c: Coincident(g5,g4)
    c: Horizontal(g5)
    c: DistanceX(g5,g5) = 11
    c: Coincident(g6,g5)
    c: Vertical(g6)
    c: DistanceY(g6,g6) = 3
    c: Coincident(g7,g6)
    c: Coincident(g7,g3)
FEATURE [PartDesign::Revolution] Revolution
  Angle = 360
  Angle2 = 60
  Axis = (1,0,0)
  Base = (0,0,0)
  Profile = -> Sketch031
  ReferenceAxis = -> Sketch031 [H_Axis]
  Refine = true
  Suppressed = false
  Type = 0
FEATURE [PartDesign::Body] Body020  label="sfu1605x500mm"
  AllowCompound = false
  Group = -> [Sketch031,Revolution]
  Origin = -> Origin025
  Tip = -> Revolution
FEATURE [App::DocumentObjectGroup] Parts
  Group = -> [Body001,Body002,Body003,Body004,Body005,Body006,Body,Body007,Body008,Cut007,Body019,Body018,Body020]
FEATURE [App::Link] sfu1605x500mm  label="sfu1605x500mm001"
  LinkedObject = -> Body020
FEATURE [App::FeaturePython] Joint074  label="Distance007"  # Assembly joint (typed FeaturePython)
  Activated = true
  AngleMax = 0
  AngleMin = 0
  Detach1 = false
  Detach2 = false
  Distance = 0
  Distance2 = 0
  EnableAngleMax = false
  EnableAngleMin = false
  EnableLengthMax = false
  EnableLengthMin = false
  JointType = 5 (Distance)
  LengthMax = 0
  LengthMin = 0
  Placement1 = pos=(0,-37.75,10) rot=(0,-0.707107,0.707107;3.14159rad)
  Placement2 = pos=(20,-12.0325,305) rot=(-0.57735,0.57735,-0.57735;2.0944rad)
  Reference1 = -> Assembly [BF12.Face1,BF12.Edge6]
  Reference2 = -> Assembly [_040_extrusion___610.Face19,_040_extrusion___610.Face19]
FEATURE [App::FeaturePython] Joint075  label="Distance008"  # Assembly joint (typed FeaturePython)
  Activated = true
  AngleMax = 0
  AngleMin = 0
  Detach1 = false
  Detach2 = false
  Distance = 10
  Distance2 = 0
  EnableAngleMax = false
  EnableAngleMin = false
  EnableLengthMax = false
  EnableLengthMin = false
  JointType = 5 (Distance)
  LengthMax = 0
  LengthMin = 0
  Placement1 = pos=(-7.1e-15,-18.1219,20) rot=(0,0,1;0rad)
  Placement2 = pos=(12.0325,20,305) rot=(1,0,0;4.71239rad)
  Reference1 = -> Assembly [BF12.Face4,BF12.Face4]
  Reference2 = -> Assembly [_040_extrusion___610.Face10,_040_extrusion___610.Face10]
FEATURE [App::FeaturePython] Joint076  label="Distance009"  # Assembly joint (typed FeaturePython)
  Activated = true
  AngleMax = 0
  AngleMin = 0
  Detach1 = false
  Detach2 = false
  Distance = 235
  Distance2 = 0
  EnableAngleMax = false
  EnableAngleMin = false
  EnableLengthMax = false
  EnableLengthMin = false
  JointType = 5 (Distance)
  LengthMax = 0
  LengthMin = 0
  Placement1 = pos=(30,-21.5,10) rot=(0.57735,-0.57735,0.57735;4.18879rad)
  Placement2 = pos=(20,-12.0325,235) rot=(-0.576242,0.576242,-0.576242;2.0944rad)
  Reference1 = -> Assembly [BF12.Face2,BF12.Face2]
  Reference2 = -> Assembly [_040_extrusion___613.Face19,_040_extrusion___613.Vertex37]
FEATURE [Assembly::JointGroup] Joints
  Group = -> [GroundedJoint,Joint,Joint001,Joint002,Joint003,Joint004,Joint005,Joint006,Joint007,Joint008,Joint009,Joint010,Joint011,Joint012,Joint013,Joint014,Joint015,Joint016,Joint017,Joint018,Joint019,Joint020,Joint021,Joint022,Joint023,Joint024,Joint025,Joint026,Joint027,Joint028,Joint029,Joint030,Joint031,Joint032,Joint033,Joint034,Joint035,Joint036,Joint037,Joint038,Joint039,Joint040,Joint041,Joint042,+34 more]
FEATURE [Assembly::AssemblyObject] Assembly
  Group = -> [Joints,_040_extrusion___610,GroundedJoint,_040_extrusion___530,Joint,_040_extrusion___611,Joint001,_040_extrusion___612,Joint002,_040_extrusion___470,Joint003,_040_extrusion___613,Joint004,_040_extrusion___614,Joint005,_040_extrusion___615,Joint006,_040_extrusion___616,Joint007,_040_extrusion___617,Joint008,_040_extrusion___618,Joint009,_040_extrusion___619,Joint010,corner_gusset,Joint011,+122 more]
  Origin = -> Origin022
  Type = Assembly

RESOLVED EXTERNAL PARTS (link-assembly join: the EXTERNAL_REF files above that resolve inside this repo's crawl, each included once):
---- part ../xcadlib/nema23.FCStd = doc fcstd_9b31dcd9e336 ----
FCSTD DOCUMENT  (FreeCAD 1.0R38642 (Git))
Label: nema23
License: All rights reserved
LicenseURL: https://en.wikipedia.org/wiki/All_rights_reserved
objects: PartDesign::Pad×4, Spreadsheet::Sheet×1, Sketcher::SketchObject×1, PartDesign::Body×1
note: 15 computed .brp shape members not serialized (recipe doc carries the construction recipe); baked Part::Feature solids carry a one-line shape summary decoded from their .brp

FEATURE [Spreadsheet::Sheet] Spreadsheet
  cells = A1='width; B1(width)==56.4 mm; A2='attachment hole gap; B2(hole_gap)==47.14 mm; A3='body depth; B3(depth)==75 mm; A4='shaft length (from main body, not circle); B4(shaft_length)==21 mm; A5='face circle diameter; B5(face_diameter)==1.5 in; A6='face circle thickness; B6(face_thickness)==1.6 mm; A7='shaft diameter; B7(shaft_diameter)==0.315 in; A8='mounting hole diameter; B8(mounting_hole_diameter)==5 mm; A9='mounting plate thickness; B9(plate_thickness)==0.185 in; A10='cross body arm thickness; B10(arm_thickness)==1.5 in
FEATURE [Sketcher::SketchObject] Sketch
  ArcFitTolerance = 1e-06
  AttachmentSupport = -> [XY_Plane]
  FullyConstrained = true
  MakeInternals = false
  MapMode = 5
  expr: Constraints[13] = <<Spreadsheet>>.shaft_diameter
  expr: Constraints[1] = <<Spreadsheet>>.face_diameter
  expr: Constraints[2] = <<Spreadsheet>>.mounting_hole_diameter
  expr: Constraints[33] = (<<Spreadsheet>>.width - <<Spreadsheet>>.arm_thickness) / 2
  expr: Constraints[64] = <<Spreadsheet>>.width
  expr: Constraints[6] = <<Spreadsheet>>.hole_gap
  expr: Constraints[7] = <<Spreadsheet>>.hole_gap
  sketch-geometry (26):
    g0: Circle CenterX=0 CenterY=0 CenterZ=0 NormalX=0 NormalY=0 NormalZ=1 AngleXU=0 Radius=19.05
    g1: Circle CenterX=-23.57 CenterY=23.57 CenterZ=0 NormalX=0 NormalY=0 NormalZ=1 AngleXU=0 Radius=2.5
    g2: Circle CenterX=23.57 CenterY=23.57 CenterZ=0 NormalX=0 NormalY=0 NormalZ=1 AngleXU=0 Radius=2.5
    g3: Circle CenterX=23.57 CenterY=-23.57 CenterZ=0 NormalX=0 NormalY=0 NormalZ=1 AngleXU=0 Radius=2.5
    g4: Circle CenterX=-23.57 CenterY=-23.57 CenterZ=0 NormalX=0 NormalY=0 NormalZ=1 AngleXU=0 Radius=2.5
    g5: Circle CenterX=0 CenterY=0 CenterZ=0 NormalX=0 NormalY=0 NormalZ=1 AngleXU=0 Radius=4.0005
    g6: LineSegment StartX=-19.05 StartY=28.2 StartZ=0 EndX=-19.05 EndY=19.05 EndZ=0
    g7: LineSegment StartX=-19.05 StartY=19.05 StartZ=0 EndX=-28.2 EndY=19.05 EndZ=0
    g8: LineSegment StartX=-28.2 StartY=-19.05 StartZ=0 EndX=-19.05 EndY=-19.05 EndZ=0
    g9: LineSegment StartX=-19.05 StartY=-19.05 StartZ=0 EndX=-19.05 EndY=-28.2 EndZ=0
    g10: LineSegment StartX=19.05 StartY=-28.2 StartZ=0 EndX=19.05 EndY=-19.05 EndZ=0
    g11: LineSegment StartX=19.05 StartY=-19.05 StartZ=0 EndX=28.2 EndY=-19.05 EndZ=0
    g12: LineSegment StartX=19.05 StartY=28.2 StartZ=0 EndX=19.05 EndY=19.05 EndZ=0
    g13: LineSegment StartX=19.05 StartY=19.05 StartZ=0 EndX=28.2 EndY=19.05 EndZ=0
    g14: LineSegment StartX=-28.2 StartY=19.05 StartZ=0 EndX=-28.2 EndY=-19.05 EndZ=0
    g15: LineSegment StartX=-19.05 StartY=-28.2 StartZ=0 EndX=19.05 EndY=-28.2 EndZ=0
    g16: LineSegment StartX=28.2 StartY=-19.05 StartZ=0 EndX=28.2 EndY=19.05 EndZ=0
    g17: LineSegment StartX=19.05 StartY=28.2 StartZ=0 EndX=-19.05 EndY=28.2 EndZ=0
    g18: LineSegment StartX=-28.2 StartY=19.05 StartZ=0 EndX=-28.2 EndY=28.2 EndZ=0
    g19: LineSegment StartX=-28.2 StartY=28.2 StartZ=0 EndX=-19.05 EndY=28.2 EndZ=0
    g20: LineSegment StartX=19.05 StartY=28.2 StartZ=0 EndX=28.2 EndY=28.2 EndZ=0
    g21: LineSegment StartX=28.2 StartY=28.2 StartZ=0 EndX=28.2 EndY=19.05 EndZ=0
    g22: LineSegment StartX=28.2 StartY=-19.05 StartZ=0 EndX=28.2 EndY=-28.2 EndZ=0
    g23: LineSegment StartX=28.2 StartY=-28.2 StartZ=0 EndX=19.05 EndY=-28.2 EndZ=0
    g24: LineSegment StartX=-19.05 StartY=-28.2 StartZ=0 EndX=-28.2 EndY=-28.2 EndZ=0
    g25: LineSegment StartX=-28.2 StartY=-28.2 StartZ=0 EndX=-28.2 EndY=-19.05 EndZ=0
  constraints (68):
    c: Coincident(g0,g-1)
    c: Diameter(g0) = 38.1
    c: Diameter(g1) = 5
    c: Equal(g1,g4)
    c: Equal(g1,g2)
    c: Equal(g1,g3)
    c: DistanceY(g4,g1) = 47.14
    c: DistanceX(g4,g3) = 47.14
    c: Horizontal(g3,g4)
    c: Vertical(g4,g1)
    c: Symmetric(g2,g1,g-2)
    c: Symmetric(g2,g3,g-1)
    c: Coincident(g5,g0)
    c: Diameter(g5) = 8.001
    c: Coincident(g7,g6)
    c: Coincident(g9,g8)
    c: Coincident(g13,g12)
    c: Vertical(g6)
    c: Vertical(g9)
    c: Vertical(g10)
    c: Vertical(g12)
    c: Horizontal(g7)
    c: Horizontal(g13)
    c: Horizontal(g11)
    c: Horizontal(g8)
    c: Coincident(g11,g10)
    c: Equal(g12,g6)
    c: Equal(g6,g7)
    c: Equal(g7,g13)
    c: Equal(g13,g11)
    c: Equal(g11,g10)
    c: Equal(g10,g9)
    c: Equal(g9,g8)
    c: Distance(g13,g13) = 9.15
    c: Coincident(g14,g7)
    c: Coincident(g14,g8)
    c: Vertical(g14)
    c: Coincident(g15,g9)
    c: Coincident(g15,g10)
    c: Horizontal(g15)
    c: Coincident(g16,g11)
    c: Coincident(g16,g13)
    c: Vertical(g16)
    c: Coincident(g17,g12)
    c: Coincident(g17,g6)
    c: Horizontal(g17)
    c: Coincident(g18,g7)
    c: Coincident(g19,g18)
    c: Coincident(g19,g6)
    c: Coincident(g20,g12)
    c: Coincident(g21,g20)
    c: Coincident(g21,g13)
    c: Coincident(g22,g11)
    c: Coincident(g23,g22)
    c: Coincident(g23,g10)
    c: Coincident(g24,g9)
    c: Horizontal(g24)
    c: Coincident(g25,g24)
    c: Coincident(g25,g8)
    c: Horizontal(g19)
    c: Horizontal(g23)
    c: Vertical(g25)
    c: Vertical(g21)
    c: Vertical(g22)
    c: Distance(g16,g14) = 56.4
    c: Equal(g14,g17)
    c: Symmetric(g18,g24,g-1)
    c: Symmetric(g18,g20,g-2)
FEATURE [PartDesign::Pad] Pad001  label="faceplate"
  Direction = (0,0,1)
  Length = 1.6
  Length2 = 10
  Profile = -> Sketch [Edge1]
  ReferenceAxis = -> Sketch [N_Axis]
  Refine = true
  Suppressed = false
  Type = 0
  expr: Length = <<Spreadsheet>>.face_thickness
FEATURE [PartDesign::Pad] Pad002  label="shaft"
  BaseFeature = -> Pad001
  Direction = (0,0,1)
  Length = 21
  Length2 = 10
  Profile = -> Sketch [Edge6]
  ReferenceAxis = -> Sketch [N_Axis]
  Refine = true
  Suppressed = false
  Type = 0
  expr: Length = <<Spreadsheet>>.shaft_length
FEATURE [PartDesign::Pad] Pad  label="mounting_plate"
  BaseFeature = -> Pad002
  Direction = (0,0,1)
  Length = 4.699
  Length2 = 10
  Profile = -> Sketch [Edge22,Edge26,Edge25,Edge7,Edge2,Edge9,Edge8,Edge12,Edge14,Edge13,Edge5,Edge17,Edge20,Edge21,Edge4,Edge3]
  ReferenceAxis = -> Sketch [N_Axis]
  Refine = true
  Reversed = true
  Suppressed = false
  Type = 0
  expr: Length = <<Spreadsheet>>.plate_thickness
FEATURE [PartDesign::Pad] Pad003  label="body"
  BaseFeature = -> Pad
  Direction = (0,0,1)
  Length = 75
  Length2 = 10
  Profile = -> Sketch [Edge22,Edge19,Edge18,Edge17,Edge16,Edge15,Edge12,Edge11,Edge10,Edge7,Edge24,Edge23]
  ReferenceAxis = -> Sketch [N_Axis]
  Refine = true
  Reversed = true
  Suppressed = false
  Type = 0
  expr: Length = <<Spreadsheet>>.depth
FEATURE [PartDesign::Body] Body  label="nema23"
  AllowCompound = false
  Group = -> [Sketch,Pad001,Pad002,Pad,Pad003]
  Origin = -> Origin
  Tip = -> Pad003
